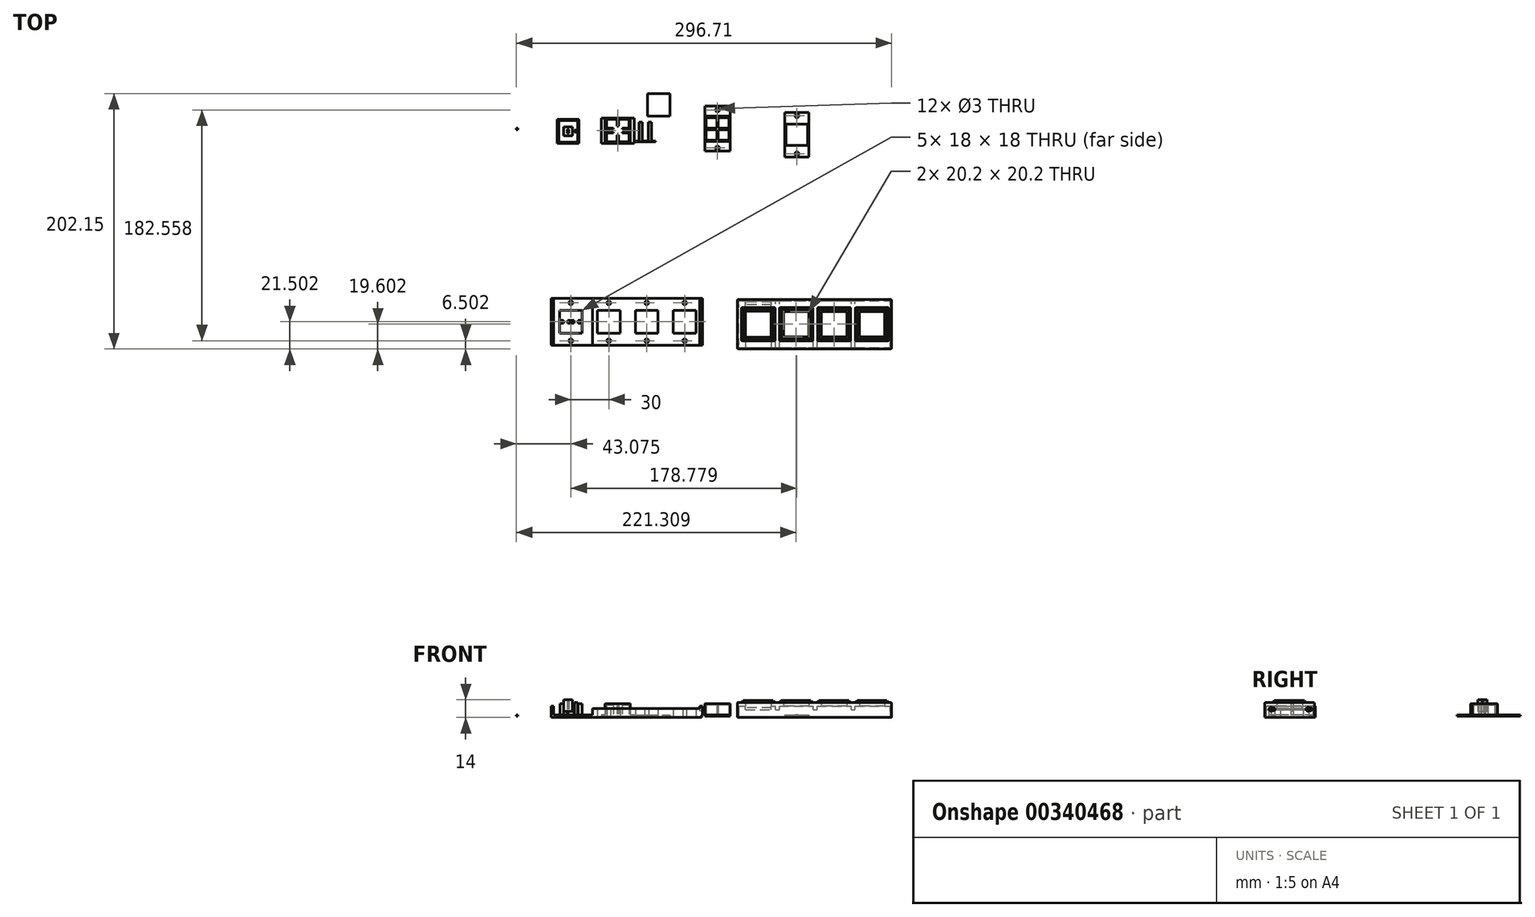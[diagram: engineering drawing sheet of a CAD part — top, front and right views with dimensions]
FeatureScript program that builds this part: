
annotation { "Feature Type Name" : "Feature", "Feature Type Description" : "" }
export const myFeature = defineFeature(function(context is Context, id is Id, definition is map)
    precondition{}
    {
        {
            var Q0;
            Q0=qCreatedBy(makeId("Top.planeOp"),FACE);
            var sketch = newSketch(context, id + "F0", { "sketchPlane" : qUnion([Q0])});
            skPoint(sketch, "E0.middle", {"position": v(0, 0) * mm});
            skLineSegment(sketch, "E1.bottom", {"start": v(10, -10) * mm, "end": v(-10, -10) * mm});
            skLineSegment(sketch, "E1.top", {"start": v(10, 10) * mm, "end": v(-10, 10) * mm});
            skLineSegment(sketch, "E1.left", {"start": v(10, -10) * mm, "end": v(10, 10) * mm});
            skLineSegment(sketch, "E1.right", {"start": v(-10, -10) * mm, "end": v(-10, 10) * mm});
            skSolve(sketch);
        }
        {
            var Q0;
            Q0=makeQuery(id+"F0.imprint","IMPRINT",FACE,{"disambiguationData":[TD([[makeQuery(id+"F0.imprint","IMPRINT",EDGE,{"derivedFrom":sQuery(id+"F0.wireOp",EDGE,"E1.bottom")}),-1.0]])]});
            extrude(context, id + "F1", {"entities" : qUnion([Q0]), "depth" : 10 * mm});
        }
        {
            var Q0;
            Q0=makeQuery(id+"F1.opExtrude","CAP_FACE",FACE,{"disambiguationData":[OSD([sQuery(id+"F0.wireOp",EDGE,"E1.bottom"),sQuery(id+"F0.wireOp",EDGE,"E1.top"),sQuery(id+"F0.wireOp",EDGE,"E1.left"),sQuery(id+"F0.wireOp",EDGE,"E1.right")])],"isStart":true});
            shell(context, id + "F2", {"entities" : qUnion([Q0]), "thickness" : 1 * mm});
        }
        {
            var Q0;
            Q0=qCreatedBy(makeId("Top.planeOp"),FACE);
            var sketch = newSketch(context, id + "F3", { "sketchPlane" : qUnion([Q0])});
            skLineSegment(sketch, "E2.bottom", {"start": v(0.5, -9) * mm, "end": v(-0.5, -9) * mm});
            skLineSegment(sketch, "E2.top", {"start": v(0.5, 9) * mm, "end": v(-0.5, 9) * mm});
            skLineSegment(sketch, "E2.left", {"start": v(0.5, -9) * mm, "end": v(0.5, -0.5) * mm});
            skLineSegment(sketch, "E2.right", {"start": v(-0.5, -9) * mm, "end": v(-0.5, -0.5) * mm});
            skLineSegment(sketch, "E3.bottom", {"start": v(9, 0.5) * mm, "end": v(0.5, 0.5) * mm});
            skLineSegment(sketch, "E3.top", {"start": v(9, -0.5) * mm, "end": v(0.5, -0.5) * mm});
            skLineSegment(sketch, "E3.left", {"start": v(9, 0.5) * mm, "end": v(9, -0.5) * mm});
            skLineSegment(sketch, "E3.right", {"start": v(-9, 0.5) * mm, "end": v(-9, -0.5) * mm});
            skLineSegment(sketch, "E4.trimOffspring", {"start": v(-0.5, 0.5) * mm, "end": v(-0.5, 9) * mm});
            skLineSegment(sketch, "E5.trimOffspring", {"start": v(-0.5, -0.5) * mm, "end": v(-9, -0.5) * mm});
            skLineSegment(sketch, "E6.trimOffspring", {"start": v(0.5, 0.5) * mm, "end": v(0.5, 9) * mm});
            skLineSegment(sketch, "E7.trimOffspring", {"start": v(-0.5, 0.5) * mm, "end": v(-9, 0.5) * mm});
            skSolve(sketch);
        }
        {
            var Q0;
            Q0=qSketchRegion(id+"F3",true);
            extrude(context, id + "F4", {"entities" : qUnion([Q0]), "operationType" : NewBodyOperationType.ADD, "depth" : 9 * mm});
        }
        {
            var Q0;
            Q0=qCreatedBy(makeId("Top.planeOp"),FACE);
            var sketch = newSketch(context, id + "F5", { "sketchPlane" : qUnion([Q0])});
            skLineSegment(sketch, "E8.bottom", {"start": v(-10, -9.5) * mm, "end": v(10, -9.5) * mm});
            skLineSegment(sketch, "E8.top", {"start": v(-10, -17.5) * mm, "end": v(10, -17.5) * mm});
            skLineSegment(sketch, "E8.left", {"start": v(-10, -9.5) * mm, "end": v(-10, -17.5) * mm});
            skLineSegment(sketch, "E8.right", {"start": v(10, -9.5) * mm, "end": v(10, -17.5) * mm});
            skLineSegment(sketch, "E9.bottom", {"start": v(-10, 10) * mm, "end": v(10, 10) * mm});
            skLineSegment(sketch, "E9.top", {"start": v(-10, 18) * mm, "end": v(10, 18) * mm});
            skLineSegment(sketch, "E9.left", {"start": v(-10, 10) * mm, "end": v(-10, 18) * mm});
            skLineSegment(sketch, "E9.right", {"start": v(10, 10) * mm, "end": v(10, 18) * mm});
            skLineSegment(sketch, "E10.bottom", {"start": v(-10, -9.5) * mm, "end": v(-13, -9.5) * mm, "construction": true});
            skLineSegment(sketch, "E10.top", {"start": v(-10, 10) * mm, "end": v(-13, 10) * mm, "construction": true});
            skLineSegment(sketch, "E10.left", {"start": v(-10, -9.5) * mm, "end": v(-10, 10) * mm});
            skLineSegment(sketch, "E10.right", {"start": v(-13, -9.5) * mm, "end": v(-13, 10) * mm, "construction": true});
            skLineSegment(sketch, "E11.bottom", {"start": v(10, -9.5) * mm, "end": v(13, -9.5) * mm, "construction": true});
            skLineSegment(sketch, "E11.top", {"start": v(10, 10) * mm, "end": v(13, 10) * mm, "construction": true});
            skLineSegment(sketch, "E11.left", {"start": v(10, -9.5) * mm, "end": v(10, 10) * mm});
            skLineSegment(sketch, "E11.right", {"start": v(13, -9.5) * mm, "end": v(13, 10) * mm, "construction": true});
            skCircle(sketch, "E12", {"center": v(0, 15) * mm, "radius": 1.5 * mm});
            skCircle(sketch, "E13", {"center": v(0, -15) * mm, "radius": 1.5 * mm});
            skSolve(sketch);
        }
        {
            var Q0;
            Q0=makeQuery(id+"F5.imprint","IMPRINT",FACE,{"disambiguationData":[TD([[makeQuery(id+"F5.imprint","IMPRINT",EDGE,{"derivedFrom":sQuery(id+"F5.wireOp",EDGE,"E10.bottom")}),-1.0]])]});
            var Q1;
            Q1=makeQuery(id+"F5.imprint","IMPRINT",FACE,{"disambiguationData":[TD([[makeQuery(id+"F5.imprint","IMPRINT",EDGE,{"derivedFrom":sQuery(id+"F5.wireOp",EDGE,"E8.bottom")}),-1.0]])]});
            var Q2;
            Q2=makeQuery(id+"F5.imprint","IMPRINT",FACE,{"disambiguationData":[TD([[makeQuery(id+"F5.imprint","IMPRINT",EDGE,{"derivedFrom":sQuery(id+"F5.wireOp",EDGE,"E11.bottom")}),1.0]])]});
            var Q3;
            Q3=makeQuery(id+"F5.imprint","IMPRINT",FACE,{"disambiguationData":[TD([[makeQuery(id+"F5.imprint","IMPRINT",EDGE,{"derivedFrom":sQuery(id+"F5.wireOp",EDGE,"E9.bottom")}),1.0]])]});
            extrude(context, id + "F6", {"entities" : qUnion([Q0, Q1, Q2, Q3]), "operationType" : NewBodyOperationType.ADD, "depth" : 1 * mm});
        }
        {
            var Q0;
            Q0=qCreatedBy(makeId("Top.planeOp"),FACE);
            var sketch = newSketch(context, id + "F7", { "sketchPlane" : qUnion([Q0])});
            skLineSegment(sketch, "E14.bottom", {"start": v(53.3, 4.9) * mm, "end": v(72.3, 4.9) * mm});
            skLineSegment(sketch, "E14.top", {"start": v(53.3, -14.1) * mm, "end": v(72.3, -14.1) * mm});
            skLineSegment(sketch, "E14.left", {"start": v(53.3, 4.9) * mm, "end": v(53.3, -14.1) * mm});
            skLineSegment(sketch, "E14.right", {"start": v(72.3, 4.9) * mm, "end": v(72.3, -14.1) * mm});
            skLineSegment(sketch, "E15.top", {"start": v(53.3, 12.9) * mm, "end": v(72.3, 12.9) * mm});
            skLineSegment(sketch, "E15.left", {"start": v(53.3, 4.9) * mm, "end": v(53.3, 12.9) * mm});
            skLineSegment(sketch, "E15.right", {"start": v(72.3, 4.9) * mm, "end": v(72.3, 12.9) * mm});
            skLineSegment(sketch, "E16.top", {"start": v(53.3, -22.1) * mm, "end": v(72.3, -22.1) * mm});
            skLineSegment(sketch, "E16.left", {"start": v(53.3, -14.1) * mm, "end": v(53.3, -22.1) * mm});
            skLineSegment(sketch, "E16.right", {"start": v(72.3, -14.1) * mm, "end": v(72.3, -22.1) * mm});
            skLineSegment(sketch, "E17.bottom", {"start": v(62.05, 4.9) * mm, "end": v(63.55, 4.9) * mm, "construction": true});
            skLineSegment(sketch, "E17.top", {"start": v(62.05, -14.1) * mm, "end": v(63.55, -14.1) * mm, "construction": true});
            skLineSegment(sketch, "E17.left", {"start": v(62.05, 4.9) * mm, "end": v(62.05, -14.1) * mm, "construction": true});
            skLineSegment(sketch, "E17.right", {"start": v(63.55, 4.9) * mm, "end": v(63.55, -14.1) * mm, "construction": true});
            skLineSegment(sketch, "E18.bottom", {"start": v(53.3, -3.86) * mm, "end": v(54.3, -3.86) * mm, "construction": true});
            skLineSegment(sketch, "E18.top", {"start": v(53.3, -5.36) * mm, "end": v(57.43, -5.36) * mm, "construction": true});
            skLineSegment(sketch, "E18.left", {"start": v(53.3, -3.86) * mm, "end": v(53.3, -5.36) * mm, "construction": true});
            skLineSegment(sketch, "E18.right", {"start": v(72.3, -3.86) * mm, "end": v(72.3, -5.36) * mm, "construction": true});
            skLineSegment(sketch, "E19.0", {"start": v(54.3, 3.9) * mm, "end": v(71.3, 3.9) * mm});
            skLineSegment(sketch, "E19.1", {"start": v(54.3, 3.9) * mm, "end": v(54.3, -13.1) * mm});
            skLineSegment(sketch, "E19.2", {"start": v(54.3, -13.1) * mm, "end": v(71.3, -13.1) * mm});
            skLineSegment(sketch, "E19.3", {"start": v(71.3, 3.9) * mm, "end": v(71.3, -13.1) * mm});
            skCircle(sketch, "E20", {"center": v(62.8, 10.4) * mm, "radius": 1.5 * mm});
            skPoint(sketch, "E21", {"position": v(62.8, 4.9) * mm});
            skLineSegment(sketch, "E22.bottom", {"start": v(63.3, -5.1) * mm, "end": v(62.3, -5.1) * mm, "construction": true});
            skLineSegment(sketch, "E22.top", {"start": v(63.3, -4.1) * mm, "end": v(62.3, -4.1) * mm, "construction": true});
            skLineSegment(sketch, "E22.left", {"start": v(63.3, -5.1) * mm, "end": v(63.3, -4.1) * mm, "construction": true});
            skLineSegment(sketch, "E22.right", {"start": v(62.3, -5.1) * mm, "end": v(62.3, -4.1) * mm, "construction": true});
            skPoint(sketch, "E22.middle", {"position": v(62.8, -4.6) * mm});
            skPoint(sketch, "E22.middle.positionSnap0", {"position": v(62.05, -4.6) * mm});
            skPoint(sketch, "E22.middle.positionSnap1", {"position": v(62.8, -3.86) * mm});
            skPoint(sketch, "E22.centerSnap0", {"position": v(62.05, -4.6) * mm});
            skPoint(sketch, "E22.centerSnap1", {"position": v(62.8, -3.86) * mm});
            skCircle(sketch, "E23", {"center": v(62.8, -19.6) * mm, "radius": 1.5 * mm});
            skPoint(sketch, "E23.centerSnap0", {"position": v(62.8, 12.9) * mm});
            skLineSegment(sketch, "E24.bottom", {"start": v(57.43, 3.9) * mm, "end": v(58.93, 3.9) * mm});
            skLineSegment(sketch, "E24.top", {"start": v(57.43, -13.1) * mm, "end": v(58.93, -13.1) * mm});
            skLineSegment(sketch, "E24.left", {"start": v(57.43, 3.9) * mm, "end": v(57.43, -3.86) * mm});
            skLineSegment(sketch, "E24.right", {"start": v(58.93, 3.9) * mm, "end": v(58.93, -3.86) * mm});
            skLineSegment(sketch, "E25.bottom", {"start": v(66.68, 3.9) * mm, "end": v(68.18, 3.9) * mm});
            skLineSegment(sketch, "E25.top", {"start": v(66.68, -13.1) * mm, "end": v(68.18, -13.1) * mm});
            skLineSegment(sketch, "E25.left", {"start": v(66.68, 3.9) * mm, "end": v(66.68, -3.86) * mm});
            skLineSegment(sketch, "E25.right", {"start": v(68.18, 3.9) * mm, "end": v(68.18, -3.86) * mm});
            skLineSegment(sketch, "E26.bottom", {"start": v(54.3, -3.86) * mm, "end": v(57.43, -3.86) * mm});
            skLineSegment(sketch, "E26.top", {"start": v(54.3, -5.36) * mm, "end": v(57.43, -5.36) * mm});
            skLineSegment(sketch, "E26.left", {"start": v(54.3, -3.86) * mm, "end": v(54.3, -5.36) * mm});
            skLineSegment(sketch, "E26.right", {"start": v(71.3, -3.86) * mm, "end": v(71.3, -5.36) * mm});
            skLineSegment(sketch, "E27.trimOffspring", {"start": v(58.93, -3.86) * mm, "end": v(66.68, -3.86) * mm, "construction": true});
            skLineSegment(sketch, "E28.trimOffspring", {"start": v(58.93, -3.86) * mm, "end": v(66.68, -3.86) * mm});
            skLineSegment(sketch, "E29.trimOffspring", {"start": v(57.43, -5.36) * mm, "end": v(57.43, -13.1) * mm});
            skLineSegment(sketch, "E30.trimOffspring", {"start": v(58.93, -5.36) * mm, "end": v(58.93, -13.1) * mm});
            skLineSegment(sketch, "E31.trimOffspring", {"start": v(58.93, -5.36) * mm, "end": v(66.68, -5.36) * mm, "construction": true});
            skLineSegment(sketch, "E32.trimOffspring", {"start": v(58.93, -5.36) * mm, "end": v(66.68, -5.36) * mm});
            skLineSegment(sketch, "E33.trimOffspring", {"start": v(68.18, -3.86) * mm, "end": v(72.3, -3.86) * mm, "construction": true});
            skLineSegment(sketch, "E34.trimOffspring", {"start": v(66.68, -5.36) * mm, "end": v(66.68, -13.1) * mm});
            skLineSegment(sketch, "E35.trimOffspring", {"start": v(68.18, -5.36) * mm, "end": v(72.3, -5.36) * mm, "construction": true});
            skLineSegment(sketch, "E36.trimOffspring", {"start": v(68.18, -5.36) * mm, "end": v(68.18, -13.1) * mm});
            skLineSegment(sketch, "E37.trimOffspring", {"start": v(68.18, -3.86) * mm, "end": v(71.3, -3.86) * mm});
            skLineSegment(sketch, "E38.trimOffspring", {"start": v(68.18, -5.36) * mm, "end": v(71.3, -5.36) * mm});
            skLineSegment(sketch, "E39.bottom", {"start": v(55.04, 3.07) * mm, "end": v(61.04, 3.07) * mm, "construction": true});
            skLineSegment(sketch, "E39.top", {"start": v(55.04, -2.93) * mm, "end": v(61.04, -2.93) * mm, "construction": true});
            skLineSegment(sketch, "E39.left", {"start": v(55.04, 3.07) * mm, "end": v(55.04, -2.93) * mm, "construction": true});
            skLineSegment(sketch, "E39.right", {"start": v(61.04, 3.07) * mm, "end": v(61.04, -2.93) * mm, "construction": true});
            skLineSegment(sketch, "E40.bottom", {"start": v(64.3, 3.07) * mm, "end": v(70.3, 3.07) * mm, "construction": true});
            skLineSegment(sketch, "E40.top", {"start": v(64.3, -2.93) * mm, "end": v(70.3, -2.93) * mm, "construction": true});
            skLineSegment(sketch, "E40.left", {"start": v(64.3, 3.07) * mm, "end": v(64.3, -2.93) * mm, "construction": true});
            skLineSegment(sketch, "E40.right", {"start": v(70.3, 3.07) * mm, "end": v(70.3, -2.93) * mm, "construction": true});
            skSolve(sketch);
        }
        {
            var Q0;
            Q0=makeQuery(id+"F7.imprint","IMPRINT",FACE,{"disambiguationData":[TD([[makeQuery(id+"F7.imprint","IMPRINT",EDGE,{"derivedFrom":sQuery(id+"F7.wireOp",EDGE,"E14.left")}),1.0]])]});
            var Q1;
            Q1=makeQuery(id+"F7.imprint","IMPRINT",FACE,{"disambiguationData":[TD([[makeQuery(id+"F7.imprint","IMPRINT",EDGE,{"derivedFrom":sQuery(id+"F7.wireOp",EDGE,"E14.bottom")}),1.0]])]});
            var Q2;
            Q2=makeQuery(id+"F7.imprint","IMPRINT",FACE,{"disambiguationData":[TD([[makeQuery(id+"F7.imprint","IMPRINT",EDGE,{"derivedFrom":sQuery(id+"F7.wireOp",EDGE,"MVN2uy9p-aqT3-YTcf-EiQD-pbnfHAAz3MAc.bottom")}),-1.0]])]});
            var Q3;
            Q3=makeQuery(id+"F7.imprint","IMPRINT",FACE,{"disambiguationData":[TD([[makeQuery(id+"F7.imprint","IMPRINT",EDGE,{"derivedFrom":sQuery(id+"F7.wireOp",EDGE,"sKF5d9FJ-0LFq-fu9g-diTO-PrwaPXYM0bzY.bottom")}),-1.0]])]});
            var Q4;
            Q4=makeQuery(id+"F7.imprint","IMPRINT",FACE,{"disambiguationData":[TD([[makeQuery(id+"F7.imprint","IMPRINT",EDGE,{"derivedFrom":sQuery(id+"F7.wireOp",EDGE,"E14.top")}),-1.0]])]});
            var Q5;
            Q5=makeQuery(id+"F7.imprint","IMPRINT",FACE,{"disambiguationData":[TD([[makeQuery(id+"F7.imprint","IMPRINT",EDGE,{"derivedFrom":sQuery(id+"F7.wireOp",EDGE,"E24.bottom")}),-1.0]])]});
            var Q6;
            Q6=makeQuery(id+"F7.imprint","IMPRINT",FACE,{"disambiguationData":[TD([[makeQuery(id+"F7.imprint","IMPRINT",EDGE,{"derivedFrom":sQuery(id+"F7.wireOp",EDGE,"E25.bottom")}),-1.0]])]});
            extrude(context, id + "F8", {"entities" : qUnion([Q0, Q1, Q2, Q3, Q4, Q5, Q6]), "depth" : 1 * mm});
        }
        {
            var Q0;
            Q0=qCreatedBy(makeId("Top.planeOp"),FACE);
            var sketch = newSketch(context, id + "F9", { "sketchPlane" : qUnion([Q0])});
            skLineSegment(sketch, "E41.bottom", {"start": v(-88.88, 8.7) * mm, "end": v(-68.88, 8.7) * mm});
            skLineSegment(sketch, "E41.top", {"start": v(-88.88, -11.3) * mm, "end": v(-68.88, -11.3) * mm});
            skLineSegment(sketch, "E41.left", {"start": v(-88.88, 8.7) * mm, "end": v(-88.88, -11.3) * mm});
            skLineSegment(sketch, "E41.right", {"start": v(-68.88, 8.7) * mm, "end": v(-68.88, -11.3) * mm});
            skSolve(sketch);
        }
        {
            var Q0;
            Q0=makeQuery(id+"F9.imprint","IMPRINT",FACE,{"disambiguationData":[TD([[makeQuery(id+"F9.imprint","IMPRINT",EDGE,{"derivedFrom":sQuery(id+"F9.wireOp",EDGE,"E41.bottom")}),-1.0]])]});
            extrude(context, id + "F10", {"entities" : qUnion([Q0]), "depth" : 10 * mm});
        }
        {
            var Q0;
            Q0=makeQuery(id+"F15.boolean.opBoolean","MERGE",FACE,{"derivedFrom":[makeQuery(id+"F10.opExtrude","CAP_FACE",FACE,{"disambiguationData":[OSD([sQuery(id+"F9.wireOp",EDGE,"E41.bottom"),sQuery(id+"F9.wireOp",EDGE,"E41.top"),sQuery(id+"F9.wireOp",EDGE,"E41.left"),sQuery(id+"F9.wireOp",EDGE,"E41.right")])],"isStart":true}),makeQuery(id+"F15.opExtrude","CAP_FACE",FACE,{"disambiguationData":[OSD([sQuery(id+"F14.wireOp",EDGE,"E49.bottom"),sQuery(id+"F14.wireOp",EDGE,"E49.top"),sQuery(id+"F14.wireOp",EDGE,"E49.left"),sQuery(id+"F14.wireOp",EDGE,"E49.right"),sQuery(id+"F14.wireOp",EDGE,"E50.trimOffspring"),sQuery(id+"F14.wireOp",EDGE,"E52.trimOffspring"),sQuery(id+"F14.wireOp",EDGE,"E54"),sQuery(id+"F14.wireOp",EDGE,"E55"),sQuery(id+"F14.wireOp",EDGE,"E56.bottom"),sQuery(id+"F14.wireOp",EDGE,"E56.top"),sQuery(id+"F14.wireOp",EDGE,"E56.left"),sQuery(id+"F14.wireOp",EDGE,"E57.bottom"),sQuery(id+"F14.wireOp",EDGE,"E57.top"),sQuery(id+"F14.wireOp",EDGE,"E57.left"),sQuery(id+"F14.wireOp",EDGE,"E58.bottom"),sQuery(id+"F14.wireOp",EDGE,"E58.top"),sQuery(id+"F14.wireOp",EDGE,"E58.right"),sQuery(id+"F14.wireOp",EDGE,"E59.bottom"),sQuery(id+"F14.wireOp",EDGE,"E59.top"),sQuery(id+"F14.wireOp",EDGE,"E59.right")])],"isStart":true})]});
            var sketch = newSketch(context, id + "F11", { "sketchPlane" : qUnion([Q0])});
            skLineSegment(sketch, "E42.bottom", {"start": v(-88.88, 11.3) * mm, "end": v(-68.88, 11.3) * mm});
            skLineSegment(sketch, "E42.top", {"start": v(-88.88, 14.3) * mm, "end": v(-68.88, 14.3) * mm, "construction": true});
            skLineSegment(sketch, "E42.left", {"start": v(-88.88, 11.3) * mm, "end": v(-88.88, 14.3) * mm, "construction": true});
            skLineSegment(sketch, "E42.right", {"start": v(-68.88, 11.3) * mm, "end": v(-68.88, 14.3) * mm, "construction": true});
            skLineSegment(sketch, "E43.bottom", {"start": v(-88.88, -8.7) * mm, "end": v(-68.88, -8.7) * mm});
            skLineSegment(sketch, "E43.top", {"start": v(-88.88, -11.7) * mm, "end": v(-68.88, -11.7) * mm});
            skLineSegment(sketch, "E43.left", {"start": v(-88.88, -8.7) * mm, "end": v(-88.88, -11.7) * mm, "construction": true});
            skLineSegment(sketch, "E43.right", {"start": v(-68.88, -8.7) * mm, "end": v(-68.88, -11.7) * mm, "construction": true});
            skLineSegment(sketch, "E44.bottom", {"start": v(-88.88, -8.7) * mm, "end": v(-91.88, -8.7) * mm});
            skLineSegment(sketch, "E44.top", {"start": v(-88.88, 11.3) * mm, "end": v(-91.88, 11.3) * mm});
            skLineSegment(sketch, "E44.left", {"start": v(-88.88, -8.7) * mm, "end": v(-88.88, 11.3) * mm});
            skLineSegment(sketch, "E44.right", {"start": v(-91.88, -8.7) * mm, "end": v(-91.88, 11.3) * mm});
            skLineSegment(sketch, "E45.bottom", {"start": v(-68.88, -8.7) * mm, "end": v(-65.88, -8.7) * mm});
            skLineSegment(sketch, "E45.top", {"start": v(-68.88, 11.3) * mm, "end": v(-65.88, 11.3) * mm});
            skLineSegment(sketch, "E45.left", {"start": v(-68.88, -8.7) * mm, "end": v(-68.88, 11.3) * mm});
            skLineSegment(sketch, "E45.right", {"start": v(-65.88, -8.7) * mm, "end": v(-65.88, 11.3) * mm});
            skLineSegment(sketch, "E46.bottom", {"start": v(-88.88, -11.7) * mm, "end": v(-68.88, -11.7) * mm, "construction": true});
            skLineSegment(sketch, "E46.top", {"start": v(-88.88, -16.7) * mm, "end": v(-68.88, -16.7) * mm, "construction": true});
            skLineSegment(sketch, "E46.left", {"start": v(-88.88, -11.7) * mm, "end": v(-88.88, -16.7) * mm, "construction": true});
            skLineSegment(sketch, "E46.right", {"start": v(-68.88, -11.7) * mm, "end": v(-68.88, -16.7) * mm, "construction": true});
            skCircle(sketch, "E47", {"center": v(-78.88, -13.7) * mm, "radius": 1.5 * mm, "construction": true});
            skSolve(sketch);
        }
        {
            var Q0;
            Q0=qSketchRegion(id+"F11",true);
            extrude(context, id + "F12", {"entities" : qUnion([Q0]), "operationType" : NewBodyOperationType.ADD, "oppositeDirection" : true, "depth" : 0.95 * mm});
        }
        {
            var Q0;
            Q0=makeQuery(id+"F10.opExtrude","CAP_FACE",FACE,{"disambiguationData":[OSD([sQuery(id+"F9.wireOp",EDGE,"E41.bottom"),sQuery(id+"F9.wireOp",EDGE,"E41.top"),sQuery(id+"F9.wireOp",EDGE,"E41.left"),sQuery(id+"F9.wireOp",EDGE,"E41.right")])],"isStart":true});
            shell(context, id + "F13", {"entities" : qUnion([Q0]), "thickness" : 1 * mm});
        }
        {
            var Q0;
            Q0=qCreatedBy(makeId("Top.planeOp"),FACE);
            var sketch = newSketch(context, id + "F14", { "sketchPlane" : qUnion([Q0])});
            skLineSegment(sketch, "E48.bottom", {"start": v(-87.88, -0.1) * mm, "end": v(-79.38, -0.1) * mm, "construction": true});
            skLineSegment(sketch, "E48.top", {"start": v(-87.88, -2.5) * mm, "end": v(-79.38, -2.5) * mm, "construction": true});
            skLineSegment(sketch, "E48.left", {"start": v(-87.88, -0.1) * mm, "end": v(-87.88, -2.5) * mm, "construction": true});
            skLineSegment(sketch, "E48.right", {"start": v(-69.88, -0.1) * mm, "end": v(-69.88, -2.5) * mm, "construction": true});
            skLineSegment(sketch, "E49.bottom", {"start": v(-79.38, 7.7) * mm, "end": v(-78.38, 7.7) * mm});
            skLineSegment(sketch, "E49.top", {"start": v(-79.38, -10.3) * mm, "end": v(-78.38, -10.3) * mm});
            skLineSegment(sketch, "E49.left", {"start": v(-79.38, 7.7) * mm, "end": v(-79.38, -0.1) * mm});
            skLineSegment(sketch, "E49.right", {"start": v(-78.38, 7.7) * mm, "end": v(-78.38, -0.1) * mm});
            skLineSegment(sketch, "E50.trimOffspring", {"start": v(-79.38, -10.3) * mm, "end": v(-79.38, -2.5) * mm});
            skLineSegment(sketch, "E51.trimOffspring", {"start": v(-78.38, -0.1) * mm, "end": v(-69.88, -0.1) * mm, "construction": true});
            skLineSegment(sketch, "E52.trimOffspring", {"start": v(-78.38, -2.5) * mm, "end": v(-78.38, -10.3) * mm});
            skLineSegment(sketch, "E53.trimOffspring", {"start": v(-78.38, -2.5) * mm, "end": v(-69.88, -2.5) * mm, "construction": true});
            skLineSegment(sketch, "E54", {"start": v(-79.38, -2.5) * mm, "end": v(-79.38, -0.1) * mm});
            skLineSegment(sketch, "E55", {"start": v(-78.38, -2.5) * mm, "end": v(-78.38, -0.1) * mm});
            skLineSegment(sketch, "E56.bottom", {"start": v(-87.88, -2.5) * mm, "end": v(-79.38, -2.5) * mm});
            skLineSegment(sketch, "E56.top", {"start": v(-87.88, -3.3) * mm, "end": v(-79.38, -3.3) * mm});
            skLineSegment(sketch, "E56.left", {"start": v(-87.88, -2.5) * mm, "end": v(-87.88, -3.3) * mm});
            skLineSegment(sketch, "E56.right", {"start": v(-79.38, -2.5) * mm, "end": v(-79.38, -3.3) * mm});
            skLineSegment(sketch, "E57.bottom", {"start": v(-87.88, -0.1) * mm, "end": v(-79.38, -0.1) * mm});
            skLineSegment(sketch, "E57.top", {"start": v(-87.88, 0.7) * mm, "end": v(-79.38, 0.7) * mm});
            skLineSegment(sketch, "E57.left", {"start": v(-87.88, -0.1) * mm, "end": v(-87.88, 0.7) * mm});
            skLineSegment(sketch, "E57.right", {"start": v(-79.38, -0.1) * mm, "end": v(-79.38, 0.7) * mm});
            skLineSegment(sketch, "E58.bottom", {"start": v(-78.38, -3.3) * mm, "end": v(-69.88, -3.3) * mm});
            skLineSegment(sketch, "E58.top", {"start": v(-78.38, -2.5) * mm, "end": v(-69.88, -2.5) * mm});
            skLineSegment(sketch, "E58.left", {"start": v(-78.38, -3.3) * mm, "end": v(-78.38, -2.5) * mm});
            skLineSegment(sketch, "E58.right", {"start": v(-69.88, -3.3) * mm, "end": v(-69.88, -2.5) * mm});
            skLineSegment(sketch, "E59.bottom", {"start": v(-78.38, -0.1) * mm, "end": v(-69.88, -0.1) * mm});
            skLineSegment(sketch, "E59.top", {"start": v(-78.38, 0.7) * mm, "end": v(-69.88, 0.7) * mm});
            skLineSegment(sketch, "E59.left", {"start": v(-78.38, -0.1) * mm, "end": v(-78.38, 0.7) * mm});
            skLineSegment(sketch, "E59.right", {"start": v(-69.88, -0.1) * mm, "end": v(-69.88, 0.7) * mm});
            skSolve(sketch);
        }
        {
            var Q0;
            Q0=makeQuery(id+"F14.imprint","IMPRINT",FACE,{"disambiguationData":[TD([[makeQuery(id+"F14.imprint","IMPRINT",EDGE,{"derivedFrom":sQuery(id+"F14.wireOp",EDGE,"E49.bottom")}),-1.0]])]});
            var Q1;
            Q1=makeQuery(id+"F14.imprint","IMPRINT",FACE,{"disambiguationData":[TD([[makeQuery(id+"F14.imprint","IMPRINT",EDGE,{"derivedFrom":sQuery(id+"F14.wireOp",EDGE,"E56.bottom")}),-1.0]])]});
            var Q2;
            Q2=makeQuery(id+"F14.imprint","IMPRINT",FACE,{"disambiguationData":[TD([[makeQuery(id+"F14.imprint","IMPRINT",EDGE,{"derivedFrom":sQuery(id+"F14.wireOp",EDGE,"E57.bottom")}),1.0]])]});
            var Q3;
            Q3=makeQuery(id+"F14.imprint","IMPRINT",FACE,{"disambiguationData":[TD([[makeQuery(id+"F14.imprint","IMPRINT",EDGE,{"derivedFrom":sQuery(id+"F14.wireOp",EDGE,"E59.bottom")}),1.0]])]});
            var Q4;
            Q4=makeQuery(id+"F14.imprint","IMPRINT",FACE,{"disambiguationData":[TD([[makeQuery(id+"F14.imprint","IMPRINT",EDGE,{"derivedFrom":sQuery(id+"F14.wireOp",EDGE,"E58.bottom")}),1.0]])]});
            var Q5;
            Q5=sQuery(id+"F14.wireOp",EDGE,"E49.left");
            var Q6;
            Q6=sQuery(id+"F14.wireOp",EDGE,"E50.trimOffspring");
            var Q7;
            Q7=sQuery(id+"F14.wireOp",EDGE,"E48.top");
            var Q8;
            Q8=sQuery(id+"F14.wireOp",EDGE,"E51.trimOffspring");
            var Q9;
            Q9=sQuery(id+"F14.wireOp",EDGE,"E49.bottom");
            var Q10;
            Q10=sQuery(id+"F14.wireOp",EDGE,"E49.right");
            var Q11;
            Q11=sQuery(id+"F14.wireOp",EDGE,"E49.top");
            var Q12;
            Q12=sQuery(id+"F14.wireOp",EDGE,"E48.bottom");
            var Q13;
            Q13=sQuery(id+"F14.wireOp",EDGE,"E52.trimOffspring");
            var Q14;
            Q14=sQuery(id+"F14.wireOp",EDGE,"E53.trimOffspring");
            var Q15;
            Q15=sQuery(id+"F14.wireOp",EDGE,"E48.right");
            var Q16;
            Q16=sQuery(id+"F14.wireOp",EDGE,"E48.left");
            extrude(context, id + "F15", {"entities" : qUnion([Q0, Q1, Q2, Q3, Q4]), "operationType" : NewBodyOperationType.ADD, "surfaceEntities" : qUnion([Q5, Q6, Q7, Q8, Q9, Q10, Q11, Q12, Q13, Q14, Q15, Q16]), "depth" : 9 * mm});
        }
        {
            var Q0;
            Q0=makeQuery(id+"F15.boolean.opBoolean","MERGE",FACE,{"derivedFrom":[makeQuery(id+"F10.opExtrude","CAP_FACE",FACE,{"disambiguationData":[OSD([sQuery(id+"F9.wireOp",EDGE,"E41.bottom"),sQuery(id+"F9.wireOp",EDGE,"E41.top"),sQuery(id+"F9.wireOp",EDGE,"E41.left"),sQuery(id+"F9.wireOp",EDGE,"E41.right")])],"isStart":true}),makeQuery(id+"F15.opExtrude","CAP_FACE",FACE,{"disambiguationData":[OSD([sQuery(id+"F14.wireOp",EDGE,"E48.bottom"),sQuery(id+"F14.wireOp",EDGE,"E48.top"),sQuery(id+"F14.wireOp",EDGE,"E48.left"),sQuery(id+"F14.wireOp",EDGE,"E48.right"),sQuery(id+"F14.wireOp",EDGE,"E49.bottom"),sQuery(id+"F14.wireOp",EDGE,"E49.top"),sQuery(id+"F14.wireOp",EDGE,"E49.left"),sQuery(id+"F14.wireOp",EDGE,"E49.right"),sQuery(id+"F14.wireOp",EDGE,"E50.trimOffspring"),sQuery(id+"F14.wireOp",EDGE,"E51.trimOffspring"),sQuery(id+"F14.wireOp",EDGE,"E52.trimOffspring"),sQuery(id+"F14.wireOp",EDGE,"E53.trimOffspring")])],"isStart":true})]});
            var sketch = newSketch(context, id + "F16", { "sketchPlane" : qUnion([Q0])});
            skLineSegment(sketch, "E60.bottom", {"start": v(-75.28, -2.3) * mm, "end": v(-82.48, -2.3) * mm});
            skLineSegment(sketch, "E60.top", {"start": v(-75.28, 4.9) * mm, "end": v(-82.48, 4.9) * mm});
            skLineSegment(sketch, "E60.left", {"start": v(-75.28, -2.3) * mm, "end": v(-75.28, 4.9) * mm});
            skLineSegment(sketch, "E60.right", {"start": v(-82.48, -2.3) * mm, "end": v(-82.48, 4.9) * mm});
            skPoint(sketch, "E60.middle.positionSnap1", {"position": v(-88.88, 1.8) * mm});
            skSolve(sketch);
        }
        {
            var Q0;
            {var subQ1=makeQuery(id+"F15.opExtrude","CAP_EDGE",EDGE,{"disambiguationData":[OSD([sQuery(id+"F14.wireOp",EDGE,"E49.right")])],"isStart":true});var subQ3=sQuery(id+"F16.wireOp",EDGE,"E60.bottom");var subQ4=makeQuery(id+"F16.imprint","INTERSECT",VERTEX,{"derivedFrom":[subQ1,subQ3]});Q0=makeQuery(id+"F16.imprint","IMPRINT",FACE,{"disambiguationData":[TD([[makeQuery(id+"F16.imprint","IMPRINT",EDGE,{"disambiguationData":[TD([[subQ4,-1.0]])],"derivedFrom":subQ3}),-1.0]])]});}
            extrude(context, id + "F17", {"entities" : qUnion([Q0]), "operationType" : NewBodyOperationType.REMOVE, "oppositeDirection" : true, "depth" : 9 * mm});
        }
        {
            var Q0;
            Q0=qCreatedBy(makeId("Top.planeOp"),FACE);
            var sketch = newSketch(context, id + "F18", { "sketchPlane" : qUnion([Q0])});
            skLineSegment(sketch, "E61.bottom", {"start": v(-126.7, 7.66) * mm, "end": v(-109.7, 7.66) * mm});
            skLineSegment(sketch, "E61.top", {"start": v(-126.7, -11.34) * mm, "end": v(-109.7, -11.34) * mm});
            skLineSegment(sketch, "E61.left", {"start": v(-126.7, 7.66) * mm, "end": v(-126.7, -11.34) * mm});
            skLineSegment(sketch, "E61.right", {"start": v(-109.7, 7.66) * mm, "end": v(-109.7, -11.34) * mm});
            skLineSegment(sketch, "E62.top", {"start": v(-126.7, 15.66) * mm, "end": v(-109.7, 15.66) * mm});
            skLineSegment(sketch, "E62.left", {"start": v(-126.7, 7.66) * mm, "end": v(-126.7, 15.66) * mm});
            skLineSegment(sketch, "E62.right", {"start": v(-109.7, 7.66) * mm, "end": v(-109.7, 15.66) * mm});
            skLineSegment(sketch, "E63.top", {"start": v(-126.7, -19.34) * mm, "end": v(-109.7, -19.34) * mm});
            skLineSegment(sketch, "E63.left", {"start": v(-126.7, -11.34) * mm, "end": v(-126.7, -19.34) * mm});
            skLineSegment(sketch, "E63.right", {"start": v(-109.7, -11.34) * mm, "end": v(-109.7, -19.34) * mm});
            skLineSegment(sketch, "E64.bottom", {"start": v(-118.94, 7.66) * mm, "end": v(-117.44, 7.66) * mm, "construction": true});
            skLineSegment(sketch, "E64.top", {"start": v(-118.94, -11.34) * mm, "end": v(-117.44, -11.34) * mm, "construction": true});
            skLineSegment(sketch, "E64.left", {"start": v(-118.94, 7.66) * mm, "end": v(-118.94, -1.09) * mm, "construction": true});
            skLineSegment(sketch, "E64.right", {"start": v(-117.44, 7.66) * mm, "end": v(-117.44, -1.09) * mm, "construction": true});
            skLineSegment(sketch, "E65.bottom", {"start": v(-126.7, -1.09) * mm, "end": v(-123.07, -1.09) * mm, "construction": true});
            skLineSegment(sketch, "E65.top", {"start": v(-126.7, -2.59) * mm, "end": v(-123.07, -2.59) * mm, "construction": true});
            skLineSegment(sketch, "E65.left", {"start": v(-126.7, -1.09) * mm, "end": v(-126.7, -2.59) * mm, "construction": true});
            skLineSegment(sketch, "E65.right", {"start": v(-109.7, -1.09) * mm, "end": v(-109.7, -2.59) * mm, "construction": true});
            skLineSegment(sketch, "E66.0", {"start": v(-125.7, 6.66) * mm, "end": v(-110.7, 6.66) * mm});
            skLineSegment(sketch, "E66.1", {"start": v(-125.7, 6.66) * mm, "end": v(-125.7, -10.34) * mm});
            skLineSegment(sketch, "E66.2", {"start": v(-125.7, -10.34) * mm, "end": v(-110.7, -10.34) * mm});
            skLineSegment(sketch, "E66.3", {"start": v(-110.7, 6.66) * mm, "end": v(-110.7, -10.34) * mm});
            skCircle(sketch, "E67", {"center": v(-118.2, 13.16) * mm, "radius": 1.5 * mm});
            skPoint(sketch, "E68", {"position": v(-118.2, 7.66) * mm});
            skCircle(sketch, "E69", {"center": v(-118.2, -16.84) * mm, "radius": 1.5 * mm});
            skPoint(sketch, "E69.centerSnap0", {"position": v(-118.2, 15.66) * mm});
            skLineSegment(sketch, "E70.bottom", {"start": v(-125.3, 5.6) * mm, "end": v(-119.3, 5.6) * mm, "construction": true});
            skLineSegment(sketch, "E70.top", {"start": v(-125.3, -0.4) * mm, "end": v(-119.3, -0.4) * mm, "construction": true});
            skLineSegment(sketch, "E70.left", {"start": v(-125.3, 5.6) * mm, "end": v(-125.3, -0.4) * mm, "construction": true});
            skLineSegment(sketch, "E70.right", {"start": v(-119.3, 5.6) * mm, "end": v(-119.3, -0.4) * mm, "construction": true});
            skLineSegment(sketch, "E71.bottom", {"start": v(-101.6, 6.16) * mm, "end": v(-94.6, 6.16) * mm, "construction": true});
            skLineSegment(sketch, "E71.top", {"start": v(-101.6, -0.84) * mm, "end": v(-94.6, -0.84) * mm, "construction": true});
            skLineSegment(sketch, "E71.left", {"start": v(-101.6, 6.16) * mm, "end": v(-101.6, -0.84) * mm, "construction": true});
            skLineSegment(sketch, "E71.right", {"start": v(-94.6, 6.16) * mm, "end": v(-94.6, -0.84) * mm, "construction": true});
            skLineSegment(sketch, "E72.trimOffspring", {"start": v(-117.44, -1.09) * mm, "end": v(-114.82, -1.09) * mm, "construction": true});
            skLineSegment(sketch, "E73.trimOffspring", {"start": v(-117.44, -2.59) * mm, "end": v(-114.82, -2.59) * mm, "construction": true});
            skLineSegment(sketch, "E74.trimOffspring", {"start": v(-118.94, -2.59) * mm, "end": v(-118.94, -11.34) * mm, "construction": true});
            skLineSegment(sketch, "E75.trimOffspring", {"start": v(-117.44, -2.59) * mm, "end": v(-117.44, -11.34) * mm, "construction": true});
            skLineSegment(sketch, "E76.bottom", {"start": v(-123.07, 6.66) * mm, "end": v(-121.57, 6.66) * mm});
            skLineSegment(sketch, "E76.top", {"start": v(-123.07, -10.34) * mm, "end": v(-121.57, -10.34) * mm});
            skLineSegment(sketch, "E76.left", {"start": v(-123.07, 6.66) * mm, "end": v(-123.07, -1.09) * mm});
            skLineSegment(sketch, "E76.right", {"start": v(-121.57, 6.66) * mm, "end": v(-121.57, -1.09) * mm});
            skLineSegment(sketch, "E77.bottom", {"start": v(-114.82, 6.66) * mm, "end": v(-113.32, 6.66) * mm});
            skLineSegment(sketch, "E77.top", {"start": v(-114.82, -10.34) * mm, "end": v(-113.32, -10.34) * mm});
            skLineSegment(sketch, "E77.left", {"start": v(-114.82, 6.66) * mm, "end": v(-114.82, -1.09) * mm});
            skLineSegment(sketch, "E77.right", {"start": v(-113.32, 6.66) * mm, "end": v(-113.32, -1.09) * mm});
            skLineSegment(sketch, "E78.bottom", {"start": v(-125.7, -1.09) * mm, "end": v(-123.07, -1.09) * mm});
            skLineSegment(sketch, "E78.top", {"start": v(-125.7, -2.59) * mm, "end": v(-123.07, -2.59) * mm});
            skLineSegment(sketch, "E78.left", {"start": v(-125.7, -1.09) * mm, "end": v(-125.7, -2.59) * mm});
            skLineSegment(sketch, "E78.right", {"start": v(-110.7, -1.09) * mm, "end": v(-110.7, -2.59) * mm});
            skLineSegment(sketch, "E79.trimOffspring", {"start": v(-123.07, -2.59) * mm, "end": v(-123.07, -10.34) * mm});
            skLineSegment(sketch, "E80.trimOffspring", {"start": v(-121.57, -2.59) * mm, "end": v(-121.57, -10.34) * mm});
            skLineSegment(sketch, "E81.trimOffspring", {"start": v(-121.57, -1.09) * mm, "end": v(-118.94, -1.09) * mm, "construction": true});
            skLineSegment(sketch, "E82.trimOffspring", {"start": v(-121.57, -2.59) * mm, "end": v(-118.94, -2.59) * mm, "construction": true});
            skLineSegment(sketch, "E83.trimOffspring", {"start": v(-121.57, -1.09) * mm, "end": v(-114.82, -1.09) * mm});
            skLineSegment(sketch, "E84.trimOffspring", {"start": v(-121.57, -2.59) * mm, "end": v(-114.82, -2.59) * mm});
            skLineSegment(sketch, "E85.trimOffspring", {"start": v(-114.82, -2.59) * mm, "end": v(-114.82, -10.34) * mm});
            skLineSegment(sketch, "E86.trimOffspring", {"start": v(-113.32, -1.09) * mm, "end": v(-109.7, -1.09) * mm, "construction": true});
            skLineSegment(sketch, "E87.trimOffspring", {"start": v(-113.32, -2.59) * mm, "end": v(-113.32, -10.34) * mm});
            skLineSegment(sketch, "E88.trimOffspring", {"start": v(-113.32, -1.09) * mm, "end": v(-110.7, -1.09) * mm});
            skLineSegment(sketch, "E89.trimOffspring", {"start": v(-113.32, -2.59) * mm, "end": v(-109.7, -2.59) * mm, "construction": true});
            skLineSegment(sketch, "E90.trimOffspring", {"start": v(-113.32, -2.59) * mm, "end": v(-110.7, -2.59) * mm});
            skLineSegment(sketch, "E91.bottom", {"start": v(-117.06, 5.6) * mm, "end": v(-111.06, 5.6) * mm, "construction": true});
            skLineSegment(sketch, "E91.top", {"start": v(-117.06, -0.4) * mm, "end": v(-111.06, -0.4) * mm, "construction": true});
            skLineSegment(sketch, "E91.left", {"start": v(-117.06, 5.6) * mm, "end": v(-117.06, -0.4) * mm, "construction": true});
            skLineSegment(sketch, "E91.right", {"start": v(-111.06, 5.6) * mm, "end": v(-111.06, -0.4) * mm, "construction": true});
            skSolve(sketch);
        }
        {
            var Q0;
            Q0=makeQuery(id+"F18.imprint","IMPRINT",FACE,{"disambiguationData":[TD([[makeQuery(id+"F18.imprint","IMPRINT",EDGE,{"derivedFrom":sQuery(id+"F18.wireOp",EDGE,"E61.bottom")}),1.0]])]});
            var Q1;
            Q1=makeQuery(id+"F18.imprint","IMPRINT",FACE,{"disambiguationData":[TD([[makeQuery(id+"F18.imprint","IMPRINT",EDGE,{"derivedFrom":sQuery(id+"F18.wireOp",EDGE,"E61.top")}),-1.0]])]});
            var Q2;
            Q2=makeQuery(id+"F18.imprint","IMPRINT",FACE,{"disambiguationData":[TD([[makeQuery(id+"F18.imprint","IMPRINT",EDGE,{"derivedFrom":sQuery(id+"F18.wireOp",EDGE,"E61.left")}),1.0]])]});
            var Q3;
            Q3=makeQuery(id+"F18.imprint","IMPRINT",FACE,{"disambiguationData":[TD([[makeQuery(id+"F18.imprint","IMPRINT",EDGE,{"derivedFrom":sQuery(id+"F18.wireOp",EDGE,"0d877499-d8d4-4159-99c7-822d795fc6ca.bottom")}),-1.0]])]});
            var Q4;
            Q4=makeQuery(id+"F18.imprint","IMPRINT",FACE,{"disambiguationData":[TD([[makeQuery(id+"F18.imprint","IMPRINT",EDGE,{"derivedFrom":sQuery(id+"F18.wireOp",EDGE,"c0df8190-0039-47ec-86a2-d0705ce6734e.bottom")}),-1.0]])]});
            var Q5;
            Q5=makeQuery(id+"F18.imprint","IMPRINT",FACE,{"disambiguationData":[TD([[makeQuery(id+"F18.imprint","IMPRINT",EDGE,{"derivedFrom":sQuery(id+"F18.wireOp",EDGE,"hlkj7elJ-mpTF-eRwW-Toyz-55aFHtf3xgrz.bottom")}),-1.0]])]});
            var Q6;
            Q6=makeQuery(id+"F18.imprint","IMPRINT",FACE,{"disambiguationData":[TD([[makeQuery(id+"F18.imprint","IMPRINT",EDGE,{"derivedFrom":sQuery(id+"F18.wireOp",EDGE,"E76.bottom")}),-1.0]])]});
            var Q7;
            Q7=makeQuery(id+"F18.imprint","IMPRINT",FACE,{"disambiguationData":[TD([[makeQuery(id+"F18.imprint","IMPRINT",EDGE,{"derivedFrom":sQuery(id+"F18.wireOp",EDGE,"E77.bottom")}),-1.0]])]});
            extrude(context, id + "F19", {"entities" : qUnion([Q0, Q1, Q2, Q3, Q4, Q5, Q6, Q7]), "depth" : 1 * mm});
        }
        {
            var Q0;
            Q0=makeQuery(id+"F19.opExtrude","CAP_FACE",FACE,{"disambiguationData":[OSD([sQuery(id+"F18.wireOp",EDGE,"E61.left"),sQuery(id+"F18.wireOp",EDGE,"E61.right"),sQuery(id+"F18.wireOp",EDGE,"E62.top"),sQuery(id+"F18.wireOp",EDGE,"E62.left"),sQuery(id+"F18.wireOp",EDGE,"E62.right"),sQuery(id+"F18.wireOp",EDGE,"E63.top"),sQuery(id+"F18.wireOp",EDGE,"E63.left"),sQuery(id+"F18.wireOp",EDGE,"E63.right"),sQuery(id+"F18.wireOp",EDGE,"E66.0"),sQuery(id+"F18.wireOp",EDGE,"E66.1"),sQuery(id+"F18.wireOp",EDGE,"E66.2"),sQuery(id+"F18.wireOp",EDGE,"E66.3"),sQuery(id+"F18.wireOp",EDGE,"0d877499-d8d4-4159-99c7-822d795fc6ca.bottom"),sQuery(id+"F18.wireOp",EDGE,"0d877499-d8d4-4159-99c7-822d795fc6ca.top"),sQuery(id+"F18.wireOp",EDGE,"c0df8190-0039-47ec-86a2-d0705ce6734e.bottom"),sQuery(id+"F18.wireOp",EDGE,"c0df8190-0039-47ec-86a2-d0705ce6734e.top"),sQuery(id+"F18.wireOp",EDGE,"E67"),sQuery(id+"F18.wireOp",EDGE,"E69"),sQuery(id+"F18.wireOp",EDGE,"hlkj7elJ-mpTF-eRwW-Toyz-55aFHtf3xgrz.left"),sQuery(id+"F18.wireOp",EDGE,"hlkj7elJ-mpTF-eRwW-Toyz-55aFHtf3xgrz.right")])],"isStart":false});
            var sketch = newSketch(context, id + "F20", { "sketchPlane" : qUnion([Q0])});
            skLineSegment(sketch, "E92.bottom", {"start": v(-118.94, -0.34) * mm, "end": v(-117.44, -0.34) * mm});
            skLineSegment(sketch, "E92.top", {"start": v(-118.94, -3.34) * mm, "end": v(-117.44, -3.34) * mm});
            skLineSegment(sketch, "E92.left", {"start": v(-118.94, -0.34) * mm, "end": v(-118.94, -3.34) * mm});
            skLineSegment(sketch, "E92.right", {"start": v(-117.44, -0.34) * mm, "end": v(-117.44, -3.34) * mm});
            skSolve(sketch);
        }
        {
            var Q0;
            {var subQ0=sQuery(id+"F20.wireOp",EDGE,"E92.left");var subQ1=makeQuery(id+"F19.opExtrude","CAP_EDGE",EDGE,{"disambiguationData":[OSD([sQuery(id+"F18.wireOp",EDGE,"E83.trimOffspring")])],"isStart":false});var subQ2=makeQuery(id+"F20.imprint","INTERSECT",VERTEX,{"derivedFrom":[subQ1,subQ0]});Q0=makeQuery(id+"F20.imprint","IMPRINT",FACE,{"disambiguationData":[TD([[makeQuery(id+"F20.imprint","IMPRINT",EDGE,{"disambiguationData":[TD([[subQ2,-1.0]])],"derivedFrom":subQ0}),1.0]])]});}
            extrude(context, id + "F21", {"entities" : qUnion([Q0]), "operationType" : NewBodyOperationType.ADD, "depth" : 3 * mm});
        }
        {
            var Q0;
            Q0=makeQuery(id+"F21.opExtrude","CAP_FACE",FACE,{"disambiguationData":[OSD([sQuery(id+"F18.wireOp",EDGE,"E83.trimOffspring"),sQuery(id+"F18.wireOp",EDGE,"E84.trimOffspring"),sQuery(id+"F20.wireOp",EDGE,"E92.left"),sQuery(id+"F20.wireOp",EDGE,"E92.right")])],"isStart":false});
            var sketch = newSketch(context, id + "F22", { "sketchPlane" : qUnion([Q0])});
            skLineSegment(sketch, "E93.bottom", {"start": v(-114.7, -5.34) * mm, "end": v(-121.7, -5.34) * mm});
            skLineSegment(sketch, "E93.top", {"start": v(-114.7, 1.66) * mm, "end": v(-121.7, 1.66) * mm});
            skLineSegment(sketch, "E93.left", {"start": v(-114.7, -5.34) * mm, "end": v(-114.7, 1.66) * mm});
            skLineSegment(sketch, "E93.right", {"start": v(-121.7, -5.34) * mm, "end": v(-121.7, 1.66) * mm});
            skPoint(sketch, "E93.middle", {"position": v(-118.2, -1.84) * mm});
            skPoint(sketch, "E93.middle.positionSnap0", {"position": v(-118.2, -1.09) * mm});
            skPoint(sketch, "E93.middle.positionSnap1", {"position": v(-118.94, -1.84) * mm});
            skPoint(sketch, "E93.centerSnap0", {"position": v(-118.2, -1.09) * mm});
            skPoint(sketch, "E93.centerSnap1", {"position": v(-118.94, -1.84) * mm});
            skSolve(sketch);
        }
        {
            var Q0;
            Q0=makeQuery(id+"F22.imprint","IMPRINT",FACE,{"disambiguationData":[TD([[makeQuery(id+"F22.imprint","IMPRINT",EDGE,{"derivedFrom":sQuery(id+"F22.wireOp",EDGE,"E93.bottom")}),-1.0]])]});
            extrude(context, id + "F23", {"entities" : qUnion([Q0]), "depth" : 9 * mm});
        }
        {
            var Q0;
            Q0=qCreatedBy(makeId("Top.planeOp"),FACE);
            var sketch = newSketch(context, id + "F24", { "sketchPlane" : qUnion([Q0])});
            skLineSegment(sketch, "E94.bottom", {"start": v(-158.05, -0.5) * mm, "end": v(-159.05, -0.5) * mm});
            skLineSegment(sketch, "E94.top", {"start": v(-158.05, 0.5) * mm, "end": v(-159.05, 0.5) * mm});
            skLineSegment(sketch, "E94.left", {"start": v(-158.05, -0.5) * mm, "end": v(-158.05, 0.5) * mm});
            skLineSegment(sketch, "E94.right", {"start": v(-159.05, -0.5) * mm, "end": v(-159.05, 0.5) * mm});
            skPoint(sketch, "E94.middle", {"position": v(-158.55, 0) * mm});
            skSolve(sketch);
        }
        {
            var Q0;
            Q0=qSketchRegion(id+"F24",true);
            extrude(context, id + "F25", {"entities" : qUnion([Q0]), "depth" : 1 * mm});
        }
        {
            var Q0;
            Q0=makeQuery(id+"F19.opExtrude","CAP_FACE",FACE,{"disambiguationData":[OSD([sQuery(id+"F18.wireOp",EDGE,"E61.left"),sQuery(id+"F18.wireOp",EDGE,"E61.right"),sQuery(id+"F18.wireOp",EDGE,"E62.top"),sQuery(id+"F18.wireOp",EDGE,"E62.left"),sQuery(id+"F18.wireOp",EDGE,"E62.right"),sQuery(id+"F18.wireOp",EDGE,"E63.top"),sQuery(id+"F18.wireOp",EDGE,"E63.left"),sQuery(id+"F18.wireOp",EDGE,"E63.right"),sQuery(id+"F18.wireOp",EDGE,"E66.0"),sQuery(id+"F18.wireOp",EDGE,"E66.1"),sQuery(id+"F18.wireOp",EDGE,"E66.2"),sQuery(id+"F18.wireOp",EDGE,"E66.3"),sQuery(id+"F18.wireOp",EDGE,"E67"),sQuery(id+"F18.wireOp",EDGE,"E69"),sQuery(id+"F18.wireOp",EDGE,"E76.left"),sQuery(id+"F18.wireOp",EDGE,"E76.right"),sQuery(id+"F18.wireOp",EDGE,"E77.left"),sQuery(id+"F18.wireOp",EDGE,"E77.right"),sQuery(id+"F18.wireOp",EDGE,"E78.bottom"),sQuery(id+"F18.wireOp",EDGE,"E78.top"),sQuery(id+"F18.wireOp",EDGE,"E79.trimOffspring"),sQuery(id+"F18.wireOp",EDGE,"E80.trimOffspring"),sQuery(id+"F18.wireOp",EDGE,"E83.trimOffspring"),sQuery(id+"F18.wireOp",EDGE,"E84.trimOffspring"),sQuery(id+"F18.wireOp",EDGE,"E85.trimOffspring"),sQuery(id+"F18.wireOp",EDGE,"E87.trimOffspring"),sQuery(id+"F18.wireOp",EDGE,"E88.trimOffspring"),sQuery(id+"F18.wireOp",EDGE,"E90.trimOffspring")])],"isStart":false});
            var sketch = newSketch(context, id + "F26", { "sketchPlane" : qUnion([Q0])});
            skPoint(sketch, "E95.firstSnap0", {"position": v(-116.13, -1.09) * mm});
            skLineSegment(sketch, "E95.bottom", {"start": v(-126.7, -1.09) * mm, "end": v(-123.07, -1.09) * mm});
            skLineSegment(sketch, "E95.top", {"start": v(-126.7, -2.59) * mm, "end": v(-123.07, -2.59) * mm});
            skLineSegment(sketch, "E95.left", {"start": v(-126.7, -1.09) * mm, "end": v(-126.7, -2.59) * mm});
            skLineSegment(sketch, "E95.right", {"start": v(-123.07, -1.09) * mm, "end": v(-123.07, -2.59) * mm});
            skLineSegment(sketch, "E96.bottom", {"start": v(-113.32, -1.09) * mm, "end": v(-109.7, -1.09) * mm});
            skLineSegment(sketch, "E96.top", {"start": v(-113.32, -2.59) * mm, "end": v(-109.7, -2.59) * mm});
            skLineSegment(sketch, "E96.left", {"start": v(-113.32, -1.09) * mm, "end": v(-113.32, -2.59) * mm});
            skLineSegment(sketch, "E96.right", {"start": v(-109.7, -1.09) * mm, "end": v(-109.7, -2.59) * mm});
            skSolve(sketch);
        }
        {
            var Q0;
            {var subQ4=sQuery(id+"F26.wireOp",EDGE,"E96.left");Q0=makeQuery(id+"F26.imprint","IMPRINT",FACE,{"disambiguationData":[TD([[makeQuery(id+"F26.imprint","IMPRINT",EDGE,{"derivedFrom":subQ4}),1.0]])]});}
            var Q1;
            {var subQ4=sQuery(id+"F26.wireOp",EDGE,"E95.left");Q1=makeQuery(id+"F26.imprint","IMPRINT",FACE,{"disambiguationData":[TD([[makeQuery(id+"F26.imprint","IMPRINT",EDGE,{"derivedFrom":subQ4}),-1.0]])]});}
            extrude(context, id + "F27", {"entities" : qUnion([Q0, Q1]), "operationType" : NewBodyOperationType.ADD, "depth" : 10 * mm});
        }
        {
            var Q0;
            Q0=qCreatedBy(makeId("Top.planeOp"),FACE);
            var sketch = newSketch(context, id + "F28", { "sketchPlane" : qUnion([Q0])});
            skLineSegment(sketch, "E97.bottom", {"start": v(-65.37, 6.18) * mm, "end": v(-48.87, 6.18) * mm});
            skLineSegment(sketch, "E97.top", {"start": v(-65.37, -10.32) * mm, "end": v(-48.87, -10.32) * mm});
            skLineSegment(sketch, "E97.left", {"start": v(-65.37, 6.18) * mm, "end": v(-65.37, -10.32) * mm});
            skLineSegment(sketch, "E97.right", {"start": v(-48.87, 6.18) * mm, "end": v(-48.87, -10.32) * mm});
            skLineSegment(sketch, "E98.left", {"start": v(-61.97, 5.28) * mm, "end": v(-61.97, -9.42) * mm});
            skLineSegment(sketch, "E98.right", {"start": v(-59.47, 5.28) * mm, "end": v(-59.47, -9.42) * mm});
            skLineSegment(sketch, "E99.left", {"start": v(-54.77, 5.28) * mm, "end": v(-54.77, -9.42) * mm});
            skLineSegment(sketch, "E99.right", {"start": v(-52.27, 5.28) * mm, "end": v(-52.27, -9.42) * mm});
            skLineSegment(sketch, "E100.bottom", {"start": v(-63.47, 4.48) * mm, "end": v(-57.47, 4.48) * mm});
            skLineSegment(sketch, "E100.top", {"start": v(-63.47, -1.52) * mm, "end": v(-57.47, -1.52) * mm});
            skLineSegment(sketch, "E100.left", {"start": v(-63.47, 4.48) * mm, "end": v(-63.47, -1.52) * mm});
            skLineSegment(sketch, "E100.right", {"start": v(-57.47, 4.48) * mm, "end": v(-57.47, -1.52) * mm});
            skLineSegment(sketch, "E101.bottom", {"start": v(-56.77, 4.48) * mm, "end": v(-50.77, 4.48) * mm});
            skLineSegment(sketch, "E101.top", {"start": v(-56.77, -1.52) * mm, "end": v(-50.77, -1.52) * mm});
            skLineSegment(sketch, "E101.left", {"start": v(-56.77, 4.48) * mm, "end": v(-56.77, -1.52) * mm});
            skLineSegment(sketch, "E101.right", {"start": v(-50.77, 4.48) * mm, "end": v(-50.77, -1.52) * mm});
            skLineSegment(sketch, "E102.bottom", {"start": v(-63.47, -2.62) * mm, "end": v(-57.47, -2.62) * mm});
            skLineSegment(sketch, "E102.top", {"start": v(-63.47, -8.62) * mm, "end": v(-57.47, -8.62) * mm});
            skLineSegment(sketch, "E102.left", {"start": v(-63.47, -2.62) * mm, "end": v(-63.47, -8.62) * mm});
            skLineSegment(sketch, "E102.right", {"start": v(-57.47, -2.62) * mm, "end": v(-57.47, -8.62) * mm});
            skLineSegment(sketch, "E103.bottom", {"start": v(-56.77, -2.62) * mm, "end": v(-50.77, -2.62) * mm});
            skLineSegment(sketch, "E103.top", {"start": v(-56.77, -8.62) * mm, "end": v(-50.77, -8.62) * mm});
            skLineSegment(sketch, "E103.left", {"start": v(-56.77, -2.62) * mm, "end": v(-56.77, -8.62) * mm});
            skLineSegment(sketch, "E103.right", {"start": v(-50.77, -2.62) * mm, "end": v(-50.77, -8.62) * mm});
            skLineSegment(sketch, "E104.top", {"start": v(-65.37, 5.28) * mm, "end": v(-48.87, 5.28) * mm});
            skLineSegment(sketch, "E104.left", {"start": v(-65.37, 6.18) * mm, "end": v(-65.37, 5.28) * mm});
            skLineSegment(sketch, "E104.right", {"start": v(-48.87, 6.18) * mm, "end": v(-48.87, 5.28) * mm});
            skLineSegment(sketch, "E105.bottom", {"start": v(-65.37, -10.32) * mm, "end": v(-54.77, -10.32) * mm});
            skLineSegment(sketch, "E105.top", {"start": v(-65.37, -9.42) * mm, "end": v(-48.87, -9.42) * mm});
            skLineSegment(sketch, "E105.left", {"start": v(-65.37, -10.32) * mm, "end": v(-65.37, -9.42) * mm});
            skLineSegment(sketch, "E105.right", {"start": v(-48.87, -10.32) * mm, "end": v(-48.87, -9.42) * mm});
            skLineSegment(sketch, "E106.bottom", {"start": v(-65.37, -9.42) * mm, "end": v(-64.47, -9.42) * mm});
            skLineSegment(sketch, "E106.top", {"start": v(-65.37, 5.28) * mm, "end": v(-64.47, 5.28) * mm});
            skLineSegment(sketch, "E106.left", {"start": v(-65.37, -9.42) * mm, "end": v(-65.37, 5.28) * mm});
            skLineSegment(sketch, "E106.right", {"start": v(-64.47, -9.42) * mm, "end": v(-64.47, 5.28) * mm});
            skLineSegment(sketch, "E107.bottom", {"start": v(-48.87, 5.28) * mm, "end": v(-49.77, 5.28) * mm});
            skLineSegment(sketch, "E107.top", {"start": v(-48.87, -9.42) * mm, "end": v(-49.77, -9.42) * mm});
            skLineSegment(sketch, "E107.left", {"start": v(-48.87, 5.28) * mm, "end": v(-48.87, -9.42) * mm});
            skLineSegment(sketch, "E107.right", {"start": v(-49.77, 5.28) * mm, "end": v(-49.77, -9.42) * mm});
            skLineSegment(sketch, "E108.trimOffspring", {"start": v(-52.27, -10.32) * mm, "end": v(-48.87, -10.32) * mm});
            skSolve(sketch);
        }
        {
            var Q0;
            Q0=makeQuery(id+"F28.imprint","IMPRINT",FACE,{"disambiguationData":[TD([[makeQuery(id+"F28.imprint","IMPRINT",EDGE,{"derivedFrom":sQuery(id+"F28.wireOp",EDGE,"E97.top")}),1.0]])]});
            var Q1;
            Q1=makeQuery(id+"F28.imprint","IMPRINT",FACE,{"disambiguationData":[TD([[makeQuery(id+"F28.imprint","IMPRINT",EDGE,{"derivedFrom":sQuery(id+"F28.wireOp",EDGE,"E106.bottom")}),1.0]])]});
            var Q2;
            Q2=makeQuery(id+"F28.imprint","IMPRINT",FACE,{"disambiguationData":[TD([[makeQuery(id+"F28.imprint","IMPRINT",EDGE,{"derivedFrom":sQuery(id+"F28.wireOp",EDGE,"E97.bottom")}),-1.0]])]});
            var Q3;
            Q3=makeQuery(id+"F28.imprint","IMPRINT",FACE,{"disambiguationData":[TD([[makeQuery(id+"F28.imprint","IMPRINT",EDGE,{"derivedFrom":sQuery(id+"F28.wireOp",EDGE,"E107.bottom")}),1.0]])]});
            var Q4;
            {var subQ0=sQuery(id+"F28.wireOp",EDGE,"E99.left");Q4=makeQuery(id+"F28.imprint","IMPRINT",FACE,{"disambiguationData":[TD([[makeQuery(id+"F28.imprint","IMPRINT",EDGE,{"derivedFrom":subQ0}),1.0]])]});}
            var Q5;
            {var subQ0=sQuery(id+"F28.wireOp",EDGE,"E98.left");Q5=makeQuery(id+"F28.imprint","IMPRINT",FACE,{"disambiguationData":[TD([[makeQuery(id+"F28.imprint","IMPRINT",EDGE,{"derivedFrom":subQ0}),1.0]])]});}
            extrude(context, id + "F29", {"entities" : qUnion([Q0, Q1, Q2, Q3, Q4, Q5]), "depth" : 1 * mm});
        }
        {
            var Q0;
            Q0=qCreatedBy(makeId("Top.planeOp"),FACE);
            var sketch = newSketch(context, id + "F30", { "sketchPlane" : qUnion([Q0])});
            skLineSegment(sketch, "E109.bottom", {"start": v(-124.98, -143.56) * mm, "end": v(-106.98, -143.56) * mm});
            skLineSegment(sketch, "E109.top", {"start": v(-124.98, -161.56) * mm, "end": v(-106.98, -161.56) * mm});
            skLineSegment(sketch, "E109.left", {"start": v(-124.98, -143.56) * mm, "end": v(-124.98, -161.56) * mm});
            skLineSegment(sketch, "E109.right", {"start": v(-106.98, -143.56) * mm, "end": v(-106.98, -161.56) * mm});
            skLineSegment(sketch, "E110.bottom", {"start": v(-116.73, -143.56) * mm, "end": v(-115.23, -143.56) * mm, "construction": true});
            skLineSegment(sketch, "E110.top", {"start": v(-116.73, -161.56) * mm, "end": v(-115.23, -161.56) * mm, "construction": true});
            skLineSegment(sketch, "E110.left", {"start": v(-116.73, -143.56) * mm, "end": v(-116.73, -151.56) * mm, "construction": true});
            skLineSegment(sketch, "E110.right", {"start": v(-115.23, -143.56) * mm, "end": v(-115.23, -151.56) * mm, "construction": true});
            skCircle(sketch, "E111", {"center": v(-115.98, -137.56) * mm, "radius": 1.5 * mm});
            skPoint(sketch, "E112", {"position": v(-115.98, -143.56) * mm});
            skCircle(sketch, "E113", {"center": v(-115.98, -167.56) * mm, "radius": 1.5 * mm});
            skLineSegment(sketch, "E114.trimOffspring", {"start": v(-115.23, -151.56) * mm, "end": v(-112.23, -151.56) * mm, "construction": true});
            skLineSegment(sketch, "E115.trimOffspring", {"start": v(-115.23, -153.56) * mm, "end": v(-112.23, -153.56) * mm, "construction": true});
            skLineSegment(sketch, "E116.trimOffspring", {"start": v(-116.73, -153.56) * mm, "end": v(-116.73, -161.56) * mm, "construction": true});
            skLineSegment(sketch, "E117.trimOffspring", {"start": v(-115.23, -153.56) * mm, "end": v(-115.23, -161.56) * mm, "construction": true});
            skLineSegment(sketch, "E118.bottom", {"start": v(-121.73, -143.56) * mm, "end": v(-119.73, -143.56) * mm});
            skLineSegment(sketch, "E118.top", {"start": v(-121.73, -161.56) * mm, "end": v(-119.73, -161.56) * mm});
            skLineSegment(sketch, "E118.left", {"start": v(-121.73, -143.56) * mm, "end": v(-121.73, -151.56) * mm});
            skLineSegment(sketch, "E118.right", {"start": v(-119.73, -143.56) * mm, "end": v(-119.73, -151.56) * mm});
            skLineSegment(sketch, "E119.bottom", {"start": v(-112.23, -143.56) * mm, "end": v(-110.23, -143.56) * mm});
            skLineSegment(sketch, "E119.top", {"start": v(-112.23, -161.56) * mm, "end": v(-110.23, -161.56) * mm});
            skLineSegment(sketch, "E119.left", {"start": v(-112.23, -143.56) * mm, "end": v(-112.23, -151.56) * mm});
            skLineSegment(sketch, "E119.right", {"start": v(-110.23, -143.56) * mm, "end": v(-110.23, -151.56) * mm});
            skLineSegment(sketch, "E120.bottom", {"start": v(-124.98, -151.56) * mm, "end": v(-121.73, -151.56) * mm});
            skLineSegment(sketch, "E120.top", {"start": v(-124.98, -153.56) * mm, "end": v(-121.73, -153.56) * mm});
            skLineSegment(sketch, "E120.left", {"start": v(-124.98, -151.56) * mm, "end": v(-124.98, -153.56) * mm});
            skLineSegment(sketch, "E120.right", {"start": v(-106.98, -151.56) * mm, "end": v(-106.98, -153.56) * mm});
            skLineSegment(sketch, "E121.trimOffspring", {"start": v(-121.73, -153.56) * mm, "end": v(-121.73, -161.56) * mm});
            skLineSegment(sketch, "E122.trimOffspring", {"start": v(-119.73, -153.56) * mm, "end": v(-119.73, -161.56) * mm});
            skLineSegment(sketch, "E123.trimOffspring", {"start": v(-119.73, -151.56) * mm, "end": v(-116.73, -151.56) * mm, "construction": true});
            skLineSegment(sketch, "E124.trimOffspring", {"start": v(-119.73, -153.56) * mm, "end": v(-116.73, -153.56) * mm, "construction": true});
            skLineSegment(sketch, "E125.trimOffspring", {"start": v(-119.73, -151.56) * mm, "end": v(-112.23, -151.56) * mm});
            skLineSegment(sketch, "E126.trimOffspring", {"start": v(-119.73, -153.56) * mm, "end": v(-112.23, -153.56) * mm});
            skLineSegment(sketch, "E127.trimOffspring", {"start": v(-112.23, -153.56) * mm, "end": v(-112.23, -161.56) * mm});
            skLineSegment(sketch, "E128.trimOffspring", {"start": v(-110.23, -153.56) * mm, "end": v(-110.23, -161.56) * mm});
            skLineSegment(sketch, "E129.trimOffspring", {"start": v(-110.23, -151.56) * mm, "end": v(-106.98, -151.56) * mm});
            skLineSegment(sketch, "E130.trimOffspring", {"start": v(-110.23, -153.56) * mm, "end": v(-106.98, -153.56) * mm});
            skLineSegment(sketch, "E131.bottom", {"start": v(-94.98, -143.56) * mm, "end": v(-76.98, -143.56) * mm});
            skLineSegment(sketch, "E131.top", {"start": v(-94.98, -161.56) * mm, "end": v(-76.98, -161.56) * mm});
            skLineSegment(sketch, "E131.left", {"start": v(-94.98, -143.56) * mm, "end": v(-94.98, -161.56) * mm});
            skLineSegment(sketch, "E131.right", {"start": v(-76.98, -143.56) * mm, "end": v(-76.98, -161.56) * mm});
            skLineSegment(sketch, "E132.bottom", {"start": v(-86.73, -143.56) * mm, "end": v(-85.23, -143.56) * mm, "construction": true});
            skLineSegment(sketch, "E132.top", {"start": v(-86.73, -161.56) * mm, "end": v(-85.23, -161.56) * mm, "construction": true});
            skLineSegment(sketch, "E132.left", {"start": v(-86.73, -143.56) * mm, "end": v(-86.73, -151.56) * mm, "construction": true});
            skLineSegment(sketch, "E132.right", {"start": v(-85.23, -143.56) * mm, "end": v(-85.23, -151.56) * mm, "construction": true});
            skLineSegment(sketch, "E133.bottom", {"start": v(-94.98, -151.56) * mm, "end": v(-91.73, -151.56) * mm, "construction": true});
            skLineSegment(sketch, "E133.top", {"start": v(-94.98, -153.56) * mm, "end": v(-91.73, -153.56) * mm, "construction": true});
            skLineSegment(sketch, "E133.left", {"start": v(-94.98, -151.56) * mm, "end": v(-94.98, -153.56) * mm, "construction": true});
            skLineSegment(sketch, "E133.right", {"start": v(-76.98, -151.56) * mm, "end": v(-76.98, -153.56) * mm, "construction": true});
            skCircle(sketch, "E134", {"center": v(-85.98, -137.56) * mm, "radius": 1.5 * mm});
            skPoint(sketch, "E135", {"position": v(-85.98, -143.56) * mm});
            skCircle(sketch, "E136", {"center": v(-85.98, -167.56) * mm, "radius": 1.5 * mm});
            skLineSegment(sketch, "E137.trimOffspring", {"start": v(-85.23, -151.56) * mm, "end": v(-82.23, -151.56) * mm, "construction": true});
            skLineSegment(sketch, "E138.trimOffspring", {"start": v(-85.23, -153.56) * mm, "end": v(-82.23, -153.56) * mm, "construction": true});
            skLineSegment(sketch, "E139.trimOffspring", {"start": v(-86.73, -153.56) * mm, "end": v(-86.73, -161.56) * mm, "construction": true});
            skLineSegment(sketch, "E140.trimOffspring", {"start": v(-85.23, -153.56) * mm, "end": v(-85.23, -161.56) * mm, "construction": true});
            skLineSegment(sketch, "E141.bottom", {"start": v(-91.73, -143.56) * mm, "end": v(-89.73, -143.56) * mm});
            skLineSegment(sketch, "E141.top", {"start": v(-91.73, -161.56) * mm, "end": v(-89.73, -161.56) * mm});
            skLineSegment(sketch, "E141.left", {"start": v(-91.73, -143.56) * mm, "end": v(-91.73, -151.56) * mm});
            skLineSegment(sketch, "E141.right", {"start": v(-89.73, -143.56) * mm, "end": v(-89.73, -151.56) * mm});
            skLineSegment(sketch, "E142.bottom", {"start": v(-82.23, -143.56) * mm, "end": v(-80.23, -143.56) * mm});
            skLineSegment(sketch, "E142.top", {"start": v(-82.23, -161.56) * mm, "end": v(-80.23, -161.56) * mm});
            skLineSegment(sketch, "E142.left", {"start": v(-82.23, -143.56) * mm, "end": v(-82.23, -151.56) * mm});
            skLineSegment(sketch, "E142.right", {"start": v(-80.23, -143.56) * mm, "end": v(-80.23, -151.56) * mm});
            skLineSegment(sketch, "E143.bottom", {"start": v(-94.98, -151.56) * mm, "end": v(-91.73, -151.56) * mm});
            skLineSegment(sketch, "E143.top", {"start": v(-94.98, -153.56) * mm, "end": v(-91.73, -153.56) * mm});
            skLineSegment(sketch, "E143.left", {"start": v(-94.98, -151.56) * mm, "end": v(-94.98, -153.56) * mm});
            skLineSegment(sketch, "E143.right", {"start": v(-76.98, -151.56) * mm, "end": v(-76.98, -153.56) * mm});
            skLineSegment(sketch, "E144.trimOffspring", {"start": v(-91.73, -153.56) * mm, "end": v(-91.73, -161.56) * mm});
            skLineSegment(sketch, "E145.trimOffspring", {"start": v(-89.73, -153.56) * mm, "end": v(-89.73, -161.56) * mm});
            skLineSegment(sketch, "E146.trimOffspring", {"start": v(-89.73, -151.56) * mm, "end": v(-86.73, -151.56) * mm, "construction": true});
            skLineSegment(sketch, "E147.trimOffspring", {"start": v(-89.73, -153.56) * mm, "end": v(-86.73, -153.56) * mm, "construction": true});
            skLineSegment(sketch, "E148.trimOffspring", {"start": v(-89.73, -151.56) * mm, "end": v(-82.23, -151.56) * mm});
            skLineSegment(sketch, "E149.trimOffspring", {"start": v(-89.73, -153.56) * mm, "end": v(-82.23, -153.56) * mm});
            skLineSegment(sketch, "E150.trimOffspring", {"start": v(-82.23, -153.56) * mm, "end": v(-82.23, -161.56) * mm});
            skLineSegment(sketch, "E151.trimOffspring", {"start": v(-80.23, -151.56) * mm, "end": v(-76.98, -151.56) * mm, "construction": true});
            skLineSegment(sketch, "E152.trimOffspring", {"start": v(-80.23, -153.56) * mm, "end": v(-80.23, -161.56) * mm});
            skLineSegment(sketch, "E153.trimOffspring", {"start": v(-80.23, -151.56) * mm, "end": v(-76.98, -151.56) * mm});
            skLineSegment(sketch, "E154.trimOffspring", {"start": v(-80.23, -153.56) * mm, "end": v(-76.98, -153.56) * mm, "construction": true});
            skLineSegment(sketch, "E155.trimOffspring", {"start": v(-80.23, -153.56) * mm, "end": v(-76.98, -153.56) * mm});
            skLineSegment(sketch, "E156.bottom", {"start": v(-64.98, -143.56) * mm, "end": v(-46.98, -143.56) * mm});
            skLineSegment(sketch, "E156.top", {"start": v(-64.98, -161.56) * mm, "end": v(-46.98, -161.56) * mm});
            skLineSegment(sketch, "E156.left", {"start": v(-64.98, -143.56) * mm, "end": v(-64.98, -161.56) * mm});
            skLineSegment(sketch, "E156.right", {"start": v(-46.98, -143.56) * mm, "end": v(-46.98, -161.56) * mm});
            skLineSegment(sketch, "E157.bottom", {"start": v(-64.98, -161.56) * mm, "end": v(-47.98, -161.56) * mm});
            skLineSegment(sketch, "E158.bottom", {"start": v(-56.73, -143.56) * mm, "end": v(-55.23, -143.56) * mm, "construction": true});
            skLineSegment(sketch, "E158.top", {"start": v(-56.73, -161.56) * mm, "end": v(-55.23, -161.56) * mm, "construction": true});
            skLineSegment(sketch, "E158.left", {"start": v(-56.73, -143.56) * mm, "end": v(-56.73, -151.56) * mm, "construction": true});
            skLineSegment(sketch, "E158.right", {"start": v(-55.23, -143.56) * mm, "end": v(-55.23, -151.56) * mm, "construction": true});
            skLineSegment(sketch, "E159.bottom", {"start": v(-64.98, -151.56) * mm, "end": v(-61.73, -151.56) * mm, "construction": true});
            skLineSegment(sketch, "E159.top", {"start": v(-64.98, -153.56) * mm, "end": v(-61.73, -153.56) * mm, "construction": true});
            skLineSegment(sketch, "E159.left", {"start": v(-64.98, -151.56) * mm, "end": v(-64.98, -153.56) * mm, "construction": true});
            skLineSegment(sketch, "E159.right", {"start": v(-46.98, -151.56) * mm, "end": v(-46.98, -153.56) * mm, "construction": true});
            skCircle(sketch, "E160", {"center": v(-55.98, -137.56) * mm, "radius": 1.5 * mm});
            skPoint(sketch, "E161", {"position": v(-55.98, -143.56) * mm});
            skCircle(sketch, "E162", {"center": v(-55.98, -167.56) * mm, "radius": 1.5 * mm});
            skLineSegment(sketch, "E163.trimOffspring", {"start": v(-55.23, -151.56) * mm, "end": v(-52.23, -151.56) * mm, "construction": true});
            skLineSegment(sketch, "E164.trimOffspring", {"start": v(-55.23, -153.56) * mm, "end": v(-52.23, -153.56) * mm, "construction": true});
            skLineSegment(sketch, "E165.trimOffspring", {"start": v(-56.73, -153.56) * mm, "end": v(-56.73, -161.56) * mm, "construction": true});
            skLineSegment(sketch, "E166.trimOffspring", {"start": v(-55.23, -153.56) * mm, "end": v(-55.23, -161.56) * mm, "construction": true});
            skLineSegment(sketch, "E167.bottom", {"start": v(-61.73, -143.56) * mm, "end": v(-59.73, -143.56) * mm});
            skLineSegment(sketch, "E167.top", {"start": v(-61.73, -161.56) * mm, "end": v(-59.73, -161.56) * mm});
            skLineSegment(sketch, "E167.left", {"start": v(-61.73, -143.56) * mm, "end": v(-61.73, -151.56) * mm});
            skLineSegment(sketch, "E167.right", {"start": v(-59.73, -143.56) * mm, "end": v(-59.73, -151.56) * mm});
            skLineSegment(sketch, "E168.bottom", {"start": v(-52.23, -143.56) * mm, "end": v(-50.23, -143.56) * mm});
            skLineSegment(sketch, "E168.top", {"start": v(-52.23, -161.56) * mm, "end": v(-50.23, -161.56) * mm});
            skLineSegment(sketch, "E168.left", {"start": v(-52.23, -143.56) * mm, "end": v(-52.23, -151.56) * mm});
            skLineSegment(sketch, "E168.right", {"start": v(-50.23, -143.56) * mm, "end": v(-50.23, -151.56) * mm});
            skLineSegment(sketch, "E169.bottom", {"start": v(-64.98, -151.56) * mm, "end": v(-61.73, -151.56) * mm});
            skLineSegment(sketch, "E169.top", {"start": v(-64.98, -153.56) * mm, "end": v(-61.73, -153.56) * mm});
            skLineSegment(sketch, "E169.left", {"start": v(-64.98, -151.56) * mm, "end": v(-64.98, -153.56) * mm});
            skLineSegment(sketch, "E169.right", {"start": v(-46.98, -151.56) * mm, "end": v(-46.98, -153.56) * mm});
            skLineSegment(sketch, "E170.trimOffspring", {"start": v(-61.73, -153.56) * mm, "end": v(-61.73, -161.56) * mm});
            skLineSegment(sketch, "E171.trimOffspring", {"start": v(-59.73, -153.56) * mm, "end": v(-59.73, -161.56) * mm});
            skLineSegment(sketch, "E172.trimOffspring", {"start": v(-59.73, -151.56) * mm, "end": v(-56.73, -151.56) * mm, "construction": true});
            skLineSegment(sketch, "E173.trimOffspring", {"start": v(-59.73, -153.56) * mm, "end": v(-56.73, -153.56) * mm, "construction": true});
            skLineSegment(sketch, "E174.trimOffspring", {"start": v(-59.73, -151.56) * mm, "end": v(-52.23, -151.56) * mm});
            skLineSegment(sketch, "E175.trimOffspring", {"start": v(-59.73, -153.56) * mm, "end": v(-52.23, -153.56) * mm});
            skLineSegment(sketch, "E176.trimOffspring", {"start": v(-52.23, -153.56) * mm, "end": v(-52.23, -161.56) * mm});
            skLineSegment(sketch, "E177.trimOffspring", {"start": v(-50.23, -151.56) * mm, "end": v(-46.98, -151.56) * mm, "construction": true});
            skLineSegment(sketch, "E178.trimOffspring", {"start": v(-50.23, -153.56) * mm, "end": v(-50.23, -161.56) * mm});
            skLineSegment(sketch, "E179.trimOffspring", {"start": v(-50.23, -151.56) * mm, "end": v(-46.98, -151.56) * mm});
            skLineSegment(sketch, "E180.trimOffspring", {"start": v(-50.23, -153.56) * mm, "end": v(-46.98, -153.56) * mm, "construction": true});
            skLineSegment(sketch, "E181.trimOffspring", {"start": v(-50.23, -153.56) * mm, "end": v(-46.98, -153.56) * mm});
            skLineSegment(sketch, "E182.bottom", {"start": v(-34.98, -143.56) * mm, "end": v(-16.98, -143.56) * mm});
            skLineSegment(sketch, "E182.top", {"start": v(-34.98, -161.56) * mm, "end": v(-16.98, -161.56) * mm});
            skLineSegment(sketch, "E182.left", {"start": v(-34.98, -143.56) * mm, "end": v(-34.98, -161.56) * mm});
            skLineSegment(sketch, "E182.right", {"start": v(-16.98, -143.56) * mm, "end": v(-16.98, -161.56) * mm});
            skLineSegment(sketch, "E183.bottom", {"start": v(-34.98, -161.56) * mm, "end": v(-17.98, -161.56) * mm});
            skLineSegment(sketch, "E184.bottom", {"start": v(-26.73, -143.56) * mm, "end": v(-25.23, -143.56) * mm, "construction": true});
            skLineSegment(sketch, "E184.top", {"start": v(-26.73, -161.56) * mm, "end": v(-25.23, -161.56) * mm, "construction": true});
            skLineSegment(sketch, "E184.left", {"start": v(-26.73, -143.56) * mm, "end": v(-26.73, -151.56) * mm, "construction": true});
            skLineSegment(sketch, "E184.right", {"start": v(-25.23, -143.56) * mm, "end": v(-25.23, -151.56) * mm, "construction": true});
            skLineSegment(sketch, "E185.bottom", {"start": v(-34.98, -151.56) * mm, "end": v(-31.73, -151.56) * mm, "construction": true});
            skLineSegment(sketch, "E185.top", {"start": v(-34.98, -153.56) * mm, "end": v(-31.73, -153.56) * mm, "construction": true});
            skLineSegment(sketch, "E185.left", {"start": v(-34.98, -151.56) * mm, "end": v(-34.98, -153.56) * mm, "construction": true});
            skLineSegment(sketch, "E185.right", {"start": v(-16.98, -151.56) * mm, "end": v(-16.98, -153.56) * mm, "construction": true});
            skCircle(sketch, "E186", {"center": v(-25.98, -137.56) * mm, "radius": 1.5 * mm});
            skPoint(sketch, "E187", {"position": v(-25.98, -143.56) * mm});
            skCircle(sketch, "E188", {"center": v(-25.98, -167.56) * mm, "radius": 1.5 * mm});
            skLineSegment(sketch, "E189.trimOffspring", {"start": v(-25.23, -151.56) * mm, "end": v(-22.23, -151.56) * mm, "construction": true});
            skLineSegment(sketch, "E190.trimOffspring", {"start": v(-25.23, -153.56) * mm, "end": v(-22.23, -153.56) * mm, "construction": true});
            skLineSegment(sketch, "E191.trimOffspring", {"start": v(-26.73, -153.56) * mm, "end": v(-26.73, -161.56) * mm, "construction": true});
            skLineSegment(sketch, "E192.trimOffspring", {"start": v(-25.23, -153.56) * mm, "end": v(-25.23, -161.56) * mm, "construction": true});
            skLineSegment(sketch, "E193.bottom", {"start": v(-31.73, -143.56) * mm, "end": v(-29.73, -143.56) * mm});
            skLineSegment(sketch, "E193.top", {"start": v(-31.73, -161.56) * mm, "end": v(-29.73, -161.56) * mm});
            skLineSegment(sketch, "E193.left", {"start": v(-31.73, -143.56) * mm, "end": v(-31.73, -151.56) * mm});
            skLineSegment(sketch, "E193.right", {"start": v(-29.73, -143.56) * mm, "end": v(-29.73, -151.56) * mm});
            skLineSegment(sketch, "E194.bottom", {"start": v(-22.23, -143.56) * mm, "end": v(-20.23, -143.56) * mm});
            skLineSegment(sketch, "E194.top", {"start": v(-22.23, -161.56) * mm, "end": v(-20.23, -161.56) * mm});
            skLineSegment(sketch, "E194.left", {"start": v(-22.23, -143.56) * mm, "end": v(-22.23, -151.56) * mm});
            skLineSegment(sketch, "E194.right", {"start": v(-20.23, -143.56) * mm, "end": v(-20.23, -151.56) * mm});
            skLineSegment(sketch, "E195.bottom", {"start": v(-34.98, -151.56) * mm, "end": v(-31.73, -151.56) * mm});
            skLineSegment(sketch, "E195.top", {"start": v(-34.98, -153.56) * mm, "end": v(-31.73, -153.56) * mm});
            skLineSegment(sketch, "E195.left", {"start": v(-34.98, -151.56) * mm, "end": v(-34.98, -153.56) * mm});
            skLineSegment(sketch, "E195.right", {"start": v(-16.98, -151.56) * mm, "end": v(-16.98, -153.56) * mm});
            skLineSegment(sketch, "E196.trimOffspring", {"start": v(-31.73, -153.56) * mm, "end": v(-31.73, -161.56) * mm});
            skLineSegment(sketch, "E197.trimOffspring", {"start": v(-29.73, -153.56) * mm, "end": v(-29.73, -161.56) * mm});
            skLineSegment(sketch, "E198.trimOffspring", {"start": v(-29.73, -151.56) * mm, "end": v(-26.73, -151.56) * mm, "construction": true});
            skLineSegment(sketch, "E199.trimOffspring", {"start": v(-29.73, -153.56) * mm, "end": v(-26.73, -153.56) * mm, "construction": true});
            skLineSegment(sketch, "E200.trimOffspring", {"start": v(-29.73, -151.56) * mm, "end": v(-22.23, -151.56) * mm});
            skLineSegment(sketch, "E201.trimOffspring", {"start": v(-29.73, -153.56) * mm, "end": v(-22.23, -153.56) * mm});
            skLineSegment(sketch, "E202.trimOffspring", {"start": v(-22.23, -153.56) * mm, "end": v(-22.23, -161.56) * mm});
            skLineSegment(sketch, "E203.trimOffspring", {"start": v(-20.23, -151.56) * mm, "end": v(-16.98, -151.56) * mm, "construction": true});
            skLineSegment(sketch, "E204.trimOffspring", {"start": v(-20.23, -153.56) * mm, "end": v(-20.23, -161.56) * mm});
            skLineSegment(sketch, "E205.trimOffspring", {"start": v(-20.23, -151.56) * mm, "end": v(-16.98, -151.56) * mm});
            skLineSegment(sketch, "E206.trimOffspring", {"start": v(-20.23, -153.56) * mm, "end": v(-16.98, -153.56) * mm, "construction": true});
            skLineSegment(sketch, "E207.trimOffspring", {"start": v(-20.23, -153.56) * mm, "end": v(-16.98, -153.56) * mm});
            skLineSegment(sketch, "E208.bottom", {"start": v(-129.58, -134.06) * mm, "end": v(-12.58, -134.06) * mm});
            skLineSegment(sketch, "E208.top", {"start": v(-129.58, -171.06) * mm, "end": v(-12.58, -171.06) * mm});
            skLineSegment(sketch, "E208.left", {"start": v(-129.58, -134.06) * mm, "end": v(-129.58, -171.06) * mm});
            skLineSegment(sketch, "E208.right", {"start": v(-12.58, -134.06) * mm, "end": v(-12.58, -171.06) * mm});
            skSolve(sketch);
        }
        {
            var Q0;
            Q0=makeQuery(id+"F30.imprint","IMPRINT",FACE,{"disambiguationData":[TD([[makeQuery(id+"F30.imprint","IMPRINT",EDGE,{"derivedFrom":sQuery(id+"F30.wireOp",EDGE,"E111")}),-1.0]])]});
            var Q1;
            Q1=makeQuery(id+"F30.imprint","IMPRINT",FACE,{"disambiguationData":[TD([[makeQuery(id+"F30.imprint","IMPRINT",EDGE,{"derivedFrom":sQuery(id+"F30.wireOp",EDGE,"E118.bottom")}),-1.0]])]});
            var Q2;
            Q2=makeQuery(id+"F30.imprint","IMPRINT",FACE,{"disambiguationData":[TD([[makeQuery(id+"F30.imprint","IMPRINT",EDGE,{"derivedFrom":sQuery(id+"F30.wireOp",EDGE,"E141.bottom")}),-1.0]])]});
            var Q3;
            Q3=makeQuery(id+"F30.imprint","IMPRINT",FACE,{"disambiguationData":[TD([[makeQuery(id+"F30.imprint","IMPRINT",EDGE,{"derivedFrom":sQuery(id+"F30.wireOp",EDGE,"E167.bottom")}),-1.0]])]});
            var Q4;
            Q4=makeQuery(id+"F30.imprint","IMPRINT",FACE,{"disambiguationData":[TD([[makeQuery(id+"F30.imprint","IMPRINT",EDGE,{"derivedFrom":sQuery(id+"F30.wireOp",EDGE,"E193.bottom")}),-1.0]])]});
            extrude(context, id + "F31", {"entities" : qUnion([Q0, Q1, Q2, Q3, Q4]), "depth" : 1 * mm});
        }
        {
            var Q0;
            Q0=qCreatedBy(makeId("Top.planeOp"),FACE);
            var sketch = newSketch(context, id + "F32", { "sketchPlane" : qUnion([Q0])});
            skLineSegment(sketch, "E209.bottom", {"start": v(15.66, -134.86) * mm, "end": v(137.66, -134.86) * mm});
            skLineSegment(sketch, "E209.top", {"start": v(15.66, -174.06) * mm, "end": v(137.66, -174.06) * mm});
            skLineSegment(sketch, "E209.left", {"start": v(15.66, -134.86) * mm, "end": v(15.66, -174.06) * mm});
            skLineSegment(sketch, "E209.right", {"start": v(137.66, -134.86) * mm, "end": v(137.66, -174.06) * mm});
            skLineSegment(sketch, "E210.bottom", {"start": v(22.06, -144.26) * mm, "end": v(42.46, -144.26) * mm});
            skLineSegment(sketch, "E210.top", {"start": v(22.06, -164.66) * mm, "end": v(42.46, -164.66) * mm});
            skLineSegment(sketch, "E210.left", {"start": v(22.06, -144.26) * mm, "end": v(22.06, -164.66) * mm});
            skLineSegment(sketch, "E210.right", {"start": v(42.46, -144.26) * mm, "end": v(42.46, -164.66) * mm});
            skCircle(sketch, "E211", {"center": v(31.96, -139.46) * mm, "radius": 1.5 * mm, "construction": true});
            skCircle(sketch, "E212", {"center": v(31.96, -169.46) * mm, "radius": 1.5 * mm, "construction": true});
            skLineSegment(sketch, "E213.bottom", {"start": v(52.16, -144.36) * mm, "end": v(72.36, -144.36) * mm});
            skLineSegment(sketch, "E213.top", {"start": v(52.16, -164.56) * mm, "end": v(72.36, -164.56) * mm});
            skLineSegment(sketch, "E213.left", {"start": v(52.16, -144.36) * mm, "end": v(52.16, -164.56) * mm});
            skLineSegment(sketch, "E213.right", {"start": v(72.36, -144.36) * mm, "end": v(72.36, -164.56) * mm});
            skCircle(sketch, "E214", {"center": v(62.26, -139.46) * mm, "radius": 1.5 * mm, "construction": true});
            skCircle(sketch, "E215", {"center": v(62.26, -169.46) * mm, "radius": 1.5 * mm, "construction": true});
            skLineSegment(sketch, "E216.bottom", {"start": v(82.16, -144.36) * mm, "end": v(102.36, -144.36) * mm});
            skLineSegment(sketch, "E216.top", {"start": v(82.16, -164.56) * mm, "end": v(102.36, -164.56) * mm});
            skLineSegment(sketch, "E216.left", {"start": v(82.16, -144.36) * mm, "end": v(82.16, -164.56) * mm});
            skLineSegment(sketch, "E216.right", {"start": v(102.36, -144.36) * mm, "end": v(102.36, -164.56) * mm});
            skCircle(sketch, "E217", {"center": v(92.26, -139.46) * mm, "radius": 1.5 * mm, "construction": true});
            skCircle(sketch, "E218", {"center": v(92.26, -169.46) * mm, "radius": 1.5 * mm, "construction": true});
            skPoint(sketch, "E218.centerSnap0", {"position": v(92.26, -164.56) * mm});
            skLineSegment(sketch, "E219.bottom", {"start": v(112.16, -144.36) * mm, "end": v(132.36, -144.36) * mm});
            skLineSegment(sketch, "E219.top", {"start": v(112.16, -164.56) * mm, "end": v(132.36, -164.56) * mm});
            skLineSegment(sketch, "E219.left", {"start": v(112.16, -144.36) * mm, "end": v(112.16, -164.56) * mm});
            skLineSegment(sketch, "E219.right", {"start": v(132.36, -144.36) * mm, "end": v(132.36, -164.56) * mm});
            skCircle(sketch, "E220", {"center": v(122.26, -139.46) * mm, "radius": 1.5 * mm, "construction": true});
            skCircle(sketch, "E221", {"center": v(122.26, -169.46) * mm, "radius": 1.5 * mm, "construction": true});
            skLineSegment(sketch, "E222.bottom", {"start": v(23.26, -145.46) * mm, "end": v(41.26, -145.46) * mm, "construction": true});
            skLineSegment(sketch, "E222.top", {"start": v(23.26, -163.46) * mm, "end": v(41.26, -163.46) * mm, "construction": true});
            skLineSegment(sketch, "E222.left", {"start": v(23.26, -145.46) * mm, "end": v(23.26, -163.46) * mm, "construction": true});
            skLineSegment(sketch, "E222.right", {"start": v(41.26, -145.46) * mm, "end": v(41.26, -163.46) * mm, "construction": true});
            skSolve(sketch);
        }
        {
            var Q0;
            Q0=qSketchRegion(id+"F32",true);
            extrude(context, id + "F33", {"entities" : qUnion([Q0]), "depth" : 11 * mm});
        }
        {
            var Q0;
            Q0=makeQuery(id+"F33.opExtrude","CAP_FACE",FACE,{"disambiguationData":[OSD([sQuery(id+"F32.wireOp",EDGE,"E209.bottom"),sQuery(id+"F32.wireOp",EDGE,"E209.top"),sQuery(id+"F32.wireOp",EDGE,"E209.left"),sQuery(id+"F32.wireOp",EDGE,"E209.right")])],"isStart":true});
            var sketch = newSketch(context, id + "F34", { "sketchPlane" : qUnion([Q0])});
            skLineSegment(sketch, "E223.bottom", {"start": v(16.66, 173.06) * mm, "end": v(136.66, 173.06) * mm});
            skLineSegment(sketch, "E223.top", {"start": v(16.66, 135.86) * mm, "end": v(136.66, 135.86) * mm});
            skLineSegment(sketch, "E223.left", {"start": v(16.66, 173.06) * mm, "end": v(16.66, 135.86) * mm});
            skLineSegment(sketch, "E223.right", {"start": v(136.66, 173.06) * mm, "end": v(136.66, 135.86) * mm});
            skSolve(sketch);
        }
        {
            var Q0;
            Q0=qSketchRegion(id+"F34",true);
            extrude(context, id + "F35", {"entities" : qUnion([Q0]), "operationType" : NewBodyOperationType.REMOVE, "oppositeDirection" : true, "depth" : 8 * mm});
        }
        {
            var Q0;
            Q0=makeQuery(id+"F31.opExtrude","CAP_FACE",FACE,{"disambiguationData":[OSD([sQuery(id+"F30.wireOp",EDGE,"55227c07-3752-4080-a22d-609154aa437d.0"),sQuery(id+"F30.wireOp",EDGE,"55227c07-3752-4080-a22d-609154aa437d.1"),sQuery(id+"F30.wireOp",EDGE,"55227c07-3752-4080-a22d-609154aa437d.2"),sQuery(id+"F30.wireOp",EDGE,"55227c07-3752-4080-a22d-609154aa437d.3"),sQuery(id+"F30.wireOp",EDGE,"E111"),sQuery(id+"F30.wireOp",EDGE,"E113"),sQuery(id+"F30.wireOp",EDGE,"E118.left"),sQuery(id+"F30.wireOp",EDGE,"E118.right"),sQuery(id+"F30.wireOp",EDGE,"E119.left"),sQuery(id+"F30.wireOp",EDGE,"E119.right"),sQuery(id+"F30.wireOp",EDGE,"E120.bottom"),sQuery(id+"F30.wireOp",EDGE,"E120.top"),sQuery(id+"F30.wireOp",EDGE,"E121.trimOffspring"),sQuery(id+"F30.wireOp",EDGE,"E122.trimOffspring"),sQuery(id+"F30.wireOp",EDGE,"E125.trimOffspring"),sQuery(id+"F30.wireOp",EDGE,"E126.trimOffspring"),sQuery(id+"F30.wireOp",EDGE,"E127.trimOffspring"),sQuery(id+"F30.wireOp",EDGE,"E128.trimOffspring"),sQuery(id+"F30.wireOp",EDGE,"E129.trimOffspring"),sQuery(id+"F30.wireOp",EDGE,"E130.trimOffspring"),sQuery(id+"F30.wireOp",EDGE,"E131.bottom"),sQuery(id+"F30.wireOp",EDGE,"E131.left"),sQuery(id+"F30.wireOp",EDGE,"E131.top"),sQuery(id+"F30.wireOp",EDGE,"E131.right"),sQuery(id+"F30.wireOp",EDGE,"E134"),sQuery(id+"F30.wireOp",EDGE,"E136"),sQuery(id+"F30.wireOp",EDGE,"E141.left"),sQuery(id+"F30.wireOp",EDGE,"E141.right"),sQuery(id+"F30.wireOp",EDGE,"E142.left"),sQuery(id+"F30.wireOp",EDGE,"E142.right"),sQuery(id+"F30.wireOp",EDGE,"E143.bottom"),sQuery(id+"F30.wireOp",EDGE,"E143.top"),sQuery(id+"F30.wireOp",EDGE,"E144.trimOffspring"),sQuery(id+"F30.wireOp",EDGE,"E145.trimOffspring"),sQuery(id+"F30.wireOp",EDGE,"E148.trimOffspring"),sQuery(id+"F30.wireOp",EDGE,"E149.trimOffspring"),sQuery(id+"F30.wireOp",EDGE,"E150.trimOffspring"),sQuery(id+"F30.wireOp",EDGE,"E152.trimOffspring"),sQuery(id+"F30.wireOp",EDGE,"E153.trimOffspring"),sQuery(id+"F30.wireOp",EDGE,"E155.trimOffspring"),sQuery(id+"F30.wireOp",EDGE,"E156.bottom"),sQuery(id+"F30.wireOp",EDGE,"E156.left"),sQuery(id+"F30.wireOp",EDGE,"E156.top"),sQuery(id+"F30.wireOp",EDGE,"E156.right"),sQuery(id+"F30.wireOp",EDGE,"E160"),sQuery(id+"F30.wireOp",EDGE,"E162"),sQuery(id+"F30.wireOp",EDGE,"E167.left"),sQuery(id+"F30.wireOp",EDGE,"E167.right"),sQuery(id+"F30.wireOp",EDGE,"E168.left"),sQuery(id+"F30.wireOp",EDGE,"E168.right"),sQuery(id+"F30.wireOp",EDGE,"E169.bottom"),sQuery(id+"F30.wireOp",EDGE,"E169.top"),sQuery(id+"F30.wireOp",EDGE,"E170.trimOffspring"),sQuery(id+"F30.wireOp",EDGE,"E171.trimOffspring"),sQuery(id+"F30.wireOp",EDGE,"E174.trimOffspring"),sQuery(id+"F30.wireOp",EDGE,"E175.trimOffspring"),sQuery(id+"F30.wireOp",EDGE,"E176.trimOffspring"),sQuery(id+"F30.wireOp",EDGE,"E178.trimOffspring"),sQuery(id+"F30.wireOp",EDGE,"E179.trimOffspring"),sQuery(id+"F30.wireOp",EDGE,"E181.trimOffspring"),sQuery(id+"F30.wireOp",EDGE,"E182.bottom"),sQuery(id+"F30.wireOp",EDGE,"E182.left"),sQuery(id+"F30.wireOp",EDGE,"E182.top"),sQuery(id+"F30.wireOp",EDGE,"E182.right"),sQuery(id+"F30.wireOp",EDGE,"E186"),sQuery(id+"F30.wireOp",EDGE,"E188"),sQuery(id+"F30.wireOp",EDGE,"E193.left"),sQuery(id+"F30.wireOp",EDGE,"E193.right"),sQuery(id+"F30.wireOp",EDGE,"E194.left"),sQuery(id+"F30.wireOp",EDGE,"E194.right"),sQuery(id+"F30.wireOp",EDGE,"E195.bottom"),sQuery(id+"F30.wireOp",EDGE,"E195.top"),sQuery(id+"F30.wireOp",EDGE,"E196.trimOffspring"),sQuery(id+"F30.wireOp",EDGE,"E197.trimOffspring"),sQuery(id+"F30.wireOp",EDGE,"E200.trimOffspring"),sQuery(id+"F30.wireOp",EDGE,"E201.trimOffspring"),sQuery(id+"F30.wireOp",EDGE,"E202.trimOffspring"),sQuery(id+"F30.wireOp",EDGE,"E204.trimOffspring"),sQuery(id+"F30.wireOp",EDGE,"E205.trimOffspring"),sQuery(id+"F30.wireOp",EDGE,"E207.trimOffspring"),sQuery(id+"F30.wireOp",EDGE,"E208.bottom"),sQuery(id+"F30.wireOp",EDGE,"E208.top"),sQuery(id+"F30.wireOp",EDGE,"E208.left"),sQuery(id+"F30.wireOp",EDGE,"E208.right")])],"isStart":false});
            var sketch = newSketch(context, id + "F36", { "sketchPlane" : qUnion([Q0])});
            skLineSegment(sketch, "E224.bottom", {"start": v(-94.98, -143.56) * mm, "end": v(-98.98, -143.56) * mm});
            skLineSegment(sketch, "E224.top", {"start": v(-94.98, -161.56) * mm, "end": v(-98.98, -161.56) * mm});
            skLineSegment(sketch, "E224.left", {"start": v(-94.98, -143.56) * mm, "end": v(-94.98, -161.56) * mm});
            skLineSegment(sketch, "E224.right", {"start": v(-98.98, -143.56) * mm, "end": v(-98.98, -161.56) * mm});
            skLineSegment(sketch, "E225.bottom", {"start": v(-76.98, -143.56) * mm, "end": v(-72.98, -143.56) * mm});
            skLineSegment(sketch, "E225.top", {"start": v(-76.98, -161.56) * mm, "end": v(-72.98, -161.56) * mm});
            skLineSegment(sketch, "E225.left", {"start": v(-76.98, -143.56) * mm, "end": v(-76.98, -161.56) * mm});
            skLineSegment(sketch, "E225.right", {"start": v(-72.98, -143.56) * mm, "end": v(-72.98, -161.56) * mm});
            skLineSegment(sketch, "E226.bottom", {"start": v(-64.98, -143.56) * mm, "end": v(-68.98, -143.56) * mm});
            skLineSegment(sketch, "E226.top", {"start": v(-64.98, -161.56) * mm, "end": v(-68.98, -161.56) * mm});
            skLineSegment(sketch, "E226.left", {"start": v(-64.98, -143.56) * mm, "end": v(-64.98, -161.56) * mm});
            skLineSegment(sketch, "E226.right", {"start": v(-68.98, -143.56) * mm, "end": v(-68.98, -161.56) * mm});
            skLineSegment(sketch, "E227.bottom", {"start": v(-46.98, -143.56) * mm, "end": v(-42.98, -143.56) * mm});
            skLineSegment(sketch, "E227.top", {"start": v(-46.98, -161.56) * mm, "end": v(-42.98, -161.56) * mm});
            skLineSegment(sketch, "E227.left", {"start": v(-46.98, -143.56) * mm, "end": v(-46.98, -161.56) * mm});
            skLineSegment(sketch, "E227.right", {"start": v(-42.98, -143.56) * mm, "end": v(-42.98, -161.56) * mm});
            skLineSegment(sketch, "E228.bottom", {"start": v(-34.98, -143.56) * mm, "end": v(-38.98, -143.56) * mm});
            skLineSegment(sketch, "E228.top", {"start": v(-34.98, -161.56) * mm, "end": v(-38.98, -161.56) * mm});
            skLineSegment(sketch, "E228.left", {"start": v(-34.98, -143.56) * mm, "end": v(-34.98, -161.56) * mm});
            skLineSegment(sketch, "E228.right", {"start": v(-38.98, -143.56) * mm, "end": v(-38.98, -161.56) * mm});
            skLineSegment(sketch, "E229.bottom", {"start": v(-16.98, -143.56) * mm, "end": v(-12.98, -143.56) * mm});
            skLineSegment(sketch, "E229.top", {"start": v(-16.98, -161.56) * mm, "end": v(-12.98, -161.56) * mm});
            skLineSegment(sketch, "E229.left", {"start": v(-16.98, -143.56) * mm, "end": v(-16.98, -161.56) * mm});
            skLineSegment(sketch, "E229.right", {"start": v(-12.98, -143.56) * mm, "end": v(-12.98, -161.56) * mm});
            skSolve(sketch);
        }
        {
            var Q0;
            Q0=qSketchRegion(id+"F36",true);
            extrude(context, id + "F37", {"entities" : qUnion([Q0]), "operationType" : NewBodyOperationType.ADD, "depth" : 3 * mm});
        }
        {
            var Q0;
            Q0=makeQuery(id+"F31.opExtrude","CAP_FACE",FACE,{"disambiguationData":[OSD([sQuery(id+"F30.wireOp",EDGE,"55227c07-3752-4080-a22d-609154aa437d.0"),sQuery(id+"F30.wireOp",EDGE,"55227c07-3752-4080-a22d-609154aa437d.1"),sQuery(id+"F30.wireOp",EDGE,"55227c07-3752-4080-a22d-609154aa437d.2"),sQuery(id+"F30.wireOp",EDGE,"55227c07-3752-4080-a22d-609154aa437d.3"),sQuery(id+"F30.wireOp",EDGE,"E111"),sQuery(id+"F30.wireOp",EDGE,"E113"),sQuery(id+"F30.wireOp",EDGE,"E118.left"),sQuery(id+"F30.wireOp",EDGE,"E118.right"),sQuery(id+"F30.wireOp",EDGE,"E119.left"),sQuery(id+"F30.wireOp",EDGE,"E119.right"),sQuery(id+"F30.wireOp",EDGE,"E120.bottom"),sQuery(id+"F30.wireOp",EDGE,"E120.top"),sQuery(id+"F30.wireOp",EDGE,"E121.trimOffspring"),sQuery(id+"F30.wireOp",EDGE,"E122.trimOffspring"),sQuery(id+"F30.wireOp",EDGE,"E125.trimOffspring"),sQuery(id+"F30.wireOp",EDGE,"E126.trimOffspring"),sQuery(id+"F30.wireOp",EDGE,"E127.trimOffspring"),sQuery(id+"F30.wireOp",EDGE,"E128.trimOffspring"),sQuery(id+"F30.wireOp",EDGE,"E129.trimOffspring"),sQuery(id+"F30.wireOp",EDGE,"E130.trimOffspring"),sQuery(id+"F30.wireOp",EDGE,"E131.bottom"),sQuery(id+"F30.wireOp",EDGE,"E131.left"),sQuery(id+"F30.wireOp",EDGE,"E131.top"),sQuery(id+"F30.wireOp",EDGE,"E131.right"),sQuery(id+"F30.wireOp",EDGE,"E134"),sQuery(id+"F30.wireOp",EDGE,"E136"),sQuery(id+"F30.wireOp",EDGE,"E141.left"),sQuery(id+"F30.wireOp",EDGE,"E141.right"),sQuery(id+"F30.wireOp",EDGE,"E142.left"),sQuery(id+"F30.wireOp",EDGE,"E142.right"),sQuery(id+"F30.wireOp",EDGE,"E143.bottom"),sQuery(id+"F30.wireOp",EDGE,"E143.top"),sQuery(id+"F30.wireOp",EDGE,"E144.trimOffspring"),sQuery(id+"F30.wireOp",EDGE,"E145.trimOffspring"),sQuery(id+"F30.wireOp",EDGE,"E148.trimOffspring"),sQuery(id+"F30.wireOp",EDGE,"E149.trimOffspring"),sQuery(id+"F30.wireOp",EDGE,"E150.trimOffspring"),sQuery(id+"F30.wireOp",EDGE,"E152.trimOffspring"),sQuery(id+"F30.wireOp",EDGE,"E153.trimOffspring"),sQuery(id+"F30.wireOp",EDGE,"E155.trimOffspring"),sQuery(id+"F30.wireOp",EDGE,"E156.bottom"),sQuery(id+"F30.wireOp",EDGE,"E156.left"),sQuery(id+"F30.wireOp",EDGE,"E156.top"),sQuery(id+"F30.wireOp",EDGE,"E156.right"),sQuery(id+"F30.wireOp",EDGE,"E160"),sQuery(id+"F30.wireOp",EDGE,"E162"),sQuery(id+"F30.wireOp",EDGE,"E167.left"),sQuery(id+"F30.wireOp",EDGE,"E167.right"),sQuery(id+"F30.wireOp",EDGE,"E168.left"),sQuery(id+"F30.wireOp",EDGE,"E168.right"),sQuery(id+"F30.wireOp",EDGE,"E169.bottom"),sQuery(id+"F30.wireOp",EDGE,"E169.top"),sQuery(id+"F30.wireOp",EDGE,"E170.trimOffspring"),sQuery(id+"F30.wireOp",EDGE,"E171.trimOffspring"),sQuery(id+"F30.wireOp",EDGE,"E174.trimOffspring"),sQuery(id+"F30.wireOp",EDGE,"E175.trimOffspring"),sQuery(id+"F30.wireOp",EDGE,"E176.trimOffspring"),sQuery(id+"F30.wireOp",EDGE,"E178.trimOffspring"),sQuery(id+"F30.wireOp",EDGE,"E179.trimOffspring"),sQuery(id+"F30.wireOp",EDGE,"E181.trimOffspring"),sQuery(id+"F30.wireOp",EDGE,"E182.bottom"),sQuery(id+"F30.wireOp",EDGE,"E182.left"),sQuery(id+"F30.wireOp",EDGE,"E182.top"),sQuery(id+"F30.wireOp",EDGE,"E182.right"),sQuery(id+"F30.wireOp",EDGE,"E186"),sQuery(id+"F30.wireOp",EDGE,"E188"),sQuery(id+"F30.wireOp",EDGE,"E193.left"),sQuery(id+"F30.wireOp",EDGE,"E193.right"),sQuery(id+"F30.wireOp",EDGE,"E194.left"),sQuery(id+"F30.wireOp",EDGE,"E194.right"),sQuery(id+"F30.wireOp",EDGE,"E195.bottom"),sQuery(id+"F30.wireOp",EDGE,"E195.top"),sQuery(id+"F30.wireOp",EDGE,"E196.trimOffspring"),sQuery(id+"F30.wireOp",EDGE,"E197.trimOffspring"),sQuery(id+"F30.wireOp",EDGE,"E200.trimOffspring"),sQuery(id+"F30.wireOp",EDGE,"E201.trimOffspring"),sQuery(id+"F30.wireOp",EDGE,"E202.trimOffspring"),sQuery(id+"F30.wireOp",EDGE,"E204.trimOffspring"),sQuery(id+"F30.wireOp",EDGE,"E205.trimOffspring"),sQuery(id+"F30.wireOp",EDGE,"E207.trimOffspring"),sQuery(id+"F30.wireOp",EDGE,"E208.bottom"),sQuery(id+"F30.wireOp",EDGE,"E208.top"),sQuery(id+"F30.wireOp",EDGE,"E208.left"),sQuery(id+"F30.wireOp",EDGE,"E208.right")])],"isStart":false});
            var sketch = newSketch(context, id + "F38", { "sketchPlane" : qUnion([Q0])});
            skLineSegment(sketch, "E230.bottom", {"start": v(-98.98, -143.56) * mm, "end": v(-72.98, -143.56) * mm});
            skLineSegment(sketch, "E230.top", {"start": v(-98.98, -134.06) * mm, "end": v(-72.98, -134.06) * mm});
            skLineSegment(sketch, "E230.left", {"start": v(-98.98, -143.56) * mm, "end": v(-98.98, -134.06) * mm});
            skLineSegment(sketch, "E230.right", {"start": v(-72.98, -143.56) * mm, "end": v(-72.98, -134.06) * mm});
            skLineSegment(sketch, "E231.bottom", {"start": v(-98.98, -161.56) * mm, "end": v(-72.98, -161.56) * mm});
            skLineSegment(sketch, "E231.top", {"start": v(-98.98, -171.06) * mm, "end": v(-72.98, -171.06) * mm});
            skLineSegment(sketch, "E231.left", {"start": v(-98.98, -161.56) * mm, "end": v(-98.98, -171.06) * mm});
            skLineSegment(sketch, "E231.right", {"start": v(-72.98, -161.56) * mm, "end": v(-72.98, -171.06) * mm});
            skCircle(sketch, "E232", {"center": v(-85.98, -137.56) * mm, "radius": 1.5 * mm});
            skCircle(sketch, "E233", {"center": v(-85.98, -167.56) * mm, "radius": 1.5 * mm});
            skLineSegment(sketch, "E234.bottom", {"start": v(-68.98, -143.56) * mm, "end": v(-42.98, -143.56) * mm});
            skLineSegment(sketch, "E234.top", {"start": v(-68.98, -134.06) * mm, "end": v(-42.98, -134.06) * mm});
            skLineSegment(sketch, "E234.left", {"start": v(-68.98, -143.56) * mm, "end": v(-68.98, -134.06) * mm});
            skLineSegment(sketch, "E234.right", {"start": v(-42.98, -143.56) * mm, "end": v(-42.98, -134.06) * mm});
            skLineSegment(sketch, "E235.bottom", {"start": v(-68.98, -161.56) * mm, "end": v(-42.98, -161.56) * mm});
            skLineSegment(sketch, "E235.top", {"start": v(-68.98, -171.06) * mm, "end": v(-42.98, -171.06) * mm});
            skLineSegment(sketch, "E235.left", {"start": v(-68.98, -161.56) * mm, "end": v(-68.98, -171.06) * mm});
            skLineSegment(sketch, "E235.right", {"start": v(-42.98, -161.56) * mm, "end": v(-42.98, -171.06) * mm});
            skLineSegment(sketch, "E236.bottom", {"start": v(-38.98, -143.56) * mm, "end": v(-12.98, -143.56) * mm});
            skLineSegment(sketch, "E236.top", {"start": v(-38.98, -134.06) * mm, "end": v(-12.98, -134.06) * mm});
            skLineSegment(sketch, "E236.left", {"start": v(-38.98, -143.56) * mm, "end": v(-38.98, -134.06) * mm});
            skLineSegment(sketch, "E236.right", {"start": v(-12.98, -143.56) * mm, "end": v(-12.98, -134.06) * mm});
            skLineSegment(sketch, "E237.bottom", {"start": v(-38.98, -161.56) * mm, "end": v(-12.98, -161.56) * mm});
            skLineSegment(sketch, "E237.top", {"start": v(-38.98, -171.06) * mm, "end": v(-12.98, -171.06) * mm});
            skLineSegment(sketch, "E237.left", {"start": v(-38.98, -161.56) * mm, "end": v(-38.98, -171.06) * mm});
            skLineSegment(sketch, "E237.right", {"start": v(-12.98, -161.56) * mm, "end": v(-12.98, -171.06) * mm});
            skCircle(sketch, "E238", {"center": v(-55.98, -137.56) * mm, "radius": 1.5 * mm});
            skCircle(sketch, "E239", {"center": v(-55.98, -167.56) * mm, "radius": 1.5 * mm});
            skCircle(sketch, "E240", {"center": v(-25.98, -137.56) * mm, "radius": 1.5 * mm});
            skCircle(sketch, "E241", {"center": v(-25.98, -167.56) * mm, "radius": 1.5 * mm});
            skSolve(sketch);
        }
        {
            var Q0;
            Q0=makeQuery(id+"F36.imprint","IMPRINT",FACE,{"disambiguationData":[TD([[makeQuery(id+"F36.imprint","IMPRINT",EDGE,{"derivedFrom":sQuery(id+"F36.wireOp",EDGE,"E224.bottom")}),-1.0]])]});
            var sketch = newSketch(context, id + "F39", { "sketchPlane" : qUnion([Q0])});
            skLineSegment(sketch, "E242.bottom", {"start": v(-124.73, -151.56) * mm, "end": v(-121.73, -151.56) * mm});
            skLineSegment(sketch, "E242.top", {"start": v(-124.73, -153.56) * mm, "end": v(-121.73, -153.56) * mm});
            skLineSegment(sketch, "E242.left", {"start": v(-124.73, -151.56) * mm, "end": v(-124.73, -153.56) * mm});
            skLineSegment(sketch, "E242.right", {"start": v(-121.73, -151.56) * mm, "end": v(-121.73, -153.56) * mm});
            skLineSegment(sketch, "E243.bottom", {"start": v(-110.23, -151.56) * mm, "end": v(-107.23, -151.56) * mm});
            skLineSegment(sketch, "E243.top", {"start": v(-110.23, -153.56) * mm, "end": v(-107.23, -153.56) * mm});
            skLineSegment(sketch, "E243.left", {"start": v(-110.23, -151.56) * mm, "end": v(-110.23, -153.56) * mm});
            skLineSegment(sketch, "E243.right", {"start": v(-107.23, -151.56) * mm, "end": v(-107.23, -153.56) * mm});
            skSolve(sketch);
        }
        {
            var Q0;
            Q0=qSketchRegion(id+"F39",true);
            extrude(context, id + "F40", {"entities" : qUnion([Q0]), "operationType" : NewBodyOperationType.ADD, "depth" : 9 * mm});
        }
        {
            var Q0;
            Q0=makeQuery(id+"F36.imprint","IMPRINT",FACE,{"disambiguationData":[TD([[makeQuery(id+"F36.imprint","IMPRINT",EDGE,{"derivedFrom":sQuery(id+"F36.wireOp",EDGE,"E224.bottom")}),-1.0]])]});
            var sketch = newSketch(context, id + "F41", { "sketchPlane" : qUnion([Q0])});
            skLineSegment(sketch, "E244.bottom", {"start": v(-118.48, -151.56) * mm, "end": v(-113.48, -151.56) * mm});
            skLineSegment(sketch, "E244.top", {"start": v(-118.48, -153.56) * mm, "end": v(-113.48, -153.56) * mm});
            skLineSegment(sketch, "E244.left", {"start": v(-118.48, -151.56) * mm, "end": v(-118.48, -153.56) * mm});
            skLineSegment(sketch, "E244.right", {"start": v(-113.48, -151.56) * mm, "end": v(-113.48, -153.56) * mm});
            skSolve(sketch);
        }
        {
            var Q0;
            Q0=qSketchRegion(id+"F41",true);
            extrude(context, id + "F42", {"entities" : qUnion([Q0]), "operationType" : NewBodyOperationType.ADD, "depth" : 3 * mm});
        }
        {
            var Q0;
            Q0=makeQuery(id+"F33.opExtrude","SWEPT_EDGE",EDGE,{"disambiguationData":[OSD([sQuery(id+"F32.wireOp",EDGE,"E209.bottom"),sQuery(id+"F32.wireOp",EDGE,"E209.left")])]});
            var Q1;
            Q1=makeQuery(id+"F33.opExtrude","SWEPT_EDGE",EDGE,{"disambiguationData":[OSD([sQuery(id+"F32.wireOp",EDGE,"E209.top"),sQuery(id+"F32.wireOp",EDGE,"E209.left")])]});
            var Q2;
            Q2=makeQuery(id+"F33.opExtrude","SWEPT_EDGE",EDGE,{"disambiguationData":[OSD([sQuery(id+"F32.wireOp",EDGE,"E209.top"),sQuery(id+"F32.wireOp",EDGE,"E209.right")])]});
            var Q3;
            Q3=makeQuery(id+"F33.opExtrude","SWEPT_EDGE",EDGE,{"disambiguationData":[OSD([sQuery(id+"F32.wireOp",EDGE,"E209.bottom"),sQuery(id+"F32.wireOp",EDGE,"E209.right")])]});
            var Q4;
            Q4=makeQuery(id+"F33.opExtrude","CAP_EDGE",EDGE,{"disambiguationData":[OSD([sQuery(id+"F32.wireOp",EDGE,"E209.top")])],"isStart":false});
            var Q5;
            Q5=makeQuery(id+"F33.opExtrude","CAP_EDGE",EDGE,{"disambiguationData":[OSD([sQuery(id+"F32.wireOp",EDGE,"E209.left")])],"isStart":false});
            var Q6;
            Q6=makeQuery(id+"F33.opExtrude","CAP_EDGE",EDGE,{"disambiguationData":[OSD([sQuery(id+"F32.wireOp",EDGE,"E209.bottom")])],"isStart":false});
            var Q7;
            Q7=makeQuery(id+"F33.opExtrude","CAP_EDGE",EDGE,{"disambiguationData":[OSD([sQuery(id+"F32.wireOp",EDGE,"E209.right")])],"isStart":false});
            fillet(context, id + "F43", {"entities" : qUnion([Q0, Q1, Q2, Q3, Q4, Q5, Q6, Q7]), "radius" : 1 * mm, "tangentPropagation" : true, "allowEdgeOverflow" : false});
        }
        {
            var Q0;
            Q0=makeQuery(id+"F10.opExtrude","SWEPT_EDGE",EDGE,{"disambiguationData":[OSD([sQuery(id+"F9.wireOp",EDGE,"E41.top"),sQuery(id+"F9.wireOp",EDGE,"E41.right")])]});
            var Q1;
            Q1=makeQuery(id+"F10.opExtrude","CAP_EDGE",EDGE,{"disambiguationData":[OSD([sQuery(id+"F9.wireOp",EDGE,"E41.top")])],"isStart":false});
            var Q2;
            Q2=makeQuery(id+"F10.opExtrude","CAP_EDGE",EDGE,{"disambiguationData":[OSD([sQuery(id+"F9.wireOp",EDGE,"E41.right")])],"isStart":false});
            var Q3;
            Q3=makeQuery(id+"F10.opExtrude","SWEPT_EDGE",EDGE,{"disambiguationData":[OSD([sQuery(id+"F9.wireOp",EDGE,"E41.bottom"),sQuery(id+"F9.wireOp",EDGE,"E41.right")])]});
            var Q4;
            Q4=makeQuery(id+"F10.opExtrude","CAP_EDGE",EDGE,{"disambiguationData":[OSD([sQuery(id+"F9.wireOp",EDGE,"E41.bottom")])],"isStart":false});
            var Q5;
            Q5=makeQuery(id+"F10.opExtrude","SWEPT_EDGE",EDGE,{"disambiguationData":[OSD([sQuery(id+"F9.wireOp",EDGE,"E41.bottom"),sQuery(id+"F9.wireOp",EDGE,"E41.left")])]});
            var Q6;
            Q6=makeQuery(id+"F10.opExtrude","CAP_EDGE",EDGE,{"disambiguationData":[OSD([sQuery(id+"F9.wireOp",EDGE,"E41.left")])],"isStart":false});
            var Q7;
            Q7=makeQuery(id+"F10.opExtrude","SWEPT_EDGE",EDGE,{"disambiguationData":[OSD([sQuery(id+"F9.wireOp",EDGE,"E41.top"),sQuery(id+"F9.wireOp",EDGE,"E41.left")])]});
            var Q8;
            Q8=makeQuery(id+"F1.opExtrude","SWEPT_EDGE",EDGE,{"disambiguationData":[OSD([sQuery(id+"F0.wireOp",EDGE,"E1.bottom"),sQuery(id+"F0.wireOp",EDGE,"E1.right")])]});
            var Q9;
            Q9=makeQuery(id+"F1.opExtrude","CAP_EDGE",EDGE,{"disambiguationData":[OSD([sQuery(id+"F0.wireOp",EDGE,"E1.bottom")])],"isStart":false});
            var Q10;
            Q10=makeQuery(id+"F1.opExtrude","SWEPT_EDGE",EDGE,{"disambiguationData":[OSD([sQuery(id+"F0.wireOp",EDGE,"E1.bottom"),sQuery(id+"F0.wireOp",EDGE,"E1.left")])]});
            var Q11;
            Q11=makeQuery(id+"F1.opExtrude","CAP_EDGE",EDGE,{"disambiguationData":[OSD([sQuery(id+"F0.wireOp",EDGE,"E1.right")])],"isStart":false});
            var Q12;
            Q12=makeQuery(id+"F1.opExtrude","SWEPT_EDGE",EDGE,{"disambiguationData":[OSD([sQuery(id+"F0.wireOp",EDGE,"E1.top"),sQuery(id+"F0.wireOp",EDGE,"E1.right")])]});
            var Q13;
            Q13=makeQuery(id+"F1.opExtrude","CAP_EDGE",EDGE,{"disambiguationData":[OSD([sQuery(id+"F0.wireOp",EDGE,"E1.top")])],"isStart":false});
            var Q14;
            Q14=makeQuery(id+"F1.opExtrude","SWEPT_EDGE",EDGE,{"disambiguationData":[OSD([sQuery(id+"F0.wireOp",EDGE,"E1.top"),sQuery(id+"F0.wireOp",EDGE,"E1.left")])]});
            var Q15;
            Q15=makeQuery(id+"F1.opExtrude","CAP_EDGE",EDGE,{"disambiguationData":[OSD([sQuery(id+"F0.wireOp",EDGE,"E1.left")])],"isStart":false});
            fillet(context, id + "F44", {"entities" : qUnion([Q0, Q1, Q2, Q3, Q4, Q5, Q6, Q7, Q8, Q9, Q10, Q11, Q12, Q13, Q14, Q15]), "radius" : 0.5 * mm, "tangentPropagation" : true, "allowEdgeOverflow" : false});
        }
        {
            var Q0;
            Q0=makeQuery(id+"F38.imprint","IMPRINT",FACE,{"disambiguationData":[TD([[makeQuery(id+"F38.imprint","IMPRINT",EDGE,{"derivedFrom":sQuery(id+"F38.wireOp",EDGE,"E230.top")}),-1.0]])]});
            var Q1;
            Q1=makeQuery(id+"F38.imprint","IMPRINT",FACE,{"disambiguationData":[TD([[makeQuery(id+"F38.imprint","IMPRINT",EDGE,{"derivedFrom":sQuery(id+"F38.wireOp",EDGE,"E231.top")}),1.0]])]});
            var Q2;
            Q2=makeQuery(id+"F38.imprint","IMPRINT",FACE,{"disambiguationData":[TD([[makeQuery(id+"F38.imprint","IMPRINT",EDGE,{"derivedFrom":sQuery(id+"F38.wireOp",EDGE,"E235.top")}),1.0]])]});
            var Q3;
            Q3=makeQuery(id+"F38.imprint","IMPRINT",FACE,{"disambiguationData":[TD([[makeQuery(id+"F38.imprint","IMPRINT",EDGE,{"derivedFrom":sQuery(id+"F38.wireOp",EDGE,"E234.top")}),-1.0]])]});
            var Q4;
            Q4=makeQuery(id+"F38.imprint","IMPRINT",FACE,{"disambiguationData":[TD([[makeQuery(id+"F38.imprint","IMPRINT",EDGE,{"derivedFrom":sQuery(id+"F38.wireOp",EDGE,"E236.top")}),-1.0]])]});
            var Q5;
            Q5=makeQuery(id+"F38.imprint","IMPRINT",FACE,{"disambiguationData":[TD([[makeQuery(id+"F38.imprint","IMPRINT",EDGE,{"derivedFrom":sQuery(id+"F38.wireOp",EDGE,"E237.top")}),1.0]])]});
            extrude(context, id + "F45", {"entities" : qUnion([Q0, Q1, Q2, Q3, Q4, Q5]), "operationType" : NewBodyOperationType.ADD, "depth" : 3 * mm});
        }
        {
            var Q0;
            Q0=makeQuery(id+"F31.opExtrude","SWEPT_FACE",FACE,{"disambiguationData":[OSD([sQuery(id+"F30.wireOp",EDGE,"E208.left")])]});
            extrude(context, id + "F46", {"entities" : qUnion([Q0]), "operationType" : NewBodyOperationType.ADD, "depth" : 2 * mm});
        }
        {
            var Q0;
            {var subQ0=sQuery(id+"F30.wireOp",EDGE,"E208.left");var subQ1=sQuery(id+"F30.wireOp",EDGE,"55227c07-3752-4080-a22d-609154aa437d.3");var subQ2=sQuery(id+"F30.wireOp",EDGE,"55227c07-3752-4080-a22d-609154aa437d.0");var subQ4=sQuery(id+"F30.wireOp",EDGE,"E129.trimOffspring");var subQ6=sQuery(id+"F30.wireOp",EDGE,"E208.top");var subQ7=sQuery(id+"F30.wireOp",EDGE,"E130.trimOffspring");var subQ8=sQuery(id+"F30.wireOp",EDGE,"55227c07-3752-4080-a22d-609154aa437d.2");var subQ11=sQuery(id+"F30.wireOp",EDGE,"E128.trimOffspring");var subQ13=sQuery(id+"F30.wireOp",EDGE,"E208.bottom");var subQ14=sQuery(id+"F30.wireOp",EDGE,"E122.trimOffspring");var subQ16=sQuery(id+"F30.wireOp",EDGE,"E127.trimOffspring");var subQ17=sQuery(id+"F30.wireOp",EDGE,"E126.trimOffspring");var subQ18=sQuery(id+"F30.wireOp",EDGE,"55227c07-3752-4080-a22d-609154aa437d.1");var subQ21=sQuery(id+"F30.wireOp",EDGE,"E120.bottom");var subQ22=sQuery(id+"F30.wireOp",EDGE,"E119.right");var subQ24=sQuery(id+"F30.wireOp",EDGE,"E118.right");var subQ26=sQuery(id+"F30.wireOp",EDGE,"E119.left");var subQ28=sQuery(id+"F30.wireOp",EDGE,"E121.trimOffspring");var subQ29=sQuery(id+"F30.wireOp",EDGE,"E120.top");var subQ30=sQuery(id+"F30.wireOp",EDGE,"E118.left");var subQ31=sQuery(id+"F30.wireOp",EDGE,"E111");var subQ32=sQuery(id+"F30.wireOp",EDGE,"E113");var subQ33=sQuery(id+"F30.wireOp",EDGE,"E125.trimOffspring");Q0=makeQuery(id+"F46.boolean.opBoolean","MERGE",FACE,{"derivedFrom":[makeQuery(id+"F45.boolean.opBoolean","SPLIT",FACE,{"disambiguationData":[TD([makeQuery(id+"F31.opExtrude","SWEPT_FACE",FACE,{"disambiguationData":[OSD([subQ31])]})])],"derivedFrom":makeQuery(id+"F31.opExtrude","CAP_FACE",FACE,{"disambiguationData":[OSD([subQ2,subQ18,subQ8,subQ1,subQ31,subQ32,subQ30,subQ24,subQ26,subQ22,subQ21,subQ29,subQ28,subQ14,subQ33,subQ17,subQ16,subQ11,subQ4,subQ7,sQuery(id+"F30.wireOp",EDGE,"E131.bottom"),sQuery(id+"F30.wireOp",EDGE,"E131.left"),sQuery(id+"F30.wireOp",EDGE,"E131.top"),sQuery(id+"F30.wireOp",EDGE,"E131.right"),sQuery(id+"F30.wireOp",EDGE,"E134"),sQuery(id+"F30.wireOp",EDGE,"E136"),sQuery(id+"F30.wireOp",EDGE,"E141.left"),sQuery(id+"F30.wireOp",EDGE,"E141.right"),sQuery(id+"F30.wireOp",EDGE,"E142.left"),sQuery(id+"F30.wireOp",EDGE,"E142.right"),sQuery(id+"F30.wireOp",EDGE,"E143.bottom"),sQuery(id+"F30.wireOp",EDGE,"E143.top"),sQuery(id+"F30.wireOp",EDGE,"E144.trimOffspring"),sQuery(id+"F30.wireOp",EDGE,"E145.trimOffspring"),sQuery(id+"F30.wireOp",EDGE,"E148.trimOffspring"),sQuery(id+"F30.wireOp",EDGE,"E149.trimOffspring"),sQuery(id+"F30.wireOp",EDGE,"E150.trimOffspring"),sQuery(id+"F30.wireOp",EDGE,"E152.trimOffspring"),sQuery(id+"F30.wireOp",EDGE,"E153.trimOffspring"),sQuery(id+"F30.wireOp",EDGE,"E155.trimOffspring"),sQuery(id+"F30.wireOp",EDGE,"E156.bottom"),sQuery(id+"F30.wireOp",EDGE,"E156.left"),sQuery(id+"F30.wireOp",EDGE,"E156.top"),sQuery(id+"F30.wireOp",EDGE,"E156.right"),sQuery(id+"F30.wireOp",EDGE,"E160"),sQuery(id+"F30.wireOp",EDGE,"E162"),sQuery(id+"F30.wireOp",EDGE,"E167.left"),sQuery(id+"F30.wireOp",EDGE,"E167.right"),sQuery(id+"F30.wireOp",EDGE,"E168.left"),sQuery(id+"F30.wireOp",EDGE,"E168.right"),sQuery(id+"F30.wireOp",EDGE,"E169.bottom"),sQuery(id+"F30.wireOp",EDGE,"E169.top"),sQuery(id+"F30.wireOp",EDGE,"E170.trimOffspring"),sQuery(id+"F30.wireOp",EDGE,"E171.trimOffspring"),sQuery(id+"F30.wireOp",EDGE,"E174.trimOffspring"),sQuery(id+"F30.wireOp",EDGE,"E175.trimOffspring"),sQuery(id+"F30.wireOp",EDGE,"E176.trimOffspring"),sQuery(id+"F30.wireOp",EDGE,"E178.trimOffspring"),sQuery(id+"F30.wireOp",EDGE,"E179.trimOffspring"),sQuery(id+"F30.wireOp",EDGE,"E181.trimOffspring"),sQuery(id+"F30.wireOp",EDGE,"E182.bottom"),sQuery(id+"F30.wireOp",EDGE,"E182.left"),sQuery(id+"F30.wireOp",EDGE,"E182.top"),sQuery(id+"F30.wireOp",EDGE,"E182.right"),sQuery(id+"F30.wireOp",EDGE,"E186"),sQuery(id+"F30.wireOp",EDGE,"E188"),sQuery(id+"F30.wireOp",EDGE,"E193.left"),sQuery(id+"F30.wireOp",EDGE,"E193.right"),sQuery(id+"F30.wireOp",EDGE,"E194.left"),sQuery(id+"F30.wireOp",EDGE,"E194.right"),sQuery(id+"F30.wireOp",EDGE,"E195.bottom"),sQuery(id+"F30.wireOp",EDGE,"E195.top"),sQuery(id+"F30.wireOp",EDGE,"E196.trimOffspring"),sQuery(id+"F30.wireOp",EDGE,"E197.trimOffspring"),sQuery(id+"F30.wireOp",EDGE,"E200.trimOffspring"),sQuery(id+"F30.wireOp",EDGE,"E201.trimOffspring"),sQuery(id+"F30.wireOp",EDGE,"E202.trimOffspring"),sQuery(id+"F30.wireOp",EDGE,"E204.trimOffspring"),sQuery(id+"F30.wireOp",EDGE,"E205.trimOffspring"),sQuery(id+"F30.wireOp",EDGE,"E207.trimOffspring"),subQ13,subQ6,subQ0,sQuery(id+"F30.wireOp",EDGE,"E208.right")])],"isStart":false})}),makeQuery(id+"F46.opExtrude","SWEPT_FACE",FACE,{"disambiguationData":[OSD([subQ0]),TDD([makeQuery(id+"F31.opExtrude","CAP_EDGE",EDGE,{"disambiguationData":[OSD([subQ0])],"isStart":false})])]})]});}
            var sketch = newSketch(context, id + "F47", { "sketchPlane" : qUnion([Q0])});
            skLineSegment(sketch, "E245.bottom", {"start": v(-131.58, -134.06) * mm, "end": v(-129.58, -134.06) * mm});
            skLineSegment(sketch, "E245.top", {"start": v(-131.58, -171.06) * mm, "end": v(-129.58, -171.06) * mm});
            skLineSegment(sketch, "E245.left", {"start": v(-131.58, -134.06) * mm, "end": v(-131.58, -171.06) * mm});
            skLineSegment(sketch, "E245.right", {"start": v(-129.58, -134.06) * mm, "end": v(-129.58, -171.06) * mm});
            skSolve(sketch);
        }
        {
            var Q0;
            Q0=qSketchRegion(id+"F47",true);
            extrude(context, id + "F48", {"entities" : qUnion([Q0]), "operationType" : NewBodyOperationType.ADD, "depth" : 7 * mm});
        }
        {
            var Q0;
            Q0=makeQuery(id+"F35.boolean.opBoolean","COPY",FACE,{"derivedFrom":makeQuery(id+"F35.opExtrude","CAP_FACE",FACE,{"disambiguationData":[OSD([sQuery(id+"F34.wireOp",EDGE,"E223.bottom"),sQuery(id+"F34.wireOp",EDGE,"E223.top"),sQuery(id+"F34.wireOp",EDGE,"E223.left"),sQuery(id+"F34.wireOp",EDGE,"E223.right")])],"isStart":false})});
            var sketch = newSketch(context, id + "F49", { "sketchPlane" : qUnion([Q0])});
            skLineSegment(sketch, "E246.bottom", {"start": v(22.06, 164.66) * mm, "end": v(42.46, 164.66) * mm});
            skLineSegment(sketch, "E246.top", {"start": v(22.06, 173.06) * mm, "end": v(42.46, 173.06) * mm});
            skLineSegment(sketch, "E246.left", {"start": v(22.06, 164.66) * mm, "end": v(22.06, 173.06) * mm});
            skLineSegment(sketch, "E246.right", {"start": v(42.46, 164.66) * mm, "end": v(42.46, 173.06) * mm});
            skLineSegment(sketch, "E247.bottom", {"start": v(22.06, 144.26) * mm, "end": v(42.46, 144.26) * mm});
            skLineSegment(sketch, "E247.top", {"start": v(22.06, 135.86) * mm, "end": v(42.46, 135.86) * mm});
            skLineSegment(sketch, "E247.left", {"start": v(22.06, 144.26) * mm, "end": v(22.06, 135.86) * mm});
            skLineSegment(sketch, "E247.right", {"start": v(42.46, 144.26) * mm, "end": v(42.46, 135.86) * mm});
            skSolve(sketch);
        }
        {
            var Q0;
            Q0=qSketchRegion(id+"F49",true);
            extrude(context, id + "F50", {"entities" : qUnion([Q0]), "operationType" : NewBodyOperationType.ADD, "depth" : 3 * mm});
        }
        {
            var Q0;
            Q0=makeQuery(id+"F33.opExtrude","SWEPT_FACE",FACE,{"disambiguationData":[OSD([sQuery(id+"F32.wireOp",EDGE,"E209.left")])]});
            var sketch = newSketch(context, id + "F51", { "sketchPlane" : qUnion([Q0])});
            skCircle(sketch, "E248", {"center": v(139.86, 5.5) * mm, "radius": 1.5 * mm});
            skCircle(sketch, "E249", {"center": v(169.06, 5.5) * mm, "radius": 1.5 * mm});
            skSolve(sketch);
        }
        {
            var Q0;
            Q0=qSketchRegion(id+"F51",true);
            extrude(context, id + "F52", {"entities" : qUnion([Q0]), "operationType" : NewBodyOperationType.REMOVE, "oppositeDirection" : true, "depth" : 3 * mm});
        }
        {
            var Q0;
            Q0=makeQuery(id+"F48.boolean.opBoolean","MERGE",FACE,{"derivedFrom":[makeQuery(id+"F46.opExtrude","CAP_FACE",FACE,{"disambiguationData":[OSD([sQuery(id+"F30.wireOp",EDGE,"E208.left")])],"isStart":false}),makeQuery(id+"F48.opExtrude","SWEPT_FACE",FACE,{"disambiguationData":[OSD([sQuery(id+"F47.wireOp",EDGE,"E245.left")])]})]});
            var sketch = newSketch(context, id + "F53", { "sketchPlane" : qUnion([Q0])});
            skCircle(sketch, "E250", {"center": v(137.96, 5.5) * mm, "radius": 1.2 * mm});
            skCircle(sketch, "E251", {"center": v(167.16, 5.5) * mm, "radius": 1.2 * mm});
            skSolve(sketch);
        }
        {
            var Q0;
            Q0=makeQuery(id+"F33.opExtrude","SWEPT_FACE",FACE,{"disambiguationData":[OSD([sQuery(id+"F32.wireOp",EDGE,"E209.right")])]});
            var sketch = newSketch(context, id + "F54", { "sketchPlane" : qUnion([Q0])});
            skCircle(sketch, "E252", {"center": v(-169.06, 5.5) * mm, "radius": 1.5 * mm});
            skCircle(sketch, "E253", {"center": v(-139.86, 5.5) * mm, "radius": 1.5 * mm});
            skSolve(sketch);
        }
        {
            var Q0;
            Q0=makeQuery(id+"F54.imprint","IMPRINT",FACE,{"disambiguationData":[TD([[makeQuery(id+"F54.imprint","IMPRINT",EDGE,{"derivedFrom":sQuery(id+"F54.wireOp",EDGE,"E252")}),1.0]])]});
            var Q1;
            Q1=makeQuery(id+"F54.imprint","IMPRINT",FACE,{"disambiguationData":[TD([[makeQuery(id+"F54.imprint","IMPRINT",EDGE,{"derivedFrom":sQuery(id+"F54.wireOp",EDGE,"E253")}),1.0]])]});
            extrude(context, id + "F55", {"entities" : qUnion([Q0, Q1]), "operationType" : NewBodyOperationType.REMOVE, "oppositeDirection" : true, "depth" : 2 * mm});
        }
        {
            var Q0;
            {var subQ0=sQuery(id+"F34.wireOp",EDGE,"E223.top");var subQ1=sQuery(id+"F34.wireOp",EDGE,"E223.bottom");var subQ2=sQuery(id+"F34.wireOp",EDGE,"E223.right");Q0=makeQuery(id+"F50.boolean.opBoolean","SPLIT",FACE,{"disambiguationData":[TD([makeQuery(id+"F33.opExtrude","SWEPT_FACE",FACE,{"disambiguationData":[OSD([sQuery(id+"F32.wireOp",EDGE,"E210.right")])]})])],"derivedFrom":makeQuery(id+"F35.boolean.opBoolean","COPY",FACE,{"derivedFrom":makeQuery(id+"F35.opExtrude","CAP_FACE",FACE,{"disambiguationData":[OSD([subQ1,subQ0,sQuery(id+"F34.wireOp",EDGE,"E223.left"),subQ2])],"isStart":false})})});}
            var sketch = newSketch(context, id + "F56", { "sketchPlane" : qUnion([Q0])});
            skLineSegment(sketch, "E254.bottom", {"start": v(45.96, 173.06) * mm, "end": v(48.96, 173.06) * mm});
            skLineSegment(sketch, "E254.top", {"start": v(45.96, 135.86) * mm, "end": v(48.96, 135.86) * mm});
            skLineSegment(sketch, "E254.left", {"start": v(45.96, 173.06) * mm, "end": v(45.96, 135.86) * mm});
            skLineSegment(sketch, "E254.right", {"start": v(48.96, 173.06) * mm, "end": v(48.96, 135.86) * mm});
            skLineSegment(sketch, "E255.bottom", {"start": v(75.86, 173.06) * mm, "end": v(78.86, 173.06) * mm});
            skLineSegment(sketch, "E255.top", {"start": v(75.86, 135.86) * mm, "end": v(78.86, 135.86) * mm});
            skLineSegment(sketch, "E255.left", {"start": v(75.86, 173.06) * mm, "end": v(75.86, 135.86) * mm});
            skLineSegment(sketch, "E255.right", {"start": v(78.86, 173.06) * mm, "end": v(78.86, 135.86) * mm});
            skLineSegment(sketch, "E256.bottom", {"start": v(105.86, 173.06) * mm, "end": v(108.86, 173.06) * mm});
            skLineSegment(sketch, "E256.top", {"start": v(105.86, 135.86) * mm, "end": v(108.86, 135.86) * mm});
            skLineSegment(sketch, "E256.left", {"start": v(105.86, 173.06) * mm, "end": v(105.86, 135.86) * mm});
            skLineSegment(sketch, "E256.right", {"start": v(108.86, 173.06) * mm, "end": v(108.86, 135.86) * mm});
            skSolve(sketch);
        }
        {
            var Q0;
            Q0=qSketchRegion(id+"F56",true);
            extrude(context, id + "F57", {"entities" : qUnion([Q0]), "operationType" : NewBodyOperationType.ADD, "depth" : 1 * mm});
        }
        {
            var Q0;
            Q0=makeQuery(id+"F45.boolean.opBoolean","MERGE",FACE,{"derivedFrom":[makeQuery(id+"F37.opExtrude","SWEPT_FACE",FACE,{"disambiguationData":[OSD([sQuery(id+"F36.wireOp",EDGE,"E229.right")])]}),makeQuery(id+"F45.opExtrude","SWEPT_FACE",FACE,{"disambiguationData":[OSD([sQuery(id+"F38.wireOp",EDGE,"E236.right")])]}),makeQuery(id+"F45.opExtrude","SWEPT_FACE",FACE,{"disambiguationData":[OSD([sQuery(id+"F38.wireOp",EDGE,"E237.right")])]})]});
            extrude(context, id + "F58", {"entities" : qUnion([Q0]), "operationType" : NewBodyOperationType.ADD, "depth" : 1 * mm});
        }
        {
            var Q0;
            {var subQ0=sQuery(id+"F38.wireOp",EDGE,"E237.right");var subQ1=sQuery(id+"F38.wireOp",EDGE,"E236.right");var subQ2=sQuery(id+"F36.wireOp",EDGE,"E229.right");Q0=makeQuery(id+"F58.boolean.opBoolean","MERGE",FACE,{"derivedFrom":[makeQuery(id+"F45.boolean.opBoolean","MERGE",FACE,{"derivedFrom":[makeQuery(id+"F37.opExtrude","CAP_FACE",FACE,{"disambiguationData":[OSD([sQuery(id+"F36.wireOp",EDGE,"E228.bottom"),sQuery(id+"F36.wireOp",EDGE,"E228.top"),sQuery(id+"F36.wireOp",EDGE,"E228.left"),sQuery(id+"F36.wireOp",EDGE,"E228.right")])],"isStart":false}),makeQuery(id+"F37.opExtrude","CAP_FACE",FACE,{"disambiguationData":[OSD([sQuery(id+"F36.wireOp",EDGE,"E229.bottom"),sQuery(id+"F36.wireOp",EDGE,"E229.top"),sQuery(id+"F36.wireOp",EDGE,"E229.left"),subQ2])],"isStart":false}),makeQuery(id+"F45.opExtrude","CAP_FACE",FACE,{"disambiguationData":[OSD([sQuery(id+"F38.wireOp",EDGE,"E236.bottom"),sQuery(id+"F38.wireOp",EDGE,"E236.top"),sQuery(id+"F38.wireOp",EDGE,"E236.left"),subQ1,sQuery(id+"F38.wireOp",EDGE,"E240")])],"isStart":false}),makeQuery(id+"F45.opExtrude","CAP_FACE",FACE,{"disambiguationData":[OSD([sQuery(id+"F38.wireOp",EDGE,"E237.bottom"),sQuery(id+"F38.wireOp",EDGE,"E237.top"),sQuery(id+"F38.wireOp",EDGE,"E237.left"),subQ0,sQuery(id+"F38.wireOp",EDGE,"E241")])],"isStart":false})]}),makeQuery(id+"F58.opExtrude","SWEPT_FACE",FACE,{"disambiguationData":[OSD([subQ2,subQ1,subQ0]),TDD([makeQuery(id+"F45.boolean.opBoolean","MERGE",EDGE,{"derivedFrom":[makeQuery(id+"F37.opExtrude","CAP_EDGE",EDGE,{"disambiguationData":[OSD([subQ2])],"isStart":false}),makeQuery(id+"F45.opExtrude","CAP_EDGE",EDGE,{"disambiguationData":[OSD([subQ1])],"isStart":false}),makeQuery(id+"F45.opExtrude","CAP_EDGE",EDGE,{"disambiguationData":[OSD([subQ0])],"isStart":false})]})])]})]});}
            var sketch = newSketch(context, id + "F59", { "sketchPlane" : qUnion([Q0])});
            skLineSegment(sketch, "E257.bottom", {"start": v(-11.98, -171.06) * mm, "end": v(-13.98, -171.06) * mm});
            skLineSegment(sketch, "E257.top", {"start": v(-11.98, -134.06) * mm, "end": v(-13.98, -134.06) * mm});
            skLineSegment(sketch, "E257.left", {"start": v(-11.98, -171.06) * mm, "end": v(-11.98, -134.06) * mm});
            skLineSegment(sketch, "E257.right", {"start": v(-13.98, -171.06) * mm, "end": v(-13.98, -134.06) * mm});
            skSolve(sketch);
        }
        {
            var Q0;
            Q0=qSketchRegion(id+"F59",true);
            extrude(context, id + "F60", {"entities" : qUnion([Q0]), "operationType" : NewBodyOperationType.ADD, "depth" : 4 * mm});
        }
        {
            var Q0;
            Q0=qSketchRegion(id+"F53",true);
            extrude(context, id + "F61", {"entities" : qUnion([Q0]), "operationType" : NewBodyOperationType.REMOVE, "endBound" : BoundingType.THROUGH_ALL, "oppositeDirection" : true, "depth" : 3 * mm});
        }
        {
            var Q0;
            Q0=qSketchRegion(id+"F56",true);
            extrude(context, id + "F62", {"entities" : qUnion([Q0]), "operationType" : NewBodyOperationType.ADD, "depth" : 3 * mm});
        }
        {
            var Q0;
            Q0=makeQuery(id+"F45.boolean.opBoolean","MERGE",FACE,{"derivedFrom":[makeQuery(id+"F37.opExtrude","SWEPT_FACE",FACE,{"disambiguationData":[OSD([sQuery(id+"F36.wireOp",EDGE,"E225.right")])]}),makeQuery(id+"F45.opExtrude","SWEPT_FACE",FACE,{"disambiguationData":[OSD([sQuery(id+"F38.wireOp",EDGE,"E230.right")])]}),makeQuery(id+"F45.opExtrude","SWEPT_FACE",FACE,{"disambiguationData":[OSD([sQuery(id+"F38.wireOp",EDGE,"E231.right")])]})]});
            var Q1;
            Q1=makeQuery(id+"F45.boolean.opBoolean","MERGE",FACE,{"derivedFrom":[makeQuery(id+"F37.opExtrude","SWEPT_FACE",FACE,{"disambiguationData":[OSD([sQuery(id+"F36.wireOp",EDGE,"E227.right")])]}),makeQuery(id+"F45.opExtrude","SWEPT_FACE",FACE,{"disambiguationData":[OSD([sQuery(id+"F38.wireOp",EDGE,"E234.right")])]}),makeQuery(id+"F45.opExtrude","SWEPT_FACE",FACE,{"disambiguationData":[OSD([sQuery(id+"F38.wireOp",EDGE,"E235.right")])]})]});
            extrude(context, id + "F63", {"entities" : qUnion([Q0, Q1]), "operationType" : NewBodyOperationType.ADD, "depth" : 5 * mm});
        }
        {
            var Q0;
            Q0=makeQuery(id+"F30.imprint","IMPRINT",FACE,{"disambiguationData":[TD([[makeQuery(id+"F30.imprint","IMPRINT",EDGE,{"derivedFrom":sQuery(id+"F30.wireOp",EDGE,"E111")}),-1.0]])]});
            var Q1;
            {var subQ0=sQuery(id+"F30.wireOp",EDGE,"E208.left");Q1=makeQuery(id+"F46.boolean.opBoolean","MERGE",FACE,{"derivedFrom":[makeQuery(id+"F31.opExtrude","CAP_FACE",FACE,{"disambiguationData":[OSD([sQuery(id+"F30.wireOp",EDGE,"55227c07-3752-4080-a22d-609154aa437d.0"),sQuery(id+"F30.wireOp",EDGE,"55227c07-3752-4080-a22d-609154aa437d.1"),sQuery(id+"F30.wireOp",EDGE,"55227c07-3752-4080-a22d-609154aa437d.2"),sQuery(id+"F30.wireOp",EDGE,"55227c07-3752-4080-a22d-609154aa437d.3"),sQuery(id+"F30.wireOp",EDGE,"E111"),sQuery(id+"F30.wireOp",EDGE,"E113"),sQuery(id+"F30.wireOp",EDGE,"E118.left"),sQuery(id+"F30.wireOp",EDGE,"E118.right"),sQuery(id+"F30.wireOp",EDGE,"E119.left"),sQuery(id+"F30.wireOp",EDGE,"E119.right"),sQuery(id+"F30.wireOp",EDGE,"E120.bottom"),sQuery(id+"F30.wireOp",EDGE,"E120.top"),sQuery(id+"F30.wireOp",EDGE,"E121.trimOffspring"),sQuery(id+"F30.wireOp",EDGE,"E122.trimOffspring"),sQuery(id+"F30.wireOp",EDGE,"E125.trimOffspring"),sQuery(id+"F30.wireOp",EDGE,"E126.trimOffspring"),sQuery(id+"F30.wireOp",EDGE,"E127.trimOffspring"),sQuery(id+"F30.wireOp",EDGE,"E128.trimOffspring"),sQuery(id+"F30.wireOp",EDGE,"E129.trimOffspring"),sQuery(id+"F30.wireOp",EDGE,"E130.trimOffspring"),sQuery(id+"F30.wireOp",EDGE,"E131.bottom"),sQuery(id+"F30.wireOp",EDGE,"E131.left"),sQuery(id+"F30.wireOp",EDGE,"E131.top"),sQuery(id+"F30.wireOp",EDGE,"E131.right"),sQuery(id+"F30.wireOp",EDGE,"E134"),sQuery(id+"F30.wireOp",EDGE,"E136"),sQuery(id+"F30.wireOp",EDGE,"E141.left"),sQuery(id+"F30.wireOp",EDGE,"E141.right"),sQuery(id+"F30.wireOp",EDGE,"E142.left"),sQuery(id+"F30.wireOp",EDGE,"E142.right"),sQuery(id+"F30.wireOp",EDGE,"E143.bottom"),sQuery(id+"F30.wireOp",EDGE,"E143.top"),sQuery(id+"F30.wireOp",EDGE,"E144.trimOffspring"),sQuery(id+"F30.wireOp",EDGE,"E145.trimOffspring"),sQuery(id+"F30.wireOp",EDGE,"E148.trimOffspring"),sQuery(id+"F30.wireOp",EDGE,"E149.trimOffspring"),sQuery(id+"F30.wireOp",EDGE,"E150.trimOffspring"),sQuery(id+"F30.wireOp",EDGE,"E152.trimOffspring"),sQuery(id+"F30.wireOp",EDGE,"E153.trimOffspring"),sQuery(id+"F30.wireOp",EDGE,"E155.trimOffspring"),sQuery(id+"F30.wireOp",EDGE,"E156.bottom"),sQuery(id+"F30.wireOp",EDGE,"E156.left"),sQuery(id+"F30.wireOp",EDGE,"E156.top"),sQuery(id+"F30.wireOp",EDGE,"E156.right"),sQuery(id+"F30.wireOp",EDGE,"E160"),sQuery(id+"F30.wireOp",EDGE,"E162"),sQuery(id+"F30.wireOp",EDGE,"E167.left"),sQuery(id+"F30.wireOp",EDGE,"E167.right"),sQuery(id+"F30.wireOp",EDGE,"E168.left"),sQuery(id+"F30.wireOp",EDGE,"E168.right"),sQuery(id+"F30.wireOp",EDGE,"E169.bottom"),sQuery(id+"F30.wireOp",EDGE,"E169.top"),sQuery(id+"F30.wireOp",EDGE,"E170.trimOffspring"),sQuery(id+"F30.wireOp",EDGE,"E171.trimOffspring"),sQuery(id+"F30.wireOp",EDGE,"E174.trimOffspring"),sQuery(id+"F30.wireOp",EDGE,"E175.trimOffspring"),sQuery(id+"F30.wireOp",EDGE,"E176.trimOffspring"),sQuery(id+"F30.wireOp",EDGE,"E178.trimOffspring"),sQuery(id+"F30.wireOp",EDGE,"E179.trimOffspring"),sQuery(id+"F30.wireOp",EDGE,"E181.trimOffspring"),sQuery(id+"F30.wireOp",EDGE,"E182.bottom"),sQuery(id+"F30.wireOp",EDGE,"E182.left"),sQuery(id+"F30.wireOp",EDGE,"E182.top"),sQuery(id+"F30.wireOp",EDGE,"E182.right"),sQuery(id+"F30.wireOp",EDGE,"E186"),sQuery(id+"F30.wireOp",EDGE,"E188"),sQuery(id+"F30.wireOp",EDGE,"E193.left"),sQuery(id+"F30.wireOp",EDGE,"E193.right"),sQuery(id+"F30.wireOp",EDGE,"E194.left"),sQuery(id+"F30.wireOp",EDGE,"E194.right"),sQuery(id+"F30.wireOp",EDGE,"E195.bottom"),sQuery(id+"F30.wireOp",EDGE,"E195.top"),sQuery(id+"F30.wireOp",EDGE,"E196.trimOffspring"),sQuery(id+"F30.wireOp",EDGE,"E197.trimOffspring"),sQuery(id+"F30.wireOp",EDGE,"E200.trimOffspring"),sQuery(id+"F30.wireOp",EDGE,"E201.trimOffspring"),sQuery(id+"F30.wireOp",EDGE,"E202.trimOffspring"),sQuery(id+"F30.wireOp",EDGE,"E204.trimOffspring"),sQuery(id+"F30.wireOp",EDGE,"E205.trimOffspring"),sQuery(id+"F30.wireOp",EDGE,"E207.trimOffspring"),sQuery(id+"F30.wireOp",EDGE,"E208.bottom"),sQuery(id+"F30.wireOp",EDGE,"E208.top"),subQ0,sQuery(id+"F30.wireOp",EDGE,"E208.right")])],"isStart":true}),makeQuery(id+"F46.opExtrude","SWEPT_FACE",FACE,{"disambiguationData":[OSD([subQ0]),TDD([makeQuery(id+"F31.opExtrude","CAP_EDGE",EDGE,{"disambiguationData":[OSD([subQ0])],"isStart":true})])]})]});}
            extrude(context, id + "F64", {"entities" : qUnion([Q0, Q1]), "operationType" : NewBodyOperationType.ADD, "oppositeDirection" : true, "depth" : 1 * mm});
        }
        {
            var Q0;
            Q0=makeQuery(id+"F33.opExtrude","CAP_FACE",FACE,{"disambiguationData":[OSD([sQuery(id+"F32.wireOp",EDGE,"E209.bottom"),sQuery(id+"F32.wireOp",EDGE,"E209.top"),sQuery(id+"F32.wireOp",EDGE,"E209.left"),sQuery(id+"F32.wireOp",EDGE,"E209.right"),sQuery(id+"F32.wireOp",EDGE,"E210.bottom"),sQuery(id+"F32.wireOp",EDGE,"E210.top"),sQuery(id+"F32.wireOp",EDGE,"E210.left"),sQuery(id+"F32.wireOp",EDGE,"E210.right"),sQuery(id+"F32.wireOp",EDGE,"E213.bottom"),sQuery(id+"F32.wireOp",EDGE,"E213.top"),sQuery(id+"F32.wireOp",EDGE,"E213.left"),sQuery(id+"F32.wireOp",EDGE,"E213.right"),sQuery(id+"F32.wireOp",EDGE,"E216.bottom"),sQuery(id+"F32.wireOp",EDGE,"E216.top"),sQuery(id+"F32.wireOp",EDGE,"E216.left"),sQuery(id+"F32.wireOp",EDGE,"E216.right"),sQuery(id+"F32.wireOp",EDGE,"E219.bottom"),sQuery(id+"F32.wireOp",EDGE,"E219.top"),sQuery(id+"F32.wireOp",EDGE,"E219.left"),sQuery(id+"F32.wireOp",EDGE,"E219.right")])],"isStart":true});
            extrude(context, id + "F65", {"entities" : qUnion([Q0]), "operationType" : NewBodyOperationType.ADD, "depth" : 1 * mm});
        }
        {
            var Q0;
            {var subQ0=sQuery(id+"F38.wireOp",EDGE,"E237.right");var subQ1=sQuery(id+"F38.wireOp",EDGE,"E236.right");var subQ2=sQuery(id+"F36.wireOp",EDGE,"E229.right");Q0=makeQuery(id+"F58.opExtrude","SWEPT_FACE",FACE,{"disambiguationData":[OSD([subQ2,subQ1,subQ0]),TDD([makeQuery(id+"F45.boolean.opBoolean","MERGE",EDGE,{"derivedFrom":[makeQuery(id+"F37.opExtrude","CAP_EDGE",EDGE,{"disambiguationData":[OSD([subQ2])],"isStart":true}),makeQuery(id+"F45.opExtrude","CAP_EDGE",EDGE,{"disambiguationData":[OSD([subQ1])],"isStart":true}),makeQuery(id+"F45.opExtrude","CAP_EDGE",EDGE,{"disambiguationData":[OSD([subQ0])],"isStart":true})]})])]});}
            extrude(context, id + "F66", {"entities" : qUnion([Q0]), "operationType" : NewBodyOperationType.ADD, "depth" : 2 * mm});
        }
        {
            var Q0;
            {var subQ1=sQuery(id+"F11.wireOp",EDGE,"E46.bottom");var subQ2=sQuery(id+"F11.wireOp",EDGE,"E45.right");var subQ3=sQuery(id+"F11.wireOp",EDGE,"E45.top");var subQ4=sQuery(id+"F11.wireOp",EDGE,"E45.bottom");var subQ5=sQuery(id+"F11.wireOp",EDGE,"E44.right");var subQ6=sQuery(id+"F11.wireOp",EDGE,"E44.top");var subQ7=sQuery(id+"F11.wireOp",EDGE,"E44.bottom");var subQ8=sQuery(id+"F11.wireOp",EDGE,"E43.right");var subQ9=sQuery(id+"F11.wireOp",EDGE,"E43.left");var subQ10=sQuery(id+"F11.wireOp",EDGE,"E42.right");var subQ11=sQuery(id+"F11.wireOp",EDGE,"E42.left");var subQ12=sQuery(id+"F11.wireOp",EDGE,"E42.top");var subQ13=makeQuery(id+"F12.opExtrude","CAP_FACE",FACE,{"disambiguationData":[OSD([subQ12,subQ11,subQ10,subQ9,subQ8,subQ7,subQ6,subQ5,subQ4,subQ3,subQ2,subQ1])],"isStart":false});Q0=makeQuery(id+"F44.opFillet","MERGE",FACE,{"derivedFrom":[makeQuery(id+"F12.boolean.opBoolean","SPLIT",FACE,{"disambiguationData":[TD([makeQuery(id+"F12.opExtrude","SWEPT_FACE",FACE,{"disambiguationData":[OSD([subQ12])]})])],"derivedFrom":subQ13}),makeQuery(id+"F12.boolean.opBoolean","SPLIT",FACE,{"disambiguationData":[TD([makeQuery(id+"F12.opExtrude","SWEPT_FACE",FACE,{"disambiguationData":[OSD([subQ1])]})])],"derivedFrom":subQ13}),makeQuery(id+"F12.boolean.opBoolean","SPLIT",FACE,{"disambiguationData":[TD([makeQuery(id+"F12.opExtrude","SWEPT_FACE",FACE,{"disambiguationData":[OSD([subQ5])]})])],"derivedFrom":subQ13}),makeQuery(id+"F12.boolean.opBoolean","SPLIT",FACE,{"disambiguationData":[TD([makeQuery(id+"F12.opExtrude","SWEPT_FACE",FACE,{"disambiguationData":[OSD([subQ2])]})])],"derivedFrom":subQ13})]});}
            extrude(context, id + "F67", {"entities" : qUnion([Q0]), "operationType" : NewBodyOperationType.ADD, "depth" : 0.05 * mm});
        }
        {
            var Q0;
            Q0=makeQuery(id+"F33.opExtrude","CAP_FACE",FACE,{"disambiguationData":[OSD([sQuery(id+"F32.wireOp",EDGE,"E209.bottom"),sQuery(id+"F32.wireOp",EDGE,"E209.top"),sQuery(id+"F32.wireOp",EDGE,"E209.left"),sQuery(id+"F32.wireOp",EDGE,"E209.right"),sQuery(id+"F32.wireOp",EDGE,"E210.bottom"),sQuery(id+"F32.wireOp",EDGE,"E210.top"),sQuery(id+"F32.wireOp",EDGE,"E210.left"),sQuery(id+"F32.wireOp",EDGE,"E210.right"),sQuery(id+"F32.wireOp",EDGE,"E213.bottom"),sQuery(id+"F32.wireOp",EDGE,"E213.top"),sQuery(id+"F32.wireOp",EDGE,"E213.left"),sQuery(id+"F32.wireOp",EDGE,"E213.right"),sQuery(id+"F32.wireOp",EDGE,"E216.bottom"),sQuery(id+"F32.wireOp",EDGE,"E216.top"),sQuery(id+"F32.wireOp",EDGE,"E216.left"),sQuery(id+"F32.wireOp",EDGE,"E216.right"),sQuery(id+"F32.wireOp",EDGE,"E219.bottom"),sQuery(id+"F32.wireOp",EDGE,"E219.top"),sQuery(id+"F32.wireOp",EDGE,"E219.left"),sQuery(id+"F32.wireOp",EDGE,"E219.right")])],"isStart":false});
            var sketch = newSketch(context, id + "F68", { "sketchPlane" : qUnion([Q0])});
            skLineSegment(sketch, "E258.bottom", {"start": v(22.06, -144.26) * mm, "end": v(42.46, -144.26) * mm});
            skLineSegment(sketch, "E258.top", {"start": v(22.06, -141.26) * mm, "end": v(42.46, -141.26) * mm});
            skLineSegment(sketch, "E258.left", {"start": v(22.06, -144.26) * mm, "end": v(22.06, -141.26) * mm});
            skLineSegment(sketch, "E258.right", {"start": v(42.46, -144.26) * mm, "end": v(42.46, -141.26) * mm});
            skLineSegment(sketch, "E259.bottom", {"start": v(22.06, -164.66) * mm, "end": v(42.46, -164.66) * mm});
            skLineSegment(sketch, "E259.top", {"start": v(22.06, -167.66) * mm, "end": v(42.46, -167.66) * mm});
            skLineSegment(sketch, "E259.left", {"start": v(22.06, -164.66) * mm, "end": v(22.06, -167.66) * mm});
            skLineSegment(sketch, "E259.right", {"start": v(42.46, -164.66) * mm, "end": v(42.46, -167.66) * mm});
            skLineSegment(sketch, "E260.bottom", {"start": v(22.06, -141.26) * mm, "end": v(19.06, -141.26) * mm});
            skLineSegment(sketch, "E260.top", {"start": v(22.06, -167.66) * mm, "end": v(19.06, -167.66) * mm});
            skLineSegment(sketch, "E260.left", {"start": v(22.06, -141.26) * mm, "end": v(22.06, -167.66) * mm});
            skLineSegment(sketch, "E260.right", {"start": v(19.06, -141.26) * mm, "end": v(19.06, -167.66) * mm});
            skLineSegment(sketch, "E261.bottom", {"start": v(42.46, -141.26) * mm, "end": v(45.46, -141.26) * mm});
            skLineSegment(sketch, "E261.top", {"start": v(42.46, -167.66) * mm, "end": v(45.46, -167.66) * mm});
            skLineSegment(sketch, "E261.left", {"start": v(42.46, -141.26) * mm, "end": v(42.46, -167.66) * mm});
            skLineSegment(sketch, "E261.right", {"start": v(45.46, -141.26) * mm, "end": v(45.46, -167.66) * mm});
            skLineSegment(sketch, "E262.bottom", {"start": v(52.16, -144.36) * mm, "end": v(72.36, -144.36) * mm});
            skLineSegment(sketch, "E262.top", {"start": v(52.16, -141.26) * mm, "end": v(72.36, -141.26) * mm});
            skLineSegment(sketch, "E262.left", {"start": v(52.16, -144.36) * mm, "end": v(52.16, -141.26) * mm});
            skLineSegment(sketch, "E262.right", {"start": v(72.36, -144.36) * mm, "end": v(72.36, -141.26) * mm});
            skLineSegment(sketch, "E263.bottom", {"start": v(52.16, -141.26) * mm, "end": v(49.16, -141.26) * mm});
            skLineSegment(sketch, "E263.top", {"start": v(52.16, -167.66) * mm, "end": v(49.16, -167.66) * mm});
            skLineSegment(sketch, "E263.left", {"start": v(52.16, -141.26) * mm, "end": v(52.16, -167.66) * mm});
            skLineSegment(sketch, "E263.right", {"start": v(49.16, -141.26) * mm, "end": v(49.16, -167.66) * mm});
            skLineSegment(sketch, "E264.bottom", {"start": v(52.16, -167.66) * mm, "end": v(72.36, -167.66) * mm});
            skLineSegment(sketch, "E264.top", {"start": v(52.16, -164.56) * mm, "end": v(72.36, -164.56) * mm});
            skLineSegment(sketch, "E264.left", {"start": v(52.16, -167.66) * mm, "end": v(52.16, -164.56) * mm});
            skLineSegment(sketch, "E264.right", {"start": v(72.36, -167.66) * mm, "end": v(72.36, -164.56) * mm});
            skLineSegment(sketch, "E265.bottom", {"start": v(72.36, -167.66) * mm, "end": v(75.36, -167.66) * mm});
            skLineSegment(sketch, "E265.top", {"start": v(72.36, -141.26) * mm, "end": v(75.36, -141.26) * mm});
            skLineSegment(sketch, "E265.left", {"start": v(72.36, -167.66) * mm, "end": v(72.36, -141.26) * mm});
            skLineSegment(sketch, "E265.right", {"start": v(75.36, -167.66) * mm, "end": v(75.36, -141.26) * mm});
            skLineSegment(sketch, "E266.bottom", {"start": v(82.16, -144.36) * mm, "end": v(102.36, -144.36) * mm});
            skLineSegment(sketch, "E266.top", {"start": v(82.16, -141.26) * mm, "end": v(102.36, -141.26) * mm});
            skLineSegment(sketch, "E266.left", {"start": v(82.16, -144.36) * mm, "end": v(82.16, -141.26) * mm});
            skLineSegment(sketch, "E266.right", {"start": v(102.36, -144.36) * mm, "end": v(102.36, -141.26) * mm});
            skLineSegment(sketch, "E267.bottom", {"start": v(82.16, -141.26) * mm, "end": v(79.16, -141.26) * mm});
            skLineSegment(sketch, "E267.top", {"start": v(82.16, -167.66) * mm, "end": v(79.16, -167.66) * mm});
            skLineSegment(sketch, "E267.left", {"start": v(82.16, -141.26) * mm, "end": v(82.16, -167.66) * mm});
            skLineSegment(sketch, "E267.right", {"start": v(79.16, -141.26) * mm, "end": v(79.16, -167.66) * mm});
            skLineSegment(sketch, "E268.bottom", {"start": v(82.16, -167.66) * mm, "end": v(102.36, -167.66) * mm});
            skLineSegment(sketch, "E268.top", {"start": v(82.16, -164.56) * mm, "end": v(102.36, -164.56) * mm});
            skLineSegment(sketch, "E268.left", {"start": v(82.16, -167.66) * mm, "end": v(82.16, -164.56) * mm});
            skLineSegment(sketch, "E268.right", {"start": v(102.36, -167.66) * mm, "end": v(102.36, -164.56) * mm});
            skLineSegment(sketch, "E269.bottom", {"start": v(102.36, -141.26) * mm, "end": v(105.36, -141.26) * mm});
            skLineSegment(sketch, "E269.top", {"start": v(102.36, -167.66) * mm, "end": v(105.36, -167.66) * mm});
            skLineSegment(sketch, "E269.left", {"start": v(102.36, -141.26) * mm, "end": v(102.36, -167.66) * mm});
            skLineSegment(sketch, "E269.right", {"start": v(105.36, -141.26) * mm, "end": v(105.36, -167.66) * mm});
            skLineSegment(sketch, "E270.bottom", {"start": v(112.16, -144.36) * mm, "end": v(132.36, -144.36) * mm});
            skLineSegment(sketch, "E270.top", {"start": v(112.16, -141.26) * mm, "end": v(132.36, -141.26) * mm});
            skLineSegment(sketch, "E270.left", {"start": v(112.16, -144.36) * mm, "end": v(112.16, -141.26) * mm});
            skLineSegment(sketch, "E270.right", {"start": v(132.36, -144.36) * mm, "end": v(132.36, -141.26) * mm});
            skLineSegment(sketch, "E271.bottom", {"start": v(112.16, -141.26) * mm, "end": v(109.16, -141.26) * mm});
            skLineSegment(sketch, "E271.top", {"start": v(112.16, -167.66) * mm, "end": v(109.16, -167.66) * mm});
            skLineSegment(sketch, "E271.left", {"start": v(112.16, -141.26) * mm, "end": v(112.16, -167.66) * mm});
            skLineSegment(sketch, "E271.right", {"start": v(109.16, -141.26) * mm, "end": v(109.16, -167.66) * mm});
            skLineSegment(sketch, "E272.bottom", {"start": v(112.16, -167.66) * mm, "end": v(132.36, -167.66) * mm});
            skLineSegment(sketch, "E272.top", {"start": v(112.16, -164.56) * mm, "end": v(132.36, -164.56) * mm});
            skLineSegment(sketch, "E272.left", {"start": v(112.16, -167.66) * mm, "end": v(112.16, -164.56) * mm});
            skLineSegment(sketch, "E272.right", {"start": v(132.36, -167.66) * mm, "end": v(132.36, -164.56) * mm});
            skLineSegment(sketch, "E273.bottom", {"start": v(132.36, -141.26) * mm, "end": v(135.36, -141.26) * mm});
            skLineSegment(sketch, "E273.top", {"start": v(132.36, -167.66) * mm, "end": v(135.36, -167.66) * mm});
            skLineSegment(sketch, "E273.left", {"start": v(132.36, -141.26) * mm, "end": v(132.36, -167.66) * mm});
            skLineSegment(sketch, "E273.right", {"start": v(135.36, -141.26) * mm, "end": v(135.36, -167.66) * mm});
            skSolve(sketch);
        }
        {
            var Q0;
            Q0=qSketchRegion(id+"F68",true);
            extrude(context, id + "F69", {"entities" : qUnion([Q0]), "operationType" : NewBodyOperationType.ADD, "depth" : 0.5 * mm});
        }
        {
            var Q0;
            Q0=makeQuery(id+"F69.opExtrude","CAP_FACE",FACE,{"disambiguationData":[OSD([sQuery(id+"F68.wireOp",EDGE,"E258.bottom"),sQuery(id+"F68.wireOp",EDGE,"E258.top"),sQuery(id+"F68.wireOp",EDGE,"E259.bottom"),sQuery(id+"F68.wireOp",EDGE,"E259.top"),sQuery(id+"F68.wireOp",EDGE,"E260.bottom"),sQuery(id+"F68.wireOp",EDGE,"E260.top"),sQuery(id+"F68.wireOp",EDGE,"E260.left"),sQuery(id+"F68.wireOp",EDGE,"E260.right"),sQuery(id+"F68.wireOp",EDGE,"E261.bottom"),sQuery(id+"F68.wireOp",EDGE,"E261.top"),sQuery(id+"F68.wireOp",EDGE,"E261.left"),sQuery(id+"F68.wireOp",EDGE,"E261.right")])],"isStart":false});
            var sketch = newSketch(context, id + "F70", { "sketchPlane" : qUnion([Q0])});
            skLineSegment(sketch, "E274.bottom", {"start": v(22.06, -144.26) * mm, "end": v(42.46, -144.26) * mm});
            skLineSegment(sketch, "E274.top", {"start": v(22.06, -142.76) * mm, "end": v(42.46, -142.76) * mm});
            skLineSegment(sketch, "E274.left", {"start": v(22.06, -144.26) * mm, "end": v(22.06, -142.76) * mm});
            skLineSegment(sketch, "E274.right", {"start": v(42.46, -144.26) * mm, "end": v(42.46, -142.76) * mm});
            skLineSegment(sketch, "E275.bottom", {"start": v(22.06, -164.66) * mm, "end": v(42.46, -164.66) * mm});
            skLineSegment(sketch, "E275.top", {"start": v(22.06, -166.16) * mm, "end": v(42.46, -166.16) * mm});
            skLineSegment(sketch, "E275.left", {"start": v(22.06, -164.66) * mm, "end": v(22.06, -166.16) * mm});
            skLineSegment(sketch, "E275.right", {"start": v(42.46, -164.66) * mm, "end": v(42.46, -166.16) * mm});
            skLineSegment(sketch, "E276.bottom", {"start": v(22.06, -166.16) * mm, "end": v(20.56, -166.16) * mm});
            skLineSegment(sketch, "E276.top", {"start": v(22.06, -142.76) * mm, "end": v(20.56, -142.76) * mm});
            skLineSegment(sketch, "E276.left", {"start": v(22.06, -166.16) * mm, "end": v(22.06, -142.76) * mm});
            skLineSegment(sketch, "E276.right", {"start": v(20.56, -166.16) * mm, "end": v(20.56, -142.76) * mm});
            skLineSegment(sketch, "E277.bottom", {"start": v(42.46, -166.16) * mm, "end": v(43.96, -166.16) * mm});
            skLineSegment(sketch, "E277.top", {"start": v(42.46, -142.76) * mm, "end": v(43.96, -142.76) * mm});
            skLineSegment(sketch, "E277.left", {"start": v(42.46, -166.16) * mm, "end": v(42.46, -142.76) * mm});
            skLineSegment(sketch, "E277.right", {"start": v(43.96, -166.16) * mm, "end": v(43.96, -142.76) * mm});
            skLineSegment(sketch, "E278.bottom", {"start": v(50.66, -142.86) * mm, "end": v(52.16, -142.86) * mm});
            skLineSegment(sketch, "E278.top", {"start": v(50.66, -166.06) * mm, "end": v(52.16, -166.06) * mm});
            skLineSegment(sketch, "E278.left", {"start": v(50.66, -142.86) * mm, "end": v(50.66, -166.06) * mm});
            skLineSegment(sketch, "E278.right", {"start": v(52.16, -142.86) * mm, "end": v(52.16, -166.06) * mm});
            skLineSegment(sketch, "E279.bottom", {"start": v(72.36, -142.86) * mm, "end": v(73.86, -142.86) * mm});
            skLineSegment(sketch, "E279.top", {"start": v(72.36, -166.06) * mm, "end": v(73.86, -166.06) * mm});
            skLineSegment(sketch, "E279.left", {"start": v(72.36, -142.86) * mm, "end": v(72.36, -166.06) * mm});
            skLineSegment(sketch, "E279.right", {"start": v(73.86, -142.86) * mm, "end": v(73.86, -166.06) * mm});
            skLineSegment(sketch, "E280.bottom", {"start": v(52.16, -142.86) * mm, "end": v(72.36, -142.86) * mm});
            skLineSegment(sketch, "E280.top", {"start": v(52.16, -144.36) * mm, "end": v(72.36, -144.36) * mm});
            skLineSegment(sketch, "E280.left", {"start": v(52.16, -142.86) * mm, "end": v(52.16, -144.36) * mm});
            skLineSegment(sketch, "E280.right", {"start": v(72.36, -142.86) * mm, "end": v(72.36, -144.36) * mm});
            skLineSegment(sketch, "E281.bottom", {"start": v(52.16, -166.06) * mm, "end": v(72.36, -166.06) * mm});
            skLineSegment(sketch, "E281.top", {"start": v(52.16, -164.56) * mm, "end": v(72.36, -164.56) * mm});
            skLineSegment(sketch, "E281.left", {"start": v(52.16, -166.06) * mm, "end": v(52.16, -164.56) * mm});
            skLineSegment(sketch, "E281.right", {"start": v(72.36, -166.06) * mm, "end": v(72.36, -164.56) * mm});
            skLineSegment(sketch, "E282.bottom", {"start": v(80.66, -142.86) * mm, "end": v(82.16, -142.86) * mm});
            skLineSegment(sketch, "E282.top", {"start": v(80.66, -166.06) * mm, "end": v(82.16, -166.06) * mm});
            skLineSegment(sketch, "E282.left", {"start": v(80.66, -142.86) * mm, "end": v(80.66, -166.06) * mm});
            skLineSegment(sketch, "E282.right", {"start": v(82.16, -142.86) * mm, "end": v(82.16, -166.06) * mm});
            skLineSegment(sketch, "E283.bottom", {"start": v(82.16, -142.86) * mm, "end": v(102.36, -142.86) * mm});
            skLineSegment(sketch, "E283.top", {"start": v(82.16, -144.36) * mm, "end": v(102.36, -144.36) * mm});
            skLineSegment(sketch, "E283.left", {"start": v(82.16, -142.86) * mm, "end": v(82.16, -144.36) * mm});
            skLineSegment(sketch, "E283.right", {"start": v(102.36, -142.86) * mm, "end": v(102.36, -144.36) * mm});
            skLineSegment(sketch, "E284.bottom", {"start": v(82.16, -166.06) * mm, "end": v(102.36, -166.06) * mm});
            skLineSegment(sketch, "E284.top", {"start": v(82.16, -164.56) * mm, "end": v(102.36, -164.56) * mm});
            skLineSegment(sketch, "E284.left", {"start": v(82.16, -166.06) * mm, "end": v(82.16, -164.56) * mm});
            skLineSegment(sketch, "E284.right", {"start": v(102.36, -166.06) * mm, "end": v(102.36, -164.56) * mm});
            skLineSegment(sketch, "E285.bottom", {"start": v(102.36, -166.06) * mm, "end": v(103.86, -166.06) * mm});
            skLineSegment(sketch, "E285.top", {"start": v(102.36, -142.86) * mm, "end": v(103.86, -142.86) * mm});
            skLineSegment(sketch, "E285.left", {"start": v(102.36, -166.06) * mm, "end": v(102.36, -142.86) * mm});
            skLineSegment(sketch, "E285.right", {"start": v(103.86, -166.06) * mm, "end": v(103.86, -142.86) * mm});
            skLineSegment(sketch, "E286.bottom", {"start": v(110.76, -142.86) * mm, "end": v(112.26, -142.86) * mm});
            skLineSegment(sketch, "E286.top", {"start": v(110.76, -166.06) * mm, "end": v(112.26, -166.06) * mm});
            skLineSegment(sketch, "E286.left", {"start": v(110.76, -142.86) * mm, "end": v(110.76, -166.06) * mm});
            skLineSegment(sketch, "E286.right", {"start": v(112.26, -142.86) * mm, "end": v(112.26, -166.06) * mm});
            skLineSegment(sketch, "E287.bottom", {"start": v(112.26, -142.86) * mm, "end": v(132.46, -142.86) * mm});
            skLineSegment(sketch, "E287.top", {"start": v(112.26, -144.36) * mm, "end": v(132.46, -144.36) * mm});
            skLineSegment(sketch, "E287.left", {"start": v(112.26, -142.86) * mm, "end": v(112.26, -144.36) * mm});
            skLineSegment(sketch, "E287.right", {"start": v(132.46, -142.86) * mm, "end": v(132.46, -144.36) * mm});
            skLineSegment(sketch, "E288.bottom", {"start": v(112.26, -166.06) * mm, "end": v(132.46, -166.06) * mm});
            skLineSegment(sketch, "E288.top", {"start": v(112.26, -164.56) * mm, "end": v(132.46, -164.56) * mm});
            skLineSegment(sketch, "E288.left", {"start": v(112.26, -166.06) * mm, "end": v(112.26, -164.56) * mm});
            skLineSegment(sketch, "E288.right", {"start": v(132.46, -166.06) * mm, "end": v(132.46, -164.56) * mm});
            skLineSegment(sketch, "E289.bottom", {"start": v(132.46, -166.06) * mm, "end": v(133.96, -166.06) * mm});
            skLineSegment(sketch, "E289.top", {"start": v(132.46, -142.86) * mm, "end": v(133.96, -142.86) * mm});
            skLineSegment(sketch, "E289.left", {"start": v(132.46, -166.06) * mm, "end": v(132.46, -142.86) * mm});
            skLineSegment(sketch, "E289.right", {"start": v(133.96, -166.06) * mm, "end": v(133.96, -142.86) * mm});
            skSolve(sketch);
        }
        {
            var Q0;
            Q0=qSketchRegion(id+"F70",true);
            extrude(context, id + "F71", {"entities" : qUnion([Q0]), "operationType" : NewBodyOperationType.ADD, "depth" : 1 * mm});
        }
        {
            var Q0;
            Q0=makeQuery(id+"F69.opExtrude","SWEPT_EDGE",EDGE,{"disambiguationData":[OSD([sQuery(id+"F68.wireOp",EDGE,"E260.bottom"),sQuery(id+"F68.wireOp",EDGE,"E260.right")])]});
            var Q1;
            Q1=makeQuery(id+"F71.opExtrude","SWEPT_EDGE",EDGE,{"disambiguationData":[OSD([sQuery(id+"F70.wireOp",EDGE,"E276.top"),sQuery(id+"F70.wireOp",EDGE,"E276.right")])]});
            var Q2;
            Q2=makeQuery(id+"F69.opExtrude","SWEPT_EDGE",EDGE,{"disambiguationData":[OSD([sQuery(id+"F68.wireOp",EDGE,"E260.top"),sQuery(id+"F68.wireOp",EDGE,"E260.right")])]});
            var Q3;
            Q3=makeQuery(id+"F71.opExtrude","SWEPT_EDGE",EDGE,{"disambiguationData":[OSD([sQuery(id+"F70.wireOp",EDGE,"E276.bottom"),sQuery(id+"F70.wireOp",EDGE,"E276.right")])]});
            var Q4;
            Q4=makeQuery(id+"F71.opExtrude","SWEPT_EDGE",EDGE,{"disambiguationData":[OSD([sQuery(id+"F70.wireOp",EDGE,"E277.bottom"),sQuery(id+"F70.wireOp",EDGE,"E277.right")])]});
            var Q5;
            Q5=makeQuery(id+"F69.opExtrude","SWEPT_EDGE",EDGE,{"disambiguationData":[OSD([sQuery(id+"F68.wireOp",EDGE,"E261.top"),sQuery(id+"F68.wireOp",EDGE,"E261.right")])]});
            var Q6;
            Q6=makeQuery(id+"F71.opExtrude","SWEPT_EDGE",EDGE,{"disambiguationData":[OSD([sQuery(id+"F70.wireOp",EDGE,"E277.top"),sQuery(id+"F70.wireOp",EDGE,"E277.right")])]});
            var Q7;
            Q7=makeQuery(id+"F69.opExtrude","SWEPT_EDGE",EDGE,{"disambiguationData":[OSD([sQuery(id+"F68.wireOp",EDGE,"E261.bottom"),sQuery(id+"F68.wireOp",EDGE,"E261.right")])]});
            var Q8;
            Q8=makeQuery(id+"F69.opExtrude","SWEPT_EDGE",EDGE,{"disambiguationData":[OSD([sQuery(id+"F68.wireOp",EDGE,"E263.bottom"),sQuery(id+"F68.wireOp",EDGE,"E263.right")])]});
            var Q9;
            Q9=makeQuery(id+"F71.opExtrude","SWEPT_EDGE",EDGE,{"disambiguationData":[OSD([sQuery(id+"F70.wireOp",EDGE,"E278.bottom"),sQuery(id+"F70.wireOp",EDGE,"E278.left")])]});
            var Q10;
            Q10=makeQuery(id+"F71.opExtrude","SWEPT_EDGE",EDGE,{"disambiguationData":[OSD([sQuery(id+"F70.wireOp",EDGE,"E278.top"),sQuery(id+"F70.wireOp",EDGE,"E278.left")])]});
            var Q11;
            Q11=makeQuery(id+"F69.opExtrude","SWEPT_EDGE",EDGE,{"disambiguationData":[OSD([sQuery(id+"F68.wireOp",EDGE,"E263.top"),sQuery(id+"F68.wireOp",EDGE,"E263.right")])]});
            var Q12;
            Q12=makeQuery(id+"F71.opExtrude","SWEPT_EDGE",EDGE,{"disambiguationData":[OSD([sQuery(id+"F70.wireOp",EDGE,"E279.top"),sQuery(id+"F70.wireOp",EDGE,"E279.right")])]});
            var Q13;
            Q13=makeQuery(id+"F69.opExtrude","SWEPT_EDGE",EDGE,{"disambiguationData":[OSD([sQuery(id+"F68.wireOp",EDGE,"E265.bottom"),sQuery(id+"F68.wireOp",EDGE,"E265.right")])]});
            var Q14;
            Q14=makeQuery(id+"F71.opExtrude","SWEPT_EDGE",EDGE,{"disambiguationData":[OSD([sQuery(id+"F70.wireOp",EDGE,"E279.bottom"),sQuery(id+"F70.wireOp",EDGE,"E279.right")])]});
            var Q15;
            Q15=makeQuery(id+"F69.opExtrude","SWEPT_EDGE",EDGE,{"disambiguationData":[OSD([sQuery(id+"F68.wireOp",EDGE,"E265.top"),sQuery(id+"F68.wireOp",EDGE,"E265.right")])]});
            var Q16;
            Q16=makeQuery(id+"F69.opExtrude","SWEPT_EDGE",EDGE,{"disambiguationData":[OSD([sQuery(id+"F68.wireOp",EDGE,"E267.bottom"),sQuery(id+"F68.wireOp",EDGE,"E267.right")])]});
            var Q17;
            Q17=makeQuery(id+"F71.opExtrude","SWEPT_EDGE",EDGE,{"disambiguationData":[OSD([sQuery(id+"F70.wireOp",EDGE,"E282.bottom"),sQuery(id+"F70.wireOp",EDGE,"E282.left")])]});
            var Q18;
            Q18=makeQuery(id+"F69.opExtrude","SWEPT_EDGE",EDGE,{"disambiguationData":[OSD([sQuery(id+"F68.wireOp",EDGE,"E267.top"),sQuery(id+"F68.wireOp",EDGE,"E267.right")])]});
            var Q19;
            Q19=makeQuery(id+"F71.opExtrude","SWEPT_EDGE",EDGE,{"disambiguationData":[OSD([sQuery(id+"F70.wireOp",EDGE,"E282.top"),sQuery(id+"F70.wireOp",EDGE,"E282.left")])]});
            var Q20;
            Q20=makeQuery(id+"F71.opExtrude","SWEPT_EDGE",EDGE,{"disambiguationData":[OSD([sQuery(id+"F70.wireOp",EDGE,"E285.bottom"),sQuery(id+"F70.wireOp",EDGE,"E285.right")])]});
            var Q21;
            Q21=makeQuery(id+"F69.opExtrude","SWEPT_EDGE",EDGE,{"disambiguationData":[OSD([sQuery(id+"F68.wireOp",EDGE,"E269.top"),sQuery(id+"F68.wireOp",EDGE,"E269.right")])]});
            var Q22;
            Q22=makeQuery(id+"F71.opExtrude","SWEPT_EDGE",EDGE,{"disambiguationData":[OSD([sQuery(id+"F70.wireOp",EDGE,"E285.top"),sQuery(id+"F70.wireOp",EDGE,"E285.right")])]});
            var Q23;
            Q23=makeQuery(id+"F69.opExtrude","SWEPT_EDGE",EDGE,{"disambiguationData":[OSD([sQuery(id+"F68.wireOp",EDGE,"E269.bottom"),sQuery(id+"F68.wireOp",EDGE,"E269.right")])]});
            var Q24;
            Q24=makeQuery(id+"F69.opExtrude","SWEPT_EDGE",EDGE,{"disambiguationData":[OSD([sQuery(id+"F68.wireOp",EDGE,"E271.bottom"),sQuery(id+"F68.wireOp",EDGE,"E271.right")])]});
            var Q25;
            Q25=makeQuery(id+"F71.opExtrude","SWEPT_EDGE",EDGE,{"disambiguationData":[OSD([sQuery(id+"F70.wireOp",EDGE,"E286.bottom"),sQuery(id+"F70.wireOp",EDGE,"E286.left")])]});
            var Q26;
            Q26=makeQuery(id+"F69.opExtrude","SWEPT_EDGE",EDGE,{"disambiguationData":[OSD([sQuery(id+"F68.wireOp",EDGE,"E271.top"),sQuery(id+"F68.wireOp",EDGE,"E271.right")])]});
            var Q27;
            Q27=makeQuery(id+"F71.opExtrude","SWEPT_EDGE",EDGE,{"disambiguationData":[OSD([sQuery(id+"F70.wireOp",EDGE,"E286.top"),sQuery(id+"F70.wireOp",EDGE,"E286.left")])]});
            var Q28;
            Q28=makeQuery(id+"F71.opExtrude","SWEPT_EDGE",EDGE,{"disambiguationData":[OSD([sQuery(id+"F70.wireOp",EDGE,"E289.bottom"),sQuery(id+"F70.wireOp",EDGE,"E289.right")])]});
            var Q29;
            Q29=makeQuery(id+"F69.opExtrude","SWEPT_EDGE",EDGE,{"disambiguationData":[OSD([sQuery(id+"F68.wireOp",EDGE,"E273.top"),sQuery(id+"F68.wireOp",EDGE,"E273.right")])]});
            var Q30;
            Q30=makeQuery(id+"F71.opExtrude","SWEPT_EDGE",EDGE,{"disambiguationData":[OSD([sQuery(id+"F70.wireOp",EDGE,"E289.top"),sQuery(id+"F70.wireOp",EDGE,"E289.right")])]});
            var Q31;
            Q31=makeQuery(id+"F69.opExtrude","SWEPT_EDGE",EDGE,{"disambiguationData":[OSD([sQuery(id+"F68.wireOp",EDGE,"E273.bottom"),sQuery(id+"F68.wireOp",EDGE,"E273.right")])]});
            fillet(context, id + "F72", {"entities" : qUnion([Q0, Q1, Q2, Q3, Q4, Q5, Q6, Q7, Q8, Q9, Q10, Q11, Q12, Q13, Q14, Q15, Q16, Q17, Q18, Q19, Q20, Q21, Q22, Q23, Q24, Q25, Q26, Q27, Q28, Q29, Q30, Q31]), "radius" : 0.5 * mm, "tangentPropagation" : true, "allowEdgeOverflow" : false});
        }
        {
            var Q0;
            Q0=makeQuery(id+"F10.opExtrude","CAP_FACE",FACE,{"disambiguationData":[OSD([sQuery(id+"F9.wireOp",EDGE,"E41.bottom"),sQuery(id+"F9.wireOp",EDGE,"E41.top"),sQuery(id+"F9.wireOp",EDGE,"E41.left"),sQuery(id+"F9.wireOp",EDGE,"E41.right")])],"isStart":false});
            var sketch = newSketch(context, id + "F73", { "sketchPlane" : qUnion([Q0])});
            skLineSegment(sketch, "E290.bottom", {"start": v(-87.88, 7.7) * mm, "end": v(-69.88, 7.7) * mm});
            skLineSegment(sketch, "E290.top", {"start": v(-87.88, -10.3) * mm, "end": v(-69.88, -10.3) * mm});
            skLineSegment(sketch, "E290.left", {"start": v(-87.88, 7.7) * mm, "end": v(-87.88, -10.3) * mm});
            skLineSegment(sketch, "E290.right", {"start": v(-69.88, 7.7) * mm, "end": v(-69.88, -10.3) * mm});
            skSolve(sketch);
        }
        {
            var Q0;
            Q0=qSketchRegion(id+"F73",true);
            extrude(context, id + "F74", {"entities" : qUnion([Q0]), "operationType" : NewBodyOperationType.REMOVE, "oppositeDirection" : true, "depth" : 1 * mm});
        }
        {
            var Q0;
            Q0=qCreatedBy(makeId("Top.planeOp"),FACE);
            var sketch = newSketch(context, id + "F75", { "sketchPlane" : qUnion([Q0])});
            skLineSegment(sketch, "E291.bottom", {"start": v(-55.36, 28.1) * mm, "end": v(-37.56, 28.1) * mm});
            skLineSegment(sketch, "E291.top", {"start": v(-55.36, 10.3) * mm, "end": v(-37.56, 10.3) * mm});
            skLineSegment(sketch, "E291.left", {"start": v(-55.36, 28.1) * mm, "end": v(-55.36, 10.3) * mm});
            skLineSegment(sketch, "E291.right", {"start": v(-37.56, 28.1) * mm, "end": v(-37.56, 10.3) * mm});
            skSolve(sketch);
        }
        {
            var Q0;
            Q0=qSketchRegion(id+"F75",true);
            extrude(context, id + "F76", {"entities" : qUnion([Q0]), "depth" : 1 * mm});
        }
        {
            var Q0;
            Q0=makeQuery(id+"F1.opExtrude","CAP_FACE",FACE,{"disambiguationData":[OSD([sQuery(id+"F0.wireOp",EDGE,"E1.bottom"),sQuery(id+"F0.wireOp",EDGE,"E1.top"),sQuery(id+"F0.wireOp",EDGE,"E1.left"),sQuery(id+"F0.wireOp",EDGE,"E1.right")])],"isStart":false});
            var sketch = newSketch(context, id + "F77", { "sketchPlane" : qUnion([Q0])});
            skLineSegment(sketch, "E292.bottom", {"start": v(9, 9) * mm, "end": v(-9, 9) * mm});
            skLineSegment(sketch, "E292.top", {"start": v(9, -9) * mm, "end": v(-9, -9) * mm});
            skLineSegment(sketch, "E292.left", {"start": v(9, 9) * mm, "end": v(9, -9) * mm});
            skLineSegment(sketch, "E292.right", {"start": v(-9, 9) * mm, "end": v(-9, -9) * mm});
            skPoint(sketch, "E292.middle", {"position": v(0, 0) * mm});
            skSolve(sketch);
        }
        {
            var Q0;
            Q0=qSketchRegion(id+"F77",true);
            extrude(context, id + "F78", {"entities" : qUnion([Q0]), "operationType" : NewBodyOperationType.REMOVE, "oppositeDirection" : true, "depth" : 1 * mm});
        }
    });
